# Revit family: Canilo
name_source: partatom
category: Lighting Fixtures
revit_build: Autodesk Revit 2017 (Build: 20190508_0315(x64)
units: mm (PartAtom-declared; Revit-internal decimal feet)

## family parameters
Cut with Voids When Loaded = No
Host = Face
Light Source = No
OmniClass Number = 23.80.70.11
OmniClass Title = Luminaries for Internal Lighting
Part Type = Normal
Room Calculation Point = No
Round Connector Dimension = Use Diameter
Shared = Yes

## types (810) — shared parameters
Canilo_Deko_Mat = Oktalite_Alu_RAL_9016
DegreeOfProtection = IP20
Height = 215 mm  [stored 0.705381 ft]
Length = 105 mm
Light Source = Canilo_LS : CANILO_LED_SP_2700_2705
Manufacturer = Oktalite
Mounting = 3-circuit track adapter
ProductDataSheet = http://www.oktalite.com
Reference = CANILO
URL = http://www.oktalite.com
Weight = 1.8
Width = 125 mm  [stored 0.410105 ft]
zero-valued in all types: Ceiling cut-out, Default Elevation, Installation depth, Suspension Height, Suspension length

## per-type parameters (varying)
| type | Apparent Load | Beam angle | CRI | Cover / filter | IESFile | Lamp | Light colour | Lighting technology | Lumen category | Luminaire colour | Mat | SEO | System performance | TK_Body | TK_Optic | system luminous flux |
| CANILO  3P 05 LED2000-M VFL-c ETDD 05 | 31 VA | Very Wide Flood | - | clear | CANILO_LED IQ_VFL.ies | LED IQ | M | LED IQ | 2000 lm | RAL 9005 jet black | Oktalite_Alu_RAL_9005 | Oktalite_Canilo_WH3100 | 31 VA | 10161299 | 10147536 | 1890 lm |
| CANILO  3P 05 LED2000-M VFL  ETDD 05 | 31 VA | Very Wide Flood | - | without | CANILO_LED IQ_VFL.ies | LED IQ | M | LED IQ | 2000 lm | RAL 9005 jet black | Oktalite_Alu_RAL_9005 | Oktalite_Canilo_WH3100 | 31 VA | 10161299 | 10147502 | 1890 lm |
| CANILO  3P 05 LED2000-M WFL-c ETDD 05 | 31 VA | Wide Flood | - | clear | CANILO_LED IQ_WFL.ies | LED IQ | M | LED IQ | 2000 lm | RAL 9005 jet black | Oktalite_Alu_RAL_9005 | Oktalite_Canilo_WH3100 | 31 VA | 10161299 | 10147535 | 1890 lm |
| CANILO  3P 05 LED2000-M WFL  ETDD 05 | 31 VA | Wide Flood | - | without | CANILO_LED IQ_WFL.ies | LED IQ | M | LED IQ | 2000 lm | RAL 9005 jet black | Oktalite_Alu_RAL_9005 | Oktalite_Canilo_WH3100 | 31 VA | 10161299 | 10147501 | 1890 lm |
| CANILO  3P 05 LED2000-M FL-c ETDD 05 | 31 VA | Flood | - | clear | CANILO_LED IQ_FL.ies | LED IQ | M | LED IQ | 2000 lm | RAL 9005 jet black | Oktalite_Alu_RAL_9005 | Oktalite_Canilo_WH3100 | 31 VA | 10161299 | 10127064 | 1890 lm |
| CANILO  3P 05 LED2000-M FL  ETDD 05 | 31 VA | Flood | - | without | CANILO_LED IQ_FL.ies | LED IQ | M | LED IQ | 2000 lm | RAL 9005 jet black | Oktalite_Alu_RAL_9005 | Oktalite_Canilo_WH3100 | 31 VA | 10161299 | 10125196 | 1890 lm |
| CANILO  3P 05 LED2000-M MF-c ETDD 05 | 31 VA | Medium Flood | - | clear | CANILO_LED IQ_MF.ies | LED IQ | M | LED IQ | 2000 lm | RAL 9005 jet black | Oktalite_Alu_RAL_9005 | Oktalite_Canilo_WH3100 | 31 VA | 10161299 | 10127063 | 1890 lm |
| CANILO  3P 05 LED2000-M MF  ETDD 05 | 31 VA | Medium Flood | - | without | CANILO_LED IQ_MF.ies | LED IQ | M | LED IQ | 2000 lm | RAL 9005 jet black | Oktalite_Alu_RAL_9005 | Oktalite_Canilo_WH3100 | 31 VA | 10161299 | 10125193 | 1890 lm |
| CANILO  3P 05 LED2000-M SP-c ETDD 05 | 31 VA | Spot | - | clear | CANILO_LED IQ_SP.ies | LED IQ | M | LED IQ | 2000 lm | RAL 9005 jet black | Oktalite_Alu_RAL_9005 | Oktalite_Canilo_WH3100 | 31 VA | 10161299 | 10127062 | 1890 lm |
| CANILO  3P 05 LED2000-M SP  ETDD 05 | 31 VA | Spot | - | without | CANILO_LED IQ_SP.ies | LED IQ | M | LED IQ | 2000 lm | RAL 9005 jet black | Oktalite_Alu_RAL_9005 | Oktalite_Canilo_WH3100 | 31 VA | 10161299 | 10125190 | 1890 lm |
| CANILO  3P 05 LED2000-M VFL-c ETDD 03 | 31 VA | Very Wide Flood | - | clear | CANILO_LED IQ_VFL.ies | LED IQ | M | LED IQ | 2000 lm | RAL 9006 white aluminium | Oktalite_Alu_RAL_9006 | Oktalite_Canilo_WH3100 | 31 VA | 10161298 | 10147536 | 1890 lm |
| CANILO  3P 05 LED2000-M VFL  ETDD 03 | 31 VA | Very Wide Flood | - | without | CANILO_LED IQ_VFL.ies | LED IQ | M | LED IQ | 2000 lm | RAL 9006 white aluminium | Oktalite_Alu_RAL_9006 | Oktalite_Canilo_WH3100 | 31 VA | 10161298 | 10147502 | 1890 lm |
| CANILO  3P 05 LED2000-M WFL-c ETDD 03 | 31 VA | Wide Flood | - | clear | CANILO_LED IQ_WFL.ies | LED IQ | M | LED IQ | 2000 lm | RAL 9006 white aluminium | Oktalite_Alu_RAL_9006 | Oktalite_Canilo_WH3100 | 31 VA | 10161298 | 10147535 | 1890 lm |
| CANILO  3P 05 LED2000-M WFL  ETDD 03 | 31 VA | Wide Flood | - | without | CANILO_LED IQ_WFL.ies | LED IQ | M | LED IQ | 2000 lm | RAL 9006 white aluminium | Oktalite_Alu_RAL_9006 | Oktalite_Canilo_WH3100 | 31 VA | 10161298 | 10147501 | 1890 lm |
| CANILO  3P 05 LED2000-M FL-c ETDD 03 | 31 VA | Flood | - | clear | CANILO_LED IQ_FL.ies | LED IQ | M | LED IQ | 2000 lm | RAL 9006 white aluminium | Oktalite_Alu_RAL_9006 | Oktalite_Canilo_WH3100 | 31 VA | 10161298 | 10127064 | 1890 lm |
| CANILO  3P 05 LED2000-M FL  ETDD 03 | 31 VA | Flood | - | without | CANILO_LED IQ_FL.ies | LED IQ | M | LED IQ | 2000 lm | RAL 9006 white aluminium | Oktalite_Alu_RAL_9006 | Oktalite_Canilo_WH3100 | 31 VA | 10161298 | 10125196 | 1890 lm |
| CANILO  3P 05 LED2000-M MF-c ETDD 03 | 31 VA | Medium Flood | - | clear | CANILO_LED IQ_MF.ies | LED IQ | M | LED IQ | 2000 lm | RAL 9006 white aluminium | Oktalite_Alu_RAL_9006 | Oktalite_Canilo_WH3100 | 31 VA | 10161298 | 10127063 | 1890 lm |
| CANILO  3P 05 LED2000-M MF  ETDD 03 | 31 VA | Medium Flood | - | without | CANILO_LED IQ_MF.ies | LED IQ | M | LED IQ | 2000 lm | RAL 9006 white aluminium | Oktalite_Alu_RAL_9006 | Oktalite_Canilo_WH3100 | 31 VA | 10161298 | 10125193 | 1890 lm |
| CANILO  3P 05 LED2000-M SP-c ETDD 03 | 31 VA | Spot | - | clear | CANILO_LED IQ_SP.ies | LED IQ | M | LED IQ | 2000 lm | RAL 9006 white aluminium | Oktalite_Alu_RAL_9006 | Oktalite_Canilo_WH3100 | 31 VA | 10161298 | 10127062 | 1890 lm |
| CANILO  3P 05 LED2000-M SP  ETDD 03 | 31 VA | Spot | - | without | CANILO_LED IQ_SP.ies | LED IQ | M | LED IQ | 2000 lm | RAL 9006 white aluminium | Oktalite_Alu_RAL_9006 | Oktalite_Canilo_WH3100 | 31 VA | 10161298 | 10125190 | 1890 lm |
| CANILO  3P 01 LED2000-M VFL-c ETDD 01 | 31 VA | Very Wide Flood | - | clear | CANILO_LED IQ_VFL.ies | LED IQ | M | LED IQ | 2000 lm | RAL 9016 traffic white | Oktalite_Alu_RAL_9016 | Oktalite_Canilo_WH3100 | 31 VA | 10161297 | 10147536 | 1890 lm |
| CANILO  3P 01 LED2000-M VFL  ETDD 01 | 31 VA | Very Wide Flood | - | without | CANILO_LED IQ_VFL.ies | LED IQ | M | LED IQ | 2000 lm | RAL 9016 traffic white | Oktalite_Alu_RAL_9016 | Oktalite_Canilo_WH3100 | 31 VA | 10161297 | 10147502 | 1890 lm |
| CANILO  3P 01 LED2000-M WFL-c ETDD 01 | 31 VA | Wide Flood | - | clear | CANILO_LED IQ_WFL.ies | LED IQ | M | LED IQ | 2000 lm | RAL 9016 traffic white | Oktalite_Alu_RAL_9016 | Oktalite_Canilo_WH3100 | 31 VA | 10161297 | 10147535 | 1890 lm |
| CANILO  3P 01 LED2000-M WFL  ETDD 01 | 31 VA | Wide Flood | - | without | CANILO_LED IQ_WFL.ies | LED IQ | M | LED IQ | 2000 lm | RAL 9016 traffic white | Oktalite_Alu_RAL_9016 | Oktalite_Canilo_WH3100 | 31 VA | 10161297 | 10147501 | 1890 lm |
| CANILO  3P 01 LED2000-M FL-c ETDD 01 | 31 VA | Flood | - | clear | CANILO_LED IQ_FL.ies | LED IQ | M | LED IQ | 2000 lm | RAL 9016 traffic white | Oktalite_Alu_RAL_9016 | Oktalite_Canilo_WH3100 | 31 VA | 10161297 | 10127064 | 1890 lm |
| CANILO  3P 01 LED2000-M FL  ETDD 01 | 31 VA | Flood | - | without | CANILO_LED IQ_FL.ies | LED IQ | M | LED IQ | 2000 lm | RAL 9016 traffic white | Oktalite_Alu_RAL_9016 | Oktalite_Canilo_WH3100 | 31 VA | 10161297 | 10125196 | 1890 lm |
| CANILO  3P 01 LED2000-M MF-c ETDD 01 | 31 VA | Medium Flood | - | clear | CANILO_LED IQ_MF.ies | LED IQ | M | LED IQ | 2000 lm | RAL 9016 traffic white | Oktalite_Alu_RAL_9016 | Oktalite_Canilo_WH3100 | 31 VA | 10161297 | 10127063 | 1890 lm |
| CANILO  3P 01 LED2000-M MF  ETDD 01 | 31 VA | Medium Flood | - | without | CANILO_LED IQ_MF.ies | LED IQ | M | LED IQ | 2000 lm | RAL 9016 traffic white | Oktalite_Alu_RAL_9016 | Oktalite_Canilo_WH3100 | 31 VA | 10161297 | 10125193 | 1890 lm |
| CANILO  3P 01 LED2000-M SP-c ETDD 01 | 31 VA | Spot | - | clear | CANILO_LED IQ_SP.ies | LED IQ | M | LED IQ | 2000 lm | RAL 9016 traffic white | Oktalite_Alu_RAL_9016 | Oktalite_Canilo_WH3100 | 31 VA | 10161297 | 10127062 | 1890 lm |
| CANILO  3P 01 LED2000-M SP  ETDD 01 | 31 VA | Spot | - | without | CANILO_LED IQ_SP.ies | LED IQ | M | LED IQ | 2000 lm | RAL 9016 traffic white | Oktalite_Alu_RAL_9016 | Oktalite_Canilo_WH3100 | 31 VA | 10161297 | 10125190 | 1890 lm |
| CANILO  3P 05 LED2000-M+F VFL-c ETDD 05 | 31 VA | Very Wide Flood | - | clear | CANILO_LED IQ_VFL.ies | LED IQ | M+F | LED IQ | 2000 lm | RAL 9005 jet black | Oktalite_Alu_RAL_9005 | Oktalite_Canilo_WH3100 | 31 VA | 10161308 | 10147536 | 1785 lm |
| CANILO  3P 05 LED2000-M+F VFL  ETDD 05 | 31 VA | Very Wide Flood | - | without | CANILO_LED IQ_VFL.ies | LED IQ | M+F | LED IQ | 2000 lm | RAL 9005 jet black | Oktalite_Alu_RAL_9005 | Oktalite_Canilo_WH3100 | 31 VA | 10161308 | 10147502 | 1785 lm |
| CANILO  3P 05 LED2000-M+F WFL-c ETDD 05 | 31 VA | Wide Flood | - | clear | CANILO_LED IQ_WFL.ies | LED IQ | M+F | LED IQ | 2000 lm | RAL 9005 jet black | Oktalite_Alu_RAL_9005 | Oktalite_Canilo_WH3100 | 31 VA | 10161308 | 10147535 | 1785 lm |
| CANILO  3P 05 LED2000-M+F WFL  ETDD 05 | 31 VA | Wide Flood | - | without | CANILO_LED IQ_WFL.ies | LED IQ | M+F | LED IQ | 2000 lm | RAL 9005 jet black | Oktalite_Alu_RAL_9005 | Oktalite_Canilo_WH3100 | 31 VA | 10161308 | 10147501 | 1785 lm |
| CANILO  3P 05 LED2000-M+F FL-c ETDD 05 | 31 VA | Flood | - | clear | CANILO_LED IQ_FL.ies | LED IQ | M+F | LED IQ | 2000 lm | RAL 9005 jet black | Oktalite_Alu_RAL_9005 | Oktalite_Canilo_WH3100 | 31 VA | 10161308 | 10127064 | 1785 lm |
| CANILO  3P 05 LED2000-M+F FL  ETDD 05 | 31 VA | Flood | - | without | CANILO_LED IQ_FL.ies | LED IQ | M+F | LED IQ | 2000 lm | RAL 9005 jet black | Oktalite_Alu_RAL_9005 | Oktalite_Canilo_WH3100 | 31 VA | 10161308 | 10125196 | 1785 lm |
| CANILO  3P 05 LED2000-M+F MF-c ETDD 05 | 31 VA | Medium Flood | - | clear | CANILO_LED IQ_MF.ies | LED IQ | M+F | LED IQ | 2000 lm | RAL 9005 jet black | Oktalite_Alu_RAL_9005 | Oktalite_Canilo_WH3100 | 31 VA | 10161308 | 10127063 | 1785 lm |
| CANILO  3P 05 LED2000-M+F MF  ETDD 05 | 31 VA | Medium Flood | - | without | CANILO_LED IQ_MF.ies | LED IQ | M+F | LED IQ | 2000 lm | RAL 9005 jet black | Oktalite_Alu_RAL_9005 | Oktalite_Canilo_WH3100 | 31 VA | 10161308 | 10125193 | 1785 lm |
| CANILO  3P 05 LED2000-M+F SP-c ETDD 05 | 31 VA | Spot | - | clear | CANILO_LED IQ_SP.ies | LED IQ | M+F | LED IQ | 2000 lm | RAL 9005 jet black | Oktalite_Alu_RAL_9005 | Oktalite_Canilo_WH3100 | 31 VA | 10161308 | 10127062 | 1785 lm |
| CANILO  3P 05 LED2000-M+F SP  ETDD 05 | 31 VA | Spot | - | without | CANILO_LED IQ_SP.ies | LED IQ | M+F | LED IQ | 2000 lm | RAL 9005 jet black | Oktalite_Alu_RAL_9005 | Oktalite_Canilo_WH3100 | 31 VA | 10161308 | 10125190 | 1785 lm |
| CANILO  3P 05 LED2000-M+F VFL-c ETDD 03 | 31 VA | Very Wide Flood | - | clear | CANILO_LED IQ_VFL.ies | LED IQ | M+F | LED IQ | 2000 lm | RAL 9006 white aluminium | Oktalite_Alu_RAL_9006 | Oktalite_Canilo_WH3100 | 31 VA | 10161307 | 10147536 | 1785 lm |
| CANILO  3P 05 LED2000-M+F VFL  ETDD 03 | 31 VA | Very Wide Flood | - | without | CANILO_LED IQ_VFL.ies | LED IQ | M+F | LED IQ | 2000 lm | RAL 9006 white aluminium | Oktalite_Alu_RAL_9006 | Oktalite_Canilo_WH3100 | 31 VA | 10161307 | 10147502 | 1785 lm |
| CANILO  3P 05 LED2000-M+F WFL-c ETDD 03 | 31 VA | Wide Flood | - | clear | CANILO_LED IQ_WFL.ies | LED IQ | M+F | LED IQ | 2000 lm | RAL 9006 white aluminium | Oktalite_Alu_RAL_9006 | Oktalite_Canilo_WH3100 | 31 VA | 10161307 | 10147535 | 1785 lm |
| CANILO  3P 05 LED2000-M+F WFL  ETDD 03 | 31 VA | Wide Flood | - | without | CANILO_LED IQ_WFL.ies | LED IQ | M+F | LED IQ | 2000 lm | RAL 9006 white aluminium | Oktalite_Alu_RAL_9006 | Oktalite_Canilo_WH3100 | 31 VA | 10161307 | 10147501 | 1785 lm |
| CANILO  3P 05 LED2000-M+F FL-c ETDD 03 | 31 VA | Flood | - | clear | CANILO_LED IQ_FL.ies | LED IQ | M+F | LED IQ | 2000 lm | RAL 9006 white aluminium | Oktalite_Alu_RAL_9006 | Oktalite_Canilo_WH3100 | 31 VA | 10161307 | 10127064 | 1785 lm |
| CANILO  3P 05 LED2000-M+F FL  ETDD 03 | 31 VA | Flood | - | without | CANILO_LED IQ_FL.ies | LED IQ | M+F | LED IQ | 2000 lm | RAL 9006 white aluminium | Oktalite_Alu_RAL_9006 | Oktalite_Canilo_WH3100 | 31 VA | 10161307 | 10125196 | 1785 lm |
| CANILO  3P 05 LED2000-M+F MF-c ETDD 03 | 31 VA | Medium Flood | - | clear | CANILO_LED IQ_MF.ies | LED IQ | M+F | LED IQ | 2000 lm | RAL 9006 white aluminium | Oktalite_Alu_RAL_9006 | Oktalite_Canilo_WH3100 | 31 VA | 10161307 | 10127063 | 1785 lm |
| CANILO  3P 05 LED2000-M+F MF  ETDD 03 | 31 VA | Medium Flood | - | without | CANILO_LED IQ_MF.ies | LED IQ | M+F | LED IQ | 2000 lm | RAL 9006 white aluminium | Oktalite_Alu_RAL_9006 | Oktalite_Canilo_WH3100 | 31 VA | 10161307 | 10125193 | 1785 lm |
| CANILO  3P 05 LED2000-M+F SP-c ETDD 03 | 31 VA | Spot | - | clear | CANILO_LED IQ_SP.ies | LED IQ | M+F | LED IQ | 2000 lm | RAL 9006 white aluminium | Oktalite_Alu_RAL_9006 | Oktalite_Canilo_WH3100 | 31 VA | 10161307 | 10127062 | 1785 lm |
| CANILO  3P 05 LED2000-M+F SP  ETDD 03 | 31 VA | Spot | - | without | CANILO_LED IQ_SP.ies | LED IQ | M+F | LED IQ | 2000 lm | RAL 9006 white aluminium | Oktalite_Alu_RAL_9006 | Oktalite_Canilo_WH3100 | 31 VA | 10161307 | 10125190 | 1785 lm |
| CANILO  3P 01 LED2000-M+F VFL-c ETDD 01 | 31 VA | Very Wide Flood | - | clear | CANILO_LED IQ_VFL.ies | LED IQ | M+F | LED IQ | 2000 lm | RAL 9016 traffic white | Oktalite_Alu_RAL_9016 | Oktalite_Canilo_WH3100 | 31 VA | 10161306 | 10147536 | 1785 lm |
| CANILO  3P 01 LED2000-M+F VFL  ETDD 01 | 31 VA | Very Wide Flood | - | without | CANILO_LED IQ_VFL.ies | LED IQ | M+F | LED IQ | 2000 lm | RAL 9016 traffic white | Oktalite_Alu_RAL_9016 | Oktalite_Canilo_WH3100 | 31 VA | 10161306 | 10147502 | 1785 lm |
| CANILO  3P 01 LED2000-M+F WFL-c ETDD 01 | 31 VA | Wide Flood | - | clear | CANILO_LED IQ_WFL.ies | LED IQ | M+F | LED IQ | 2000 lm | RAL 9016 traffic white | Oktalite_Alu_RAL_9016 | Oktalite_Canilo_WH3100 | 31 VA | 10161306 | 10147535 | 1785 lm |
| CANILO  3P 01 LED2000-M+F WFL  ETDD 01 | 31 VA | Wide Flood | - | without | CANILO_LED IQ_WFL.ies | LED IQ | M+F | LED IQ | 2000 lm | RAL 9016 traffic white | Oktalite_Alu_RAL_9016 | Oktalite_Canilo_WH3100 | 31 VA | 10161306 | 10147501 | 1785 lm |
| CANILO  3P 01 LED2000-M+F FL-c ETDD 01 | 31 VA | Flood | - | clear | CANILO_LED IQ_FL.ies | LED IQ | M+F | LED IQ | 2000 lm | RAL 9016 traffic white | Oktalite_Alu_RAL_9016 | Oktalite_Canilo_WH3100 | 31 VA | 10161306 | 10127064 | 1785 lm |
| CANILO  3P 01 LED2000-M+F FL  ETDD 01 | 31 VA | Flood | - | without | CANILO_LED IQ_FL.ies | LED IQ | M+F | LED IQ | 2000 lm | RAL 9016 traffic white | Oktalite_Alu_RAL_9016 | Oktalite_Canilo_WH3100 | 31 VA | 10161306 | 10125196 | 1785 lm |
| CANILO  3P 01 LED2000-M+F MF-c ETDD 01 | 31 VA | Medium Flood | - | clear | CANILO_LED IQ_MF.ies | LED IQ | M+F | LED IQ | 2000 lm | RAL 9016 traffic white | Oktalite_Alu_RAL_9016 | Oktalite_Canilo_WH3100 | 31 VA | 10161306 | 10127063 | 1785 lm |
| CANILO  3P 01 LED2000-M+F MF  ETDD 01 | 31 VA | Medium Flood | - | without | CANILO_LED IQ_MF.ies | LED IQ | M+F | LED IQ | 2000 lm | RAL 9016 traffic white | Oktalite_Alu_RAL_9016 | Oktalite_Canilo_WH3100 | 31 VA | 10161306 | 10125193 | 1785 lm |
| CANILO  3P 01 LED2000-M+F SP-c ETDD 01 | 31 VA | Spot | - | clear | CANILO_LED IQ_SP.ies | LED IQ | M+F | LED IQ | 2000 lm | RAL 9016 traffic white | Oktalite_Alu_RAL_9016 | Oktalite_Canilo_WH3100 | 31 VA | 10161306 | 10127062 | 1785 lm |
| CANILO  3P 01 LED2000-M+F SP  ETDD 01 | 31 VA | Spot | - | without | CANILO_LED IQ_SP.ies | LED IQ | M+F | LED IQ | 2000 lm | RAL 9016 traffic white | Oktalite_Alu_RAL_9016 | Oktalite_Canilo_WH3100 | 31 VA | 10161306 | 10125190 | 1785 lm |
| CANILO  3P 05 LED3000-931 VFL-c ETDD 05 | 32 VA | Very Wide Flood | 95 | clear | CANILO_LED IQ_VFL.ies | LED IQ | 3100 K Best Colour | LED IQ | 3000 lm | RAL 9005 jet black | Oktalite_Alu_RAL_9005 | Oktalite_Canilo_WH3100 | 32 VA | 10161681 | 10147536 | 2895 lm |
| CANILO  3P 05 LED3000-931 VFL  ETDD 05 | 32 VA | Very Wide Flood | 95 | without | CANILO_LED IQ_VFL.ies | LED IQ | 3100 K Best Colour | LED IQ | 3000 lm | RAL 9005 jet black | Oktalite_Alu_RAL_9005 | Oktalite_Canilo_WH3100 | 32 VA | 10161681 | 10147502 | 2895 lm |
| CANILO  3P 05 LED3000-931 WFL-c ETDD 05 | 32 VA | Wide Flood | 95 | clear | CANILO_LED IQ_WFL.ies | LED IQ | 3100 K Best Colour | LED IQ | 3000 lm | RAL 9005 jet black | Oktalite_Alu_RAL_9005 | Oktalite_Canilo_WH3100 | 32 VA | 10161681 | 10147535 | 2895 lm |
| CANILO  3P 05 LED3000-931 WFL  ETDD 05 | 32 VA | Wide Flood | 95 | without | CANILO_LED IQ_WFL.ies | LED IQ | 3100 K Best Colour | LED IQ | 3000 lm | RAL 9005 jet black | Oktalite_Alu_RAL_9005 | Oktalite_Canilo_WH3100 | 32 VA | 10161681 | 10147501 | 2895 lm |
| CANILO  3P 05 LED3000-931 FL-c ETDD 05 | 32 VA | Flood | 95 | clear | CANILO_LED IQ_FL.ies | LED IQ | 3100 K Best Colour | LED IQ | 3000 lm | RAL 9005 jet black | Oktalite_Alu_RAL_9005 | Oktalite_Canilo_WH3100 | 32 VA | 10161681 | 10127064 | 2895 lm |
| CANILO  3P 05 LED3000-931 FL  ETDD 05 | 32 VA | Flood | 95 | without | CANILO_LED IQ_FL.ies | LED IQ | 3100 K Best Colour | LED IQ | 3000 lm | RAL 9005 jet black | Oktalite_Alu_RAL_9005 | Oktalite_Canilo_WH3100 | 32 VA | 10161681 | 10125196 | 2895 lm |
| CANILO  3P 05 LED3000-931 MF-c ETDD 05 | 32 VA | Medium Flood | 95 | clear | CANILO_LED IQ_MF.ies | LED IQ | 3100 K Best Colour | LED IQ | 3000 lm | RAL 9005 jet black | Oktalite_Alu_RAL_9005 | Oktalite_Canilo_WH3100 | 32 VA | 10161681 | 10127063 | 2895 lm |
| CANILO  3P 05 LED3000-931 MF  ETDD 05 | 32 VA | Medium Flood | 95 | without | CANILO_LED IQ_MF.ies | LED IQ | 3100 K Best Colour | LED IQ | 3000 lm | RAL 9005 jet black | Oktalite_Alu_RAL_9005 | Oktalite_Canilo_WH3100 | 32 VA | 10161681 | 10125193 | 2895 lm |
| CANILO  3P 05 LED3000-931 SP-c ETDD 05 | 32 VA | Spot | 95 | clear | CANILO_LED IQ_SP.ies | LED IQ | 3100 K Best Colour | LED IQ | 3000 lm | RAL 9005 jet black | Oktalite_Alu_RAL_9005 | Oktalite_Canilo_WH3100 | 32 VA | 10161681 | 10127062 | 2895 lm |
| CANILO  3P 05 LED3000-931 SP  ETDD 05 | 32 VA | Spot | 95 | without | CANILO_LED IQ_SP.ies | LED IQ | 3100 K Best Colour | LED IQ | 3000 lm | RAL 9005 jet black | Oktalite_Alu_RAL_9005 | Oktalite_Canilo_WH3100 | 32 VA | 10161681 | 10125190 | 2895 lm |
| CANILO  3P 05 LED3000-931 VFL-c ETDD 03 | 32 VA | Very Wide Flood | 95 | clear | CANILO_LED IQ_VFL.ies | LED IQ | 3100 K Best Colour | LED IQ | 3000 lm | RAL 9006 white aluminium | Oktalite_Alu_RAL_9006 | Oktalite_Canilo_WH3100 | 32 VA | 10161680 | 10147536 | 2895 lm |
| CANILO  3P 05 LED3000-931 VFL  ETDD 03 | 32 VA | Very Wide Flood | 95 | without | CANILO_LED IQ_VFL.ies | LED IQ | 3100 K Best Colour | LED IQ | 3000 lm | RAL 9006 white aluminium | Oktalite_Alu_RAL_9006 | Oktalite_Canilo_WH3100 | 32 VA | 10161680 | 10147502 | 2895 lm |
| CANILO  3P 05 LED3000-931 WFL-c ETDD 03 | 32 VA | Wide Flood | 95 | clear | CANILO_LED IQ_WFL.ies | LED IQ | 3100 K Best Colour | LED IQ | 3000 lm | RAL 9006 white aluminium | Oktalite_Alu_RAL_9006 | Oktalite_Canilo_WH3100 | 32 VA | 10161680 | 10147535 | 2895 lm |
| CANILO  3P 05 LED3000-931 WFL  ETDD 03 | 32 VA | Wide Flood | 95 | without | CANILO_LED IQ_WFL.ies | LED IQ | 3100 K Best Colour | LED IQ | 3000 lm | RAL 9006 white aluminium | Oktalite_Alu_RAL_9006 | Oktalite_Canilo_WH3100 | 32 VA | 10161680 | 10147501 | 2895 lm |
| CANILO  3P 05 LED3000-931 FL-c ETDD 03 | 32 VA | Flood | 95 | clear | CANILO_LED IQ_FL.ies | LED IQ | 3100 K Best Colour | LED IQ | 3000 lm | RAL 9006 white aluminium | Oktalite_Alu_RAL_9006 | Oktalite_Canilo_WH3100 | 32 VA | 10161680 | 10127064 | 2895 lm |
| CANILO  3P 05 LED3000-931 FL  ETDD 03 | 32 VA | Flood | 95 | without | CANILO_LED IQ_FL.ies | LED IQ | 3100 K Best Colour | LED IQ | 3000 lm | RAL 9006 white aluminium | Oktalite_Alu_RAL_9006 | Oktalite_Canilo_WH3100 | 32 VA | 10161680 | 10125196 | 2895 lm |
| CANILO  3P 05 LED3000-931 MF-c ETDD 03 | 32 VA | Medium Flood | 95 | clear | CANILO_LED IQ_MF.ies | LED IQ | 3100 K Best Colour | LED IQ | 3000 lm | RAL 9006 white aluminium | Oktalite_Alu_RAL_9006 | Oktalite_Canilo_WH3100 | 32 VA | 10161680 | 10127063 | 2895 lm |
| CANILO  3P 05 LED3000-931 MF  ETDD 03 | 32 VA | Medium Flood | 95 | without | CANILO_LED IQ_MF.ies | LED IQ | 3100 K Best Colour | LED IQ | 3000 lm | RAL 9006 white aluminium | Oktalite_Alu_RAL_9006 | Oktalite_Canilo_WH3100 | 32 VA | 10161680 | 10125193 | 2895 lm |
| CANILO  3P 05 LED3000-931 SP-c ETDD 03 | 32 VA | Spot | 95 | clear | CANILO_LED IQ_SP.ies | LED IQ | 3100 K Best Colour | LED IQ | 3000 lm | RAL 9006 white aluminium | Oktalite_Alu_RAL_9006 | Oktalite_Canilo_WH3100 | 32 VA | 10161680 | 10127062 | 2895 lm |
| CANILO  3P 05 LED3000-931 SP  ETDD 03 | 32 VA | Spot | 95 | without | CANILO_LED IQ_SP.ies | LED IQ | 3100 K Best Colour | LED IQ | 3000 lm | RAL 9006 white aluminium | Oktalite_Alu_RAL_9006 | Oktalite_Canilo_WH3100 | 32 VA | 10161680 | 10125190 | 2895 lm |
| CANILO  3P 01 LED3000-931 VFL-c ETDD 01 | 32 VA | Very Wide Flood | 95 | clear | CANILO_LED IQ_VFL.ies | LED IQ | 3100 K Best Colour | LED IQ | 3000 lm | RAL 9016 traffic white | Oktalite_Alu_RAL_9016 | Oktalite_Canilo_WH3100 | 32 VA | 10161679 | 10147536 | 2895 lm |
| CANILO  3P 01 LED3000-931 VFL  ETDD 01 | 32 VA | Very Wide Flood | 95 | without | CANILO_LED IQ_VFL.ies | LED IQ | 3100 K Best Colour | LED IQ | 3000 lm | RAL 9016 traffic white | Oktalite_Alu_RAL_9016 | Oktalite_Canilo_WH3100 | 32 VA | 10161679 | 10147502 | 2895 lm |
| CANILO  3P 01 LED3000-931 WFL-c ETDD 01 | 32 VA | Wide Flood | 95 | clear | CANILO_LED IQ_WFL.ies | LED IQ | 3100 K Best Colour | LED IQ | 3000 lm | RAL 9016 traffic white | Oktalite_Alu_RAL_9016 | Oktalite_Canilo_WH3100 | 32 VA | 10161679 | 10147535 | 2895 lm |
| CANILO  3P 01 LED3000-931 WFL  ETDD 01 | 32 VA | Wide Flood | 95 | without | CANILO_LED IQ_WFL.ies | LED IQ | 3100 K Best Colour | LED IQ | 3000 lm | RAL 9016 traffic white | Oktalite_Alu_RAL_9016 | Oktalite_Canilo_WH3100 | 32 VA | 10161679 | 10147501 | 2895 lm |
| CANILO  3P 01 LED3000-931 FL-c ETDD 01 | 32 VA | Flood | 95 | clear | CANILO_LED IQ_FL.ies | LED IQ | 3100 K Best Colour | LED IQ | 3000 lm | RAL 9016 traffic white | Oktalite_Alu_RAL_9016 | Oktalite_Canilo_WH3100 | 32 VA | 10161679 | 10127064 | 2895 lm |
| CANILO  3P 01 LED3000-931 FL  ETDD 01 | 32 VA | Flood | 95 | without | CANILO_LED IQ_FL.ies | LED IQ | 3100 K Best Colour | LED IQ | 3000 lm | RAL 9016 traffic white | Oktalite_Alu_RAL_9016 | Oktalite_Canilo_WH3100 | 32 VA | 10161679 | 10125196 | 2895 lm |
| CANILO  3P 01 LED3000-931 MF-c ETDD 01 | 32 VA | Medium Flood | 95 | clear | CANILO_LED IQ_MF.ies | LED IQ | 3100 K Best Colour | LED IQ | 3000 lm | RAL 9016 traffic white | Oktalite_Alu_RAL_9016 | Oktalite_Canilo_WH3100 | 32 VA | 10161679 | 10127063 | 2895 lm |
| CANILO  3P 01 LED3000-931 MF  ETDD 01 | 32 VA | Medium Flood | 95 | without | CANILO_LED IQ_MF.ies | LED IQ | 3100 K Best Colour | LED IQ | 3000 lm | RAL 9016 traffic white | Oktalite_Alu_RAL_9016 | Oktalite_Canilo_WH3100 | 32 VA | 10161679 | 10125193 | 2895 lm |
| CANILO  3P 01 LED3000-931 SP-c ETDD 01 | 32 VA | Spot | 95 | clear | CANILO_LED IQ_SP.ies | LED IQ | 3100 K Best Colour | LED IQ | 3000 lm | RAL 9016 traffic white | Oktalite_Alu_RAL_9016 | Oktalite_Canilo_WH3100 | 32 VA | 10161679 | 10127062 | 2895 lm |
| CANILO  3P 01 LED3000-931 SP  ETDD 01 | 32 VA | Spot | 95 | without | CANILO_LED IQ_SP.ies | LED IQ | 3100 K Best Colour | LED IQ | 3000 lm | RAL 9016 traffic white | Oktalite_Alu_RAL_9016 | Oktalite_Canilo_WH3100 | 32 VA | 10161679 | 10125190 | 2895 lm |
| CANILO  3P 05 LED3000-BVC VFL-c ETDD 05 | 31 VA | Very Wide Flood | - | clear | CANILO_LED IQ_VFL.ies | LED IQ | B+V+C | LED IQ | 3000 lm | RAL 9005 jet black | Oktalite_Alu_RAL_9005 | Oktalite_Canilo_WH3100 | 31 VA | 10161317 | 10147536 | 2860 lm |
| CANILO  3P 05 LED3000-BVC VFL  ETDD 05 | 31 VA | Very Wide Flood | - | without | CANILO_LED IQ_VFL.ies | LED IQ | B+V+C | LED IQ | 3000 lm | RAL 9005 jet black | Oktalite_Alu_RAL_9005 | Oktalite_Canilo_WH3100 | 31 VA | 10161317 | 10147502 | 2860 lm |
| CANILO  3P 05 LED3000-BVC WFL-c ETDD 05 | 31 VA | Wide Flood | - | clear | CANILO_LED IQ_WFL.ies | LED IQ | B+V+C | LED IQ | 3000 lm | RAL 9005 jet black | Oktalite_Alu_RAL_9005 | Oktalite_Canilo_WH3100 | 31 VA | 10161317 | 10147535 | 2860 lm |
| CANILO  3P 05 LED3000-BVC WFL  ETDD 05 | 31 VA | Wide Flood | - | without | CANILO_LED IQ_WFL.ies | LED IQ | B+V+C | LED IQ | 3000 lm | RAL 9005 jet black | Oktalite_Alu_RAL_9005 | Oktalite_Canilo_WH3100 | 31 VA | 10161317 | 10147501 | 2860 lm |
| CANILO  3P 05 LED3000-BVC FL-c ETDD 05 | 31 VA | Flood | - | clear | CANILO_LED IQ_FL.ies | LED IQ | B+V+C | LED IQ | 3000 lm | RAL 9005 jet black | Oktalite_Alu_RAL_9005 | Oktalite_Canilo_WH3100 | 31 VA | 10161317 | 10127064 | 2860 lm |
| CANILO  3P 05 LED3000-BVC FL  ETDD 05 | 31 VA | Flood | - | without | CANILO_LED IQ_FL.ies | LED IQ | B+V+C | LED IQ | 3000 lm | RAL 9005 jet black | Oktalite_Alu_RAL_9005 | Oktalite_Canilo_WH3100 | 31 VA | 10161317 | 10125196 | 2860 lm |
| CANILO  3P 05 LED3000-BVC MF-c ETDD 05 | 31 VA | Medium Flood | - | clear | CANILO_LED IQ_MF.ies | LED IQ | B+V+C | LED IQ | 3000 lm | RAL 9005 jet black | Oktalite_Alu_RAL_9005 | Oktalite_Canilo_WH3100 | 31 VA | 10161317 | 10127063 | 2860 lm |
| CANILO  3P 05 LED3000-BVC MF  ETDD 05 | 31 VA | Medium Flood | - | without | CANILO_LED IQ_MF.ies | LED IQ | B+V+C | LED IQ | 3000 lm | RAL 9005 jet black | Oktalite_Alu_RAL_9005 | Oktalite_Canilo_WH3100 | 31 VA | 10161317 | 10125193 | 2860 lm |
| CANILO  3P 05 LED3000-BVC SP-c ETDD 05 | 31 VA | Spot | - | clear | CANILO_LED IQ_SP.ies | LED IQ | B+V+C | LED IQ | 3000 lm | RAL 9005 jet black | Oktalite_Alu_RAL_9005 | Oktalite_Canilo_WH3100 | 31 VA | 10161317 | 10127062 | 2860 lm |
| CANILO  3P 05 LED3000-BVC SP  ETDD 05 | 31 VA | Spot | - | without | CANILO_LED IQ_SP.ies | LED IQ | B+V+C | LED IQ | 3000 lm | RAL 9005 jet black | Oktalite_Alu_RAL_9005 | Oktalite_Canilo_WH3100 | 31 VA | 10161317 | 10125190 | 2860 lm |
| CANILO  3P 05 LED3000-BVC VFL-c ETDD 03 | 31 VA | Very Wide Flood | - | clear | CANILO_LED IQ_VFL.ies | LED IQ | B+V+C | LED IQ | 3000 lm | RAL 9006 white aluminium | Oktalite_Alu_RAL_9006 | Oktalite_Canilo_WH3100 | 31 VA | 10161316 | 10147536 | 2860 lm |
| CANILO  3P 05 LED3000-BVC VFL  ETDD 03 | 31 VA | Very Wide Flood | - | without | CANILO_LED IQ_VFL.ies | LED IQ | B+V+C | LED IQ | 3000 lm | RAL 9006 white aluminium | Oktalite_Alu_RAL_9006 | Oktalite_Canilo_WH3100 | 31 VA | 10161316 | 10147502 | 2860 lm |
| CANILO  3P 05 LED3000-BVC WFL-c ETDD 03 | 31 VA | Wide Flood | - | clear | CANILO_LED IQ_WFL.ies | LED IQ | B+V+C | LED IQ | 3000 lm | RAL 9006 white aluminium | Oktalite_Alu_RAL_9006 | Oktalite_Canilo_WH3100 | 31 VA | 10161316 | 10147535 | 2860 lm |
| CANILO  3P 05 LED3000-BVC WFL  ETDD 03 | 31 VA | Wide Flood | - | without | CANILO_LED IQ_WFL.ies | LED IQ | B+V+C | LED IQ | 3000 lm | RAL 9006 white aluminium | Oktalite_Alu_RAL_9006 | Oktalite_Canilo_WH3100 | 31 VA | 10161316 | 10147501 | 2860 lm |
| CANILO  3P 05 LED3000-BVC FL-c ETDD 03 | 31 VA | Flood | - | clear | CANILO_LED IQ_FL.ies | LED IQ | B+V+C | LED IQ | 3000 lm | RAL 9006 white aluminium | Oktalite_Alu_RAL_9006 | Oktalite_Canilo_WH3100 | 31 VA | 10161316 | 10127064 | 2860 lm |
| CANILO  3P 05 LED3000-BVC FL  ETDD 03 | 31 VA | Flood | - | without | CANILO_LED IQ_FL.ies | LED IQ | B+V+C | LED IQ | 3000 lm | RAL 9006 white aluminium | Oktalite_Alu_RAL_9006 | Oktalite_Canilo_WH3100 | 31 VA | 10161316 | 10125196 | 2860 lm |
| CANILO  3P 05 LED3000-BVC MF-c ETDD 03 | 31 VA | Medium Flood | - | clear | CANILO_LED IQ_MF.ies | LED IQ | B+V+C | LED IQ | 3000 lm | RAL 9006 white aluminium | Oktalite_Alu_RAL_9006 | Oktalite_Canilo_WH3100 | 31 VA | 10161316 | 10127063 | 2860 lm |
| CANILO  3P 05 LED3000-BVC MF  ETDD 03 | 31 VA | Medium Flood | - | without | CANILO_LED IQ_MF.ies | LED IQ | B+V+C | LED IQ | 3000 lm | RAL 9006 white aluminium | Oktalite_Alu_RAL_9006 | Oktalite_Canilo_WH3100 | 31 VA | 10161316 | 10125193 | 2860 lm |
| CANILO  3P 05 LED3000-BVC SP-c ETDD 03 | 31 VA | Spot | - | clear | CANILO_LED IQ_SP.ies | LED IQ | B+V+C | LED IQ | 3000 lm | RAL 9006 white aluminium | Oktalite_Alu_RAL_9006 | Oktalite_Canilo_WH3100 | 31 VA | 10161316 | 10127062 | 2860 lm |
| CANILO  3P 05 LED3000-BVC SP  ETDD 03 | 31 VA | Spot | - | without | CANILO_LED IQ_SP.ies | LED IQ | B+V+C | LED IQ | 3000 lm | RAL 9006 white aluminium | Oktalite_Alu_RAL_9006 | Oktalite_Canilo_WH3100 | 31 VA | 10161316 | 10125190 | 2860 lm |
| CANILO  3P 01 LED3000-BVC VFL-c ETDD 01 | 31 VA | Very Wide Flood | - | clear | CANILO_LED IQ_VFL.ies | LED IQ | B+V+C | LED IQ | 3000 lm | RAL 9016 traffic white | Oktalite_Alu_RAL_9016 | Oktalite_Canilo_WH3100 | 31 VA | 10161315 | 10147536 | 2860 lm |
| CANILO  3P 01 LED3000-BVC VFL  ETDD 01 | 31 VA | Very Wide Flood | - | without | CANILO_LED IQ_VFL.ies | LED IQ | B+V+C | LED IQ | 3000 lm | RAL 9016 traffic white | Oktalite_Alu_RAL_9016 | Oktalite_Canilo_WH3100 | 31 VA | 10161315 | 10147502 | 2860 lm |
| CANILO  3P 01 LED3000-BVC WFL-c ETDD 01 | 31 VA | Wide Flood | - | clear | CANILO_LED IQ_WFL.ies | LED IQ | B+V+C | LED IQ | 3000 lm | RAL 9016 traffic white | Oktalite_Alu_RAL_9016 | Oktalite_Canilo_WH3100 | 31 VA | 10161315 | 10147535 | 2860 lm |
| CANILO  3P 01 LED3000-BVC WFL  ETDD 01 | 31 VA | Wide Flood | - | without | CANILO_LED IQ_WFL.ies | LED IQ | B+V+C | LED IQ | 3000 lm | RAL 9016 traffic white | Oktalite_Alu_RAL_9016 | Oktalite_Canilo_WH3100 | 31 VA | 10161315 | 10147501 | 2860 lm |
| CANILO  3P 01 LED3000-BVC FL-c ETDD 01 | 31 VA | Flood | - | clear | CANILO_LED IQ_FL.ies | LED IQ | B+V+C | LED IQ | 3000 lm | RAL 9016 traffic white | Oktalite_Alu_RAL_9016 | Oktalite_Canilo_WH3100 | 31 VA | 10161315 | 10127064 | 2860 lm |
| CANILO  3P 01 LED3000-BVC FL  ETDD 01 | 31 VA | Flood | - | without | CANILO_LED IQ_FL.ies | LED IQ | B+V+C | LED IQ | 3000 lm | RAL 9016 traffic white | Oktalite_Alu_RAL_9016 | Oktalite_Canilo_WH3100 | 31 VA | 10161315 | 10125196 | 2860 lm |
| CANILO  3P 01 LED3000-BVC MF-c ETDD 01 | 31 VA | Medium Flood | - | clear | CANILO_LED IQ_MF.ies | LED IQ | B+V+C | LED IQ | 3000 lm | RAL 9016 traffic white | Oktalite_Alu_RAL_9016 | Oktalite_Canilo_WH3100 | 31 VA | 10161315 | 10127063 | 2860 lm |
| CANILO  3P 01 LED3000-BVC MF  ETDD 01 | 31 VA | Medium Flood | - | without | CANILO_LED IQ_MF.ies | LED IQ | B+V+C | LED IQ | 3000 lm | RAL 9016 traffic white | Oktalite_Alu_RAL_9016 | Oktalite_Canilo_WH3100 | 31 VA | 10161315 | 10125193 | 2860 lm |
| CANILO  3P 01 LED3000-BVC SP-c ETDD 01 | 31 VA | Spot | - | clear | CANILO_LED IQ_SP.ies | LED IQ | B+V+C | LED IQ | 3000 lm | RAL 9016 traffic white | Oktalite_Alu_RAL_9016 | Oktalite_Canilo_WH3100 | 31 VA | 10161315 | 10127062 | 2860 lm |
| CANILO  3P 01 LED3000-BVC SP  ETDD 01 | 31 VA | Spot | - | without | CANILO_LED IQ_SP.ies | LED IQ | B+V+C | LED IQ | 3000 lm | RAL 9016 traffic white | Oktalite_Alu_RAL_9016 | Oktalite_Canilo_WH3100 | 31 VA | 10161315 | 10125190 | 2860 lm |
| CANILO  3P 05 LED4000-831 VFL-c ETDD 05 | 32 VA | Very Wide Flood | 85 | clear | CANILO_LED IQ_VFL.ies | LED IQ | 3100 K Efficient Colour | LED IQ | 4000 lm | RAL 9005 jet black | Oktalite_Alu_RAL_9005 | Oktalite_Canilo_WH3100 | 32 VA | 10161699 | 10147536 | 3555 lm |
| CANILO  3P 05 LED4000-831 VFL  ETDD 05 | 32 VA | Very Wide Flood | 85 | without | CANILO_LED IQ_VFL.ies | LED IQ | 3100 K Efficient Colour | LED IQ | 4000 lm | RAL 9005 jet black | Oktalite_Alu_RAL_9005 | Oktalite_Canilo_WH3100 | 32 VA | 10161699 | 10147502 | 3555 lm |
| CANILO  3P 05 LED4000-831 WFL-c ETDD 05 | 32 VA | Wide Flood | 85 | clear | CANILO_LED IQ_WFL.ies | LED IQ | 3100 K Efficient Colour | LED IQ | 4000 lm | RAL 9005 jet black | Oktalite_Alu_RAL_9005 | Oktalite_Canilo_WH3100 | 32 VA | 10161699 | 10147535 | 3555 lm |
| CANILO  3P 05 LED4000-831 WFL  ETDD 05 | 32 VA | Wide Flood | 85 | without | CANILO_LED IQ_WFL.ies | LED IQ | 3100 K Efficient Colour | LED IQ | 4000 lm | RAL 9005 jet black | Oktalite_Alu_RAL_9005 | Oktalite_Canilo_WH3100 | 32 VA | 10161699 | 10147501 | 3555 lm |
| CANILO  3P 05 LED4000-831 FL-c ETDD 05 | 32 VA | Flood | 85 | clear | CANILO_LED IQ_FL.ies | LED IQ | 3100 K Efficient Colour | LED IQ | 4000 lm | RAL 9005 jet black | Oktalite_Alu_RAL_9005 | Oktalite_Canilo_WH3100 | 32 VA | 10161699 | 10127064 | 3555 lm |
| CANILO  3P 05 LED4000-831 FL  ETDD 05 | 32 VA | Flood | 85 | without | CANILO_LED IQ_FL.ies | LED IQ | 3100 K Efficient Colour | LED IQ | 4000 lm | RAL 9005 jet black | Oktalite_Alu_RAL_9005 | Oktalite_Canilo_WH3100 | 32 VA | 10161699 | 10125196 | 3555 lm |
| CANILO  3P 05 LED4000-831 MF-c ETDD 05 | 32 VA | Medium Flood | 85 | clear | CANILO_LED IQ_MF.ies | LED IQ | 3100 K Efficient Colour | LED IQ | 4000 lm | RAL 9005 jet black | Oktalite_Alu_RAL_9005 | Oktalite_Canilo_WH3100 | 32 VA | 10161699 | 10127063 | 3555 lm |
| CANILO  3P 05 LED4000-831 MF  ETDD 05 | 32 VA | Medium Flood | 85 | without | CANILO_LED IQ_MF.ies | LED IQ | 3100 K Efficient Colour | LED IQ | 4000 lm | RAL 9005 jet black | Oktalite_Alu_RAL_9005 | Oktalite_Canilo_WH3100 | 32 VA | 10161699 | 10125193 | 3555 lm |
| CANILO  3P 05 LED4000-831 SP-c ETDD 05 | 32 VA | Spot | 85 | clear | CANILO_LED IQ_SP.ies | LED IQ | 3100 K Efficient Colour | LED IQ | 4000 lm | RAL 9005 jet black | Oktalite_Alu_RAL_9005 | Oktalite_Canilo_WH3100 | 32 VA | 10161699 | 10127062 | 3555 lm |
| CANILO  3P 05 LED4000-831 SP  ETDD 05 | 32 VA | Spot | 85 | without | CANILO_LED IQ_SP.ies | LED IQ | 3100 K Efficient Colour | LED IQ | 4000 lm | RAL 9005 jet black | Oktalite_Alu_RAL_9005 | Oktalite_Canilo_WH3100 | 32 VA | 10161699 | 10125190 | 3555 lm |
| CANILO  3P 05 LED4000-831 VFL-c ETDD 03 | 32 VA | Very Wide Flood | 85 | clear | CANILO_LED IQ_VFL.ies | LED IQ | 3100 K Efficient Colour | LED IQ | 4000 lm | RAL 9006 white aluminium | Oktalite_Alu_RAL_9006 | Oktalite_Canilo_WH3100 | 32 VA | 10161698 | 10147536 | 3555 lm |
| CANILO  3P 05 LED4000-831 VFL  ETDD 03 | 32 VA | Very Wide Flood | 85 | without | CANILO_LED IQ_VFL.ies | LED IQ | 3100 K Efficient Colour | LED IQ | 4000 lm | RAL 9006 white aluminium | Oktalite_Alu_RAL_9006 | Oktalite_Canilo_WH3100 | 32 VA | 10161698 | 10147502 | 3555 lm |
| CANILO  3P 05 LED4000-831 WFL-c ETDD 03 | 32 VA | Wide Flood | 85 | clear | CANILO_LED IQ_WFL.ies | LED IQ | 3100 K Efficient Colour | LED IQ | 4000 lm | RAL 9006 white aluminium | Oktalite_Alu_RAL_9006 | Oktalite_Canilo_WH3100 | 32 VA | 10161698 | 10147535 | 3555 lm |
| CANILO  3P 05 LED4000-831 WFL  ETDD 03 | 32 VA | Wide Flood | 85 | without | CANILO_LED IQ_WFL.ies | LED IQ | 3100 K Efficient Colour | LED IQ | 4000 lm | RAL 9006 white aluminium | Oktalite_Alu_RAL_9006 | Oktalite_Canilo_WH3100 | 32 VA | 10161698 | 10147501 | 3555 lm |
| CANILO  3P 05 LED4000-831 FL-c ETDD 03 | 32 VA | Flood | 85 | clear | CANILO_LED IQ_FL.ies | LED IQ | 3100 K Efficient Colour | LED IQ | 4000 lm | RAL 9006 white aluminium | Oktalite_Alu_RAL_9006 | Oktalite_Canilo_WH3100 | 32 VA | 10161698 | 10127064 | 3555 lm |
| CANILO  3P 05 LED4000-831 FL  ETDD 03 | 32 VA | Flood | 85 | without | CANILO_LED IQ_FL.ies | LED IQ | 3100 K Efficient Colour | LED IQ | 4000 lm | RAL 9006 white aluminium | Oktalite_Alu_RAL_9006 | Oktalite_Canilo_WH3100 | 32 VA | 10161698 | 10125196 | 3555 lm |
| CANILO  3P 05 LED4000-831 MF-c ETDD 03 | 32 VA | Medium Flood | 85 | clear | CANILO_LED IQ_MF.ies | LED IQ | 3100 K Efficient Colour | LED IQ | 4000 lm | RAL 9006 white aluminium | Oktalite_Alu_RAL_9006 | Oktalite_Canilo_WH3100 | 32 VA | 10161698 | 10127063 | 3555 lm |
| CANILO  3P 05 LED4000-831 MF  ETDD 03 | 32 VA | Medium Flood | 85 | without | CANILO_LED IQ_MF.ies | LED IQ | 3100 K Efficient Colour | LED IQ | 4000 lm | RAL 9006 white aluminium | Oktalite_Alu_RAL_9006 | Oktalite_Canilo_WH3100 | 32 VA | 10161698 | 10125193 | 3555 lm |
| CANILO  3P 05 LED4000-831 SP-c ETDD 03 | 32 VA | Spot | 85 | clear | CANILO_LED IQ_SP.ies | LED IQ | 3100 K Efficient Colour | LED IQ | 4000 lm | RAL 9006 white aluminium | Oktalite_Alu_RAL_9006 | Oktalite_Canilo_WH3100 | 32 VA | 10161698 | 10127062 | 3555 lm |
| CANILO  3P 05 LED4000-831 SP  ETDD 03 | 32 VA | Spot | 85 | without | CANILO_LED IQ_SP.ies | LED IQ | 3100 K Efficient Colour | LED IQ | 4000 lm | RAL 9006 white aluminium | Oktalite_Alu_RAL_9006 | Oktalite_Canilo_WH3100 | 32 VA | 10161698 | 10125190 | 3555 lm |
| CANILO  3P 01 LED4000-831 VFL-c ETDD 01 | 32 VA | Very Wide Flood | 85 | clear | CANILO_LED IQ_VFL.ies | LED IQ | 3100 K Efficient Colour | LED IQ | 4000 lm | RAL 9016 traffic white | Oktalite_Alu_RAL_9016 | Oktalite_Canilo_WH3100 | 32 VA | 10161697 | 10147536 | 3555 lm |
| CANILO  3P 01 LED4000-831 VFL  ETDD 01 | 32 VA | Very Wide Flood | 85 | without | CANILO_LED IQ_VFL.ies | LED IQ | 3100 K Efficient Colour | LED IQ | 4000 lm | RAL 9016 traffic white | Oktalite_Alu_RAL_9016 | Oktalite_Canilo_WH3100 | 32 VA | 10161697 | 10147502 | 3555 lm |
| CANILO  3P 01 LED4000-831 WFL-c ETDD 01 | 32 VA | Wide Flood | 85 | clear | CANILO_LED IQ_WFL.ies | LED IQ | 3100 K Efficient Colour | LED IQ | 4000 lm | RAL 9016 traffic white | Oktalite_Alu_RAL_9016 | Oktalite_Canilo_WH3100 | 32 VA | 10161697 | 10147535 | 3555 lm |
| CANILO  3P 01 LED4000-831 WFL  ETDD 01 | 32 VA | Wide Flood | 85 | without | CANILO_LED IQ_WFL.ies | LED IQ | 3100 K Efficient Colour | LED IQ | 4000 lm | RAL 9016 traffic white | Oktalite_Alu_RAL_9016 | Oktalite_Canilo_WH3100 | 32 VA | 10161697 | 10147501 | 3555 lm |
| CANILO  3P 01 LED4000-831 FL-c ETDD 01 | 32 VA | Flood | 85 | clear | CANILO_LED IQ_FL.ies | LED IQ | 3100 K Efficient Colour | LED IQ | 4000 lm | RAL 9016 traffic white | Oktalite_Alu_RAL_9016 | Oktalite_Canilo_WH3100 | 32 VA | 10161697 | 10127064 | 3555 lm |
| CANILO  3P 01 LED4000-831 FL  ETDD 01 | 32 VA | Flood | 85 | without | CANILO_LED IQ_FL.ies | LED IQ | 3100 K Efficient Colour | LED IQ | 4000 lm | RAL 9016 traffic white | Oktalite_Alu_RAL_9016 | Oktalite_Canilo_WH3100 | 32 VA | 10161697 | 10125196 | 3555 lm |
| CANILO  3P 01 LED4000-831 MF-c ETDD 01 | 32 VA | Medium Flood | 85 | clear | CANILO_LED IQ_MF.ies | LED IQ | 3100 K Efficient Colour | LED IQ | 4000 lm | RAL 9016 traffic white | Oktalite_Alu_RAL_9016 | Oktalite_Canilo_WH3100 | 32 VA | 10161697 | 10127063 | 3555 lm |
| CANILO  3P 01 LED4000-831 MF  ETDD 01 | 32 VA | Medium Flood | 85 | without | CANILO_LED IQ_MF.ies | LED IQ | 3100 K Efficient Colour | LED IQ | 4000 lm | RAL 9016 traffic white | Oktalite_Alu_RAL_9016 | Oktalite_Canilo_WH3100 | 32 VA | 10161697 | 10125193 | 3555 lm |
| CANILO  3P 01 LED4000-831 SP-c ETDD 01 | 32 VA | Spot | 85 | clear | CANILO_LED IQ_SP.ies | LED IQ | 3100 K Efficient Colour | LED IQ | 4000 lm | RAL 9016 traffic white | Oktalite_Alu_RAL_9016 | Oktalite_Canilo_WH3100 | 32 VA | 10161697 | 10127062 | 3555 lm |
| CANILO  3P 01 LED4000-831 SP  ETDD 01 | 32 VA | Spot | 85 | without | CANILO_LED IQ_SP.ies | LED IQ | 3100 K Efficient Colour | LED IQ | 4000 lm | RAL 9016 traffic white | Oktalite_Alu_RAL_9016 | Oktalite_Canilo_WH3100 | 32 VA | 10161697 | 10125190 | 3555 lm |
| CANILO  3P 05 LED4000-840 VFL-c ETDD 05 | 32 VA | Very Wide Flood | 85 | clear | CANILO_LED IQ_VFL.ies | LED IQ | 4000 K | LED IQ | 4000 lm | RAL 9005 jet black | Oktalite_Alu_RAL_9005 | Oktalite_Canilo_WH4000 | 32 VA | 10161711 | 10147536 | 3780 lm |
| CANILO  3P 05 LED4000-840 VFL  ETDD 05 | 32 VA | Very Wide Flood | 85 | without | CANILO_LED IQ_VFL.ies | LED IQ | 4000 K | LED IQ | 4000 lm | RAL 9005 jet black | Oktalite_Alu_RAL_9005 | Oktalite_Canilo_WH4000 | 32 VA | 10161711 | 10147502 | 3780 lm |
| CANILO  3P 05 LED4000-840 WFL-c ETDD 05 | 32 VA | Wide Flood | 85 | clear | CANILO_LED IQ_WFL.ies | LED IQ | 4000 K | LED IQ | 4000 lm | RAL 9005 jet black | Oktalite_Alu_RAL_9005 | Oktalite_Canilo_WH4000 | 32 VA | 10161711 | 10147535 | 3780 lm |
| CANILO  3P 05 LED4000-840 WFL  ETDD 05 | 32 VA | Wide Flood | 85 | without | CANILO_LED IQ_WFL.ies | LED IQ | 4000 K | LED IQ | 4000 lm | RAL 9005 jet black | Oktalite_Alu_RAL_9005 | Oktalite_Canilo_WH4000 | 32 VA | 10161711 | 10147501 | 3780 lm |
| CANILO  3P 05 LED4000-840 FL-c ETDD 05 | 32 VA | Flood | 85 | clear | CANILO_LED IQ_FL.ies | LED IQ | 4000 K | LED IQ | 4000 lm | RAL 9005 jet black | Oktalite_Alu_RAL_9005 | Oktalite_Canilo_WH4000 | 32 VA | 10161711 | 10127064 | 3780 lm |
| CANILO  3P 05 LED4000-840 FL  ETDD 05 | 32 VA | Flood | 85 | without | CANILO_LED IQ_FL.ies | LED IQ | 4000 K | LED IQ | 4000 lm | RAL 9005 jet black | Oktalite_Alu_RAL_9005 | Oktalite_Canilo_WH4000 | 32 VA | 10161711 | 10125196 | 3780 lm |
| CANILO  3P 05 LED4000-840 MF-c ETDD 05 | 32 VA | Medium Flood | 85 | clear | CANILO_LED IQ_MF.ies | LED IQ | 4000 K | LED IQ | 4000 lm | RAL 9005 jet black | Oktalite_Alu_RAL_9005 | Oktalite_Canilo_WH4000 | 32 VA | 10161711 | 10127063 | 3780 lm |
| CANILO  3P 05 LED4000-840 MF  ETDD 05 | 32 VA | Medium Flood | 85 | without | CANILO_LED IQ_MF.ies | LED IQ | 4000 K | LED IQ | 4000 lm | RAL 9005 jet black | Oktalite_Alu_RAL_9005 | Oktalite_Canilo_WH4000 | 32 VA | 10161711 | 10125193 | 3780 lm |
| CANILO  3P 05 LED4000-840 SP-c ETDD 05 | 32 VA | Spot | 85 | clear | CANILO_LED IQ_SP.ies | LED IQ | 4000 K | LED IQ | 4000 lm | RAL 9005 jet black | Oktalite_Alu_RAL_9005 | Oktalite_Canilo_WH4000 | 32 VA | 10161711 | 10127062 | 3780 lm |
| CANILO  3P 05 LED4000-840 SP  ETDD 05 | 32 VA | Spot | 85 | without | CANILO_LED IQ_SP.ies | LED IQ | 4000 K | LED IQ | 4000 lm | RAL 9005 jet black | Oktalite_Alu_RAL_9005 | Oktalite_Canilo_WH4000 | 32 VA | 10161711 | 10125190 | 3780 lm |
| CANILO  3P 05 LED4000-840 VFL-c ETDD 03 | 32 VA | Very Wide Flood | 85 | clear | CANILO_LED IQ_VFL.ies | LED IQ | 4000 K | LED IQ | 4000 lm | RAL 9006 white aluminium | Oktalite_Alu_RAL_9006 | Oktalite_Canilo_WH4000 | 32 VA | 10161710 | 10147536 | 3780 lm |
| CANILO  3P 05 LED4000-840 VFL  ETDD 03 | 32 VA | Very Wide Flood | 85 | without | CANILO_LED IQ_VFL.ies | LED IQ | 4000 K | LED IQ | 4000 lm | RAL 9006 white aluminium | Oktalite_Alu_RAL_9006 | Oktalite_Canilo_WH4000 | 32 VA | 10161710 | 10147502 | 3780 lm |
| CANILO  3P 05 LED4000-840 WFL-c ETDD 03 | 32 VA | Wide Flood | 85 | clear | CANILO_LED IQ_WFL.ies | LED IQ | 4000 K | LED IQ | 4000 lm | RAL 9006 white aluminium | Oktalite_Alu_RAL_9006 | Oktalite_Canilo_WH4000 | 32 VA | 10161710 | 10147535 | 3780 lm |
| CANILO  3P 05 LED4000-840 WFL  ETDD 03 | 32 VA | Wide Flood | 85 | without | CANILO_LED IQ_WFL.ies | LED IQ | 4000 K | LED IQ | 4000 lm | RAL 9006 white aluminium | Oktalite_Alu_RAL_9006 | Oktalite_Canilo_WH4000 | 32 VA | 10161710 | 10147501 | 3780 lm |
| CANILO  3P 05 LED4000-840 FL-c ETDD 03 | 32 VA | Flood | 85 | clear | CANILO_LED IQ_FL.ies | LED IQ | 4000 K | LED IQ | 4000 lm | RAL 9006 white aluminium | Oktalite_Alu_RAL_9006 | Oktalite_Canilo_WH4000 | 32 VA | 10161710 | 10127064 | 3780 lm |
| CANILO  3P 05 LED4000-840 FL  ETDD 03 | 32 VA | Flood | 85 | without | CANILO_LED IQ_FL.ies | LED IQ | 4000 K | LED IQ | 4000 lm | RAL 9006 white aluminium | Oktalite_Alu_RAL_9006 | Oktalite_Canilo_WH4000 | 32 VA | 10161710 | 10125196 | 3780 lm |
| CANILO  3P 05 LED4000-840 MF-c ETDD 03 | 32 VA | Medium Flood | 85 | clear | CANILO_LED IQ_MF.ies | LED IQ | 4000 K | LED IQ | 4000 lm | RAL 9006 white aluminium | Oktalite_Alu_RAL_9006 | Oktalite_Canilo_WH4000 | 32 VA | 10161710 | 10127063 | 3780 lm |
| CANILO  3P 05 LED4000-840 MF  ETDD 03 | 32 VA | Medium Flood | 85 | without | CANILO_LED IQ_MF.ies | LED IQ | 4000 K | LED IQ | 4000 lm | RAL 9006 white aluminium | Oktalite_Alu_RAL_9006 | Oktalite_Canilo_WH4000 | 32 VA | 10161710 | 10125193 | 3780 lm |
| CANILO  3P 05 LED4000-840 SP-c ETDD 03 | 32 VA | Spot | 85 | clear | CANILO_LED IQ_SP.ies | LED IQ | 4000 K | LED IQ | 4000 lm | RAL 9006 white aluminium | Oktalite_Alu_RAL_9006 | Oktalite_Canilo_WH4000 | 32 VA | 10161710 | 10127062 | 3780 lm |
| CANILO  3P 05 LED4000-840 SP  ETDD 03 | 32 VA | Spot | 85 | without | CANILO_LED IQ_SP.ies | LED IQ | 4000 K | LED IQ | 4000 lm | RAL 9006 white aluminium | Oktalite_Alu_RAL_9006 | Oktalite_Canilo_WH4000 | 32 VA | 10161710 | 10125190 | 3780 lm |
| CANILO  3P 01 LED4000-840 VFL-c ETDD 01 | 32 VA | Very Wide Flood | 85 | clear | CANILO_LED IQ_VFL.ies | LED IQ | 4000 K | LED IQ | 4000 lm | RAL 9016 traffic white | Oktalite_Alu_RAL_9016 | Oktalite_Canilo_WH4000 | 32 VA | 10161709 | 10147536 | 3780 lm |
| CANILO  3P 01 LED4000-840 VFL  ETDD 01 | 32 VA | Very Wide Flood | 85 | without | CANILO_LED IQ_VFL.ies | LED IQ | 4000 K | LED IQ | 4000 lm | RAL 9016 traffic white | Oktalite_Alu_RAL_9016 | Oktalite_Canilo_WH4000 | 32 VA | 10161709 | 10147502 | 3780 lm |
| CANILO  3P 01 LED4000-840 WFL-c ETDD 01 | 32 VA | Wide Flood | 85 | clear | CANILO_LED IQ_WFL.ies | LED IQ | 4000 K | LED IQ | 4000 lm | RAL 9016 traffic white | Oktalite_Alu_RAL_9016 | Oktalite_Canilo_WH4000 | 32 VA | 10161709 | 10147535 | 3780 lm |
| CANILO  3P 01 LED4000-840 WFL  ETDD 01 | 32 VA | Wide Flood | 85 | without | CANILO_LED IQ_WFL.ies | LED IQ | 4000 K | LED IQ | 4000 lm | RAL 9016 traffic white | Oktalite_Alu_RAL_9016 | Oktalite_Canilo_WH4000 | 32 VA | 10161709 | 10147501 | 3780 lm |
| CANILO  3P 01 LED4000-840 FL-c ETDD 01 | 32 VA | Flood | 85 | clear | CANILO_LED IQ_FL.ies | LED IQ | 4000 K | LED IQ | 4000 lm | RAL 9016 traffic white | Oktalite_Alu_RAL_9016 | Oktalite_Canilo_WH4000 | 32 VA | 10161709 | 10127064 | 3780 lm |
| CANILO  3P 01 LED4000-840 FL  ETDD 01 | 32 VA | Flood | 85 | without | CANILO_LED IQ_FL.ies | LED IQ | 4000 K | LED IQ | 4000 lm | RAL 9016 traffic white | Oktalite_Alu_RAL_9016 | Oktalite_Canilo_WH4000 | 32 VA | 10161709 | 10125196 | 3780 lm |
| CANILO  3P 01 LED4000-840 MF-c ETDD 01 | 32 VA | Medium Flood | 85 | clear | CANILO_LED IQ_MF.ies | LED IQ | 4000 K | LED IQ | 4000 lm | RAL 9016 traffic white | Oktalite_Alu_RAL_9016 | Oktalite_Canilo_WH4000 | 32 VA | 10161709 | 10127063 | 3780 lm |
| CANILO  3P 01 LED4000-840 MF  ETDD 01 | 32 VA | Medium Flood | 85 | without | CANILO_LED IQ_MF.ies | LED IQ | 4000 K | LED IQ | 4000 lm | RAL 9016 traffic white | Oktalite_Alu_RAL_9016 | Oktalite_Canilo_WH4000 | 32 VA | 10161709 | 10125193 | 3780 lm |
| CANILO  3P 01 LED4000-840 SP-c ETDD 01 | 32 VA | Spot | 85 | clear | CANILO_LED IQ_SP.ies | LED IQ | 4000 K | LED IQ | 4000 lm | RAL 9016 traffic white | Oktalite_Alu_RAL_9016 | Oktalite_Canilo_WH4000 | 32 VA | 10161709 | 10127062 | 3780 lm |
| CANILO  3P 01 LED4000-840 SP  ETDD 01 | 32 VA | Spot | 85 | without | CANILO_LED IQ_SP.ies | LED IQ | 4000 K | LED IQ | 4000 lm | RAL 9016 traffic white | Oktalite_Alu_RAL_9016 | Oktalite_Canilo_WH4000 | 32 VA | 10161709 | 10125190 | 3780 lm |
| CANILO  3P 05 LED4000-835 VFL-c ETDD 05 | 32 VA | Very Wide Flood | 85 | clear | CANILO_LED IQ_VFL.ies | LED IQ | 3500 K | LED IQ | 4000 lm | RAL 9005 jet black | Oktalite_Alu_RAL_9005 | Oktalite_Canilo_WH3500 | 32 VA | 10161705 | 10147536 | 3700 lm |
| CANILO  3P 05 LED4000-835 VFL  ETDD 05 | 32 VA | Very Wide Flood | 85 | without | CANILO_LED IQ_VFL.ies | LED IQ | 3500 K | LED IQ | 4000 lm | RAL 9005 jet black | Oktalite_Alu_RAL_9005 | Oktalite_Canilo_WH3500 | 32 VA | 10161705 | 10147502 | 3700 lm |
| CANILO  3P 05 LED4000-835 WFL-c ETDD 05 | 32 VA | Wide Flood | 85 | clear | CANILO_LED IQ_WFL.ies | LED IQ | 3500 K | LED IQ | 4000 lm | RAL 9005 jet black | Oktalite_Alu_RAL_9005 | Oktalite_Canilo_WH3500 | 32 VA | 10161705 | 10147535 | 3700 lm |
| CANILO  3P 05 LED4000-835 WFL  ETDD 05 | 32 VA | Wide Flood | 85 | without | CANILO_LED IQ_WFL.ies | LED IQ | 3500 K | LED IQ | 4000 lm | RAL 9005 jet black | Oktalite_Alu_RAL_9005 | Oktalite_Canilo_WH3500 | 32 VA | 10161705 | 10147501 | 3700 lm |
| CANILO  3P 05 LED4000-835 FL-c ETDD 05 | 32 VA | Flood | 85 | clear | CANILO_LED IQ_FL.ies | LED IQ | 3500 K | LED IQ | 4000 lm | RAL 9005 jet black | Oktalite_Alu_RAL_9005 | Oktalite_Canilo_WH3500 | 32 VA | 10161705 | 10127064 | 3700 lm |
| CANILO  3P 05 LED4000-835 FL  ETDD 05 | 32 VA | Flood | 85 | without | CANILO_LED IQ_FL.ies | LED IQ | 3500 K | LED IQ | 4000 lm | RAL 9005 jet black | Oktalite_Alu_RAL_9005 | Oktalite_Canilo_WH3500 | 32 VA | 10161705 | 10125196 | 3700 lm |
| CANILO  3P 05 LED4000-835 MF-c ETDD 05 | 32 VA | Medium Flood | 85 | clear | CANILO_LED IQ_MF.ies | LED IQ | 3500 K | LED IQ | 4000 lm | RAL 9005 jet black | Oktalite_Alu_RAL_9005 | Oktalite_Canilo_WH3500 | 32 VA | 10161705 | 10127063 | 3700 lm |
| CANILO  3P 05 LED4000-835 MF  ETDD 05 | 32 VA | Medium Flood | 85 | without | CANILO_LED IQ_MF.ies | LED IQ | 3500 K | LED IQ | 4000 lm | RAL 9005 jet black | Oktalite_Alu_RAL_9005 | Oktalite_Canilo_WH3500 | 32 VA | 10161705 | 10125193 | 3700 lm |
| CANILO  3P 05 LED4000-835 SP-c ETDD 05 | 32 VA | Spot | 85 | clear | CANILO_LED IQ_SP.ies | LED IQ | 3500 K | LED IQ | 4000 lm | RAL 9005 jet black | Oktalite_Alu_RAL_9005 | Oktalite_Canilo_WH3500 | 32 VA | 10161705 | 10127062 | 3700 lm |
| CANILO  3P 05 LED4000-835 SP  ETDD 05 | 32 VA | Spot | 85 | without | CANILO_LED IQ_SP.ies | LED IQ | 3500 K | LED IQ | 4000 lm | RAL 9005 jet black | Oktalite_Alu_RAL_9005 | Oktalite_Canilo_WH3500 | 32 VA | 10161705 | 10125190 | 3700 lm |
| CANILO  3P 05 LED4000-835 VFL-c ETDD 03 | 32 VA | Very Wide Flood | 85 | clear | CANILO_LED IQ_VFL.ies | LED IQ | 3500 K | LED IQ | 4000 lm | RAL 9006 white aluminium | Oktalite_Alu_RAL_9006 | Oktalite_Canilo_WH3500 | 32 VA | 10161704 | 10147536 | 3700 lm |
| CANILO  3P 05 LED4000-835 VFL  ETDD 03 | 32 VA | Very Wide Flood | 85 | without | CANILO_LED IQ_VFL.ies | LED IQ | 3500 K | LED IQ | 4000 lm | RAL 9006 white aluminium | Oktalite_Alu_RAL_9006 | Oktalite_Canilo_WH3500 | 32 VA | 10161704 | 10147502 | 3700 lm |
| CANILO  3P 05 LED4000-835 WFL-c ETDD 03 | 32 VA | Wide Flood | 85 | clear | CANILO_LED IQ_WFL.ies | LED IQ | 3500 K | LED IQ | 4000 lm | RAL 9006 white aluminium | Oktalite_Alu_RAL_9006 | Oktalite_Canilo_WH3500 | 32 VA | 10161704 | 10147535 | 3700 lm |
| CANILO  3P 05 LED4000-835 WFL  ETDD 03 | 32 VA | Wide Flood | 85 | without | CANILO_LED IQ_WFL.ies | LED IQ | 3500 K | LED IQ | 4000 lm | RAL 9006 white aluminium | Oktalite_Alu_RAL_9006 | Oktalite_Canilo_WH3500 | 32 VA | 10161704 | 10147501 | 3700 lm |
| CANILO  3P 05 LED4000-835 FL-c ETDD 03 | 32 VA | Flood | 85 | clear | CANILO_LED IQ_FL.ies | LED IQ | 3500 K | LED IQ | 4000 lm | RAL 9006 white aluminium | Oktalite_Alu_RAL_9006 | Oktalite_Canilo_WH3500 | 32 VA | 10161704 | 10127064 | 3700 lm |
| CANILO  3P 05 LED4000-835 FL  ETDD 03 | 32 VA | Flood | 85 | without | CANILO_LED IQ_FL.ies | LED IQ | 3500 K | LED IQ | 4000 lm | RAL 9006 white aluminium | Oktalite_Alu_RAL_9006 | Oktalite_Canilo_WH3500 | 32 VA | 10161704 | 10125196 | 3700 lm |
| CANILO  3P 05 LED4000-835 MF-c ETDD 03 | 32 VA | Medium Flood | 85 | clear | CANILO_LED IQ_MF.ies | LED IQ | 3500 K | LED IQ | 4000 lm | RAL 9006 white aluminium | Oktalite_Alu_RAL_9006 | Oktalite_Canilo_WH3500 | 32 VA | 10161704 | 10127063 | 3700 lm |
| CANILO  3P 05 LED4000-835 MF  ETDD 03 | 32 VA | Medium Flood | 85 | without | CANILO_LED IQ_MF.ies | LED IQ | 3500 K | LED IQ | 4000 lm | RAL 9006 white aluminium | Oktalite_Alu_RAL_9006 | Oktalite_Canilo_WH3500 | 32 VA | 10161704 | 10125193 | 3700 lm |
| CANILO  3P 05 LED4000-835 SP-c ETDD 03 | 32 VA | Spot | 85 | clear | CANILO_LED IQ_SP.ies | LED IQ | 3500 K | LED IQ | 4000 lm | RAL 9006 white aluminium | Oktalite_Alu_RAL_9006 | Oktalite_Canilo_WH3500 | 32 VA | 10161704 | 10127062 | 3700 lm |
| CANILO  3P 05 LED4000-835 SP  ETDD 03 | 32 VA | Spot | 85 | without | CANILO_LED IQ_SP.ies | LED IQ | 3500 K | LED IQ | 4000 lm | RAL 9006 white aluminium | Oktalite_Alu_RAL_9006 | Oktalite_Canilo_WH3500 | 32 VA | 10161704 | 10125190 | 3700 lm |
| CANILO  3P 01 LED4000-835 VFL-c ETDD 01 | 32 VA | Very Wide Flood | 85 | clear | CANILO_LED IQ_VFL.ies | LED IQ | 3500 K | LED IQ | 4000 lm | RAL 9016 traffic white | Oktalite_Alu_RAL_9016 | Oktalite_Canilo_WH3500 | 32 VA | 10161703 | 10147536 | 3700 lm |
| CANILO  3P 01 LED4000-835 VFL  ETDD 01 | 32 VA | Very Wide Flood | 85 | without | CANILO_LED IQ_VFL.ies | LED IQ | 3500 K | LED IQ | 4000 lm | RAL 9016 traffic white | Oktalite_Alu_RAL_9016 | Oktalite_Canilo_WH3500 | 32 VA | 10161703 | 10147502 | 3700 lm |
| CANILO  3P 01 LED4000-835 WFL-c ETDD 01 | 32 VA | Wide Flood | 85 | clear | CANILO_LED IQ_WFL.ies | LED IQ | 3500 K | LED IQ | 4000 lm | RAL 9016 traffic white | Oktalite_Alu_RAL_9016 | Oktalite_Canilo_WH3500 | 32 VA | 10161703 | 10147535 | 3700 lm |
| CANILO  3P 01 LED4000-835 WFL  ETDD 01 | 32 VA | Wide Flood | 85 | without | CANILO_LED IQ_WFL.ies | LED IQ | 3500 K | LED IQ | 4000 lm | RAL 9016 traffic white | Oktalite_Alu_RAL_9016 | Oktalite_Canilo_WH3500 | 32 VA | 10161703 | 10147501 | 3700 lm |
| CANILO  3P 01 LED4000-835 FL-c ETDD 01 | 32 VA | Flood | 85 | clear | CANILO_LED IQ_FL.ies | LED IQ | 3500 K | LED IQ | 4000 lm | RAL 9016 traffic white | Oktalite_Alu_RAL_9016 | Oktalite_Canilo_WH3500 | 32 VA | 10161703 | 10127064 | 3700 lm |
| CANILO  3P 01 LED4000-835 FL  ETDD 01 | 32 VA | Flood | 85 | without | CANILO_LED IQ_FL.ies | LED IQ | 3500 K | LED IQ | 4000 lm | RAL 9016 traffic white | Oktalite_Alu_RAL_9016 | Oktalite_Canilo_WH3500 | 32 VA | 10161703 | 10125196 | 3700 lm |
| CANILO  3P 01 LED4000-835 MF-c ETDD 01 | 32 VA | Medium Flood | 85 | clear | CANILO_LED IQ_MF.ies | LED IQ | 3500 K | LED IQ | 4000 lm | RAL 9016 traffic white | Oktalite_Alu_RAL_9016 | Oktalite_Canilo_WH3500 | 32 VA | 10161703 | 10127063 | 3700 lm |
| CANILO  3P 01 LED4000-835 MF  ETDD 01 | 32 VA | Medium Flood | 85 | without | CANILO_LED IQ_MF.ies | LED IQ | 3500 K | LED IQ | 4000 lm | RAL 9016 traffic white | Oktalite_Alu_RAL_9016 | Oktalite_Canilo_WH3500 | 32 VA | 10161703 | 10125193 | 3700 lm |
| CANILO  3P 01 LED4000-835 SP-c ETDD 01 | 32 VA | Spot | 85 | clear | CANILO_LED IQ_SP.ies | LED IQ | 3500 K | LED IQ | 4000 lm | RAL 9016 traffic white | Oktalite_Alu_RAL_9016 | Oktalite_Canilo_WH3500 | 32 VA | 10161703 | 10127062 | 3700 lm |
| CANILO  3P 01 LED4000-835 SP  ETDD 01 | 32 VA | Spot | 85 | without | CANILO_LED IQ_SP.ies | LED IQ | 3500 K | LED IQ | 4000 lm | RAL 9016 traffic white | Oktalite_Alu_RAL_9016 | Oktalite_Canilo_WH3500 | 32 VA | 10161703 | 10125190 | 3700 lm |
| CANILO  3P 05 LED4000-830 VFL-c ETDD 05 | 32 VA | Very Wide Flood | 85 | clear | CANILO_LED IQ_VFL.ies | LED IQ | 3000 K | LED IQ | 4000 lm | RAL 9005 jet black | Oktalite_Alu_RAL_9005 | Oktalite_Canilo_WH3000 | 32 VA | 10161693 | 10147536 | 3655 lm |
| CANILO  3P 05 LED4000-830 VFL  ETDD 05 | 32 VA | Very Wide Flood | 85 | without | CANILO_LED IQ_VFL.ies | LED IQ | 3000 K | LED IQ | 4000 lm | RAL 9005 jet black | Oktalite_Alu_RAL_9005 | Oktalite_Canilo_WH3000 | 32 VA | 10161693 | 10147502 | 3655 lm |
| CANILO  3P 05 LED4000-830 WFL-c ETDD 05 | 32 VA | Wide Flood | 85 | clear | CANILO_LED IQ_WFL.ies | LED IQ | 3000 K | LED IQ | 4000 lm | RAL 9005 jet black | Oktalite_Alu_RAL_9005 | Oktalite_Canilo_WH3000 | 32 VA | 10161693 | 10147535 | 3655 lm |
| CANILO  3P 05 LED4000-830 WFL  ETDD 05 | 32 VA | Wide Flood | 85 | without | CANILO_LED IQ_WFL.ies | LED IQ | 3000 K | LED IQ | 4000 lm | RAL 9005 jet black | Oktalite_Alu_RAL_9005 | Oktalite_Canilo_WH3000 | 32 VA | 10161693 | 10147501 | 3655 lm |
| CANILO  3P 05 LED4000-830 FL-c ETDD 05 | 32 VA | Flood | 85 | clear | CANILO_LED IQ_FL.ies | LED IQ | 3000 K | LED IQ | 4000 lm | RAL 9005 jet black | Oktalite_Alu_RAL_9005 | Oktalite_Canilo_WH3000 | 32 VA | 10161693 | 10127064 | 3655 lm |
| CANILO  3P 05 LED4000-830 FL  ETDD 05 | 32 VA | Flood | 85 | without | CANILO_LED IQ_FL.ies | LED IQ | 3000 K | LED IQ | 4000 lm | RAL 9005 jet black | Oktalite_Alu_RAL_9005 | Oktalite_Canilo_WH3000 | 32 VA | 10161693 | 10125196 | 3655 lm |
| CANILO  3P 05 LED4000-830 MF-c ETDD 05 | 32 VA | Medium Flood | 85 | clear | CANILO_LED IQ_MF.ies | LED IQ | 3000 K | LED IQ | 4000 lm | RAL 9005 jet black | Oktalite_Alu_RAL_9005 | Oktalite_Canilo_WH3000 | 32 VA | 10161693 | 10127063 | 3655 lm |
| CANILO  3P 05 LED4000-830 MF  ETDD 05 | 32 VA | Medium Flood | 85 | without | CANILO_LED IQ_MF.ies | LED IQ | 3000 K | LED IQ | 4000 lm | RAL 9005 jet black | Oktalite_Alu_RAL_9005 | Oktalite_Canilo_WH3000 | 32 VA | 10161693 | 10125193 | 3655 lm |
| CANILO  3P 05 LED4000-830 SP-c ETDD 05 | 32 VA | Spot | 85 | clear | CANILO_LED IQ_SP.ies | LED IQ | 3000 K | LED IQ | 4000 lm | RAL 9005 jet black | Oktalite_Alu_RAL_9005 | Oktalite_Canilo_WH3000 | 32 VA | 10161693 | 10127062 | 3655 lm |
| CANILO  3P 05 LED4000-830 SP  ETDD 05 | 32 VA | Spot | 85 | without | CANILO_LED IQ_SP.ies | LED IQ | 3000 K | LED IQ | 4000 lm | RAL 9005 jet black | Oktalite_Alu_RAL_9005 | Oktalite_Canilo_WH3000 | 32 VA | 10161693 | 10125190 | 3655 lm |
| CANILO  3P 05 LED4000-830 VFL-c ETDD 03 | 32 VA | Very Wide Flood | 85 | clear | CANILO_LED IQ_VFL.ies | LED IQ | 3000 K | LED IQ | 4000 lm | RAL 9006 white aluminium | Oktalite_Alu_RAL_9006 | Oktalite_Canilo_WH3000 | 32 VA | 10161692 | 10147536 | 3655 lm |
| CANILO  3P 05 LED4000-830 VFL  ETDD 03 | 32 VA | Very Wide Flood | 85 | without | CANILO_LED IQ_VFL.ies | LED IQ | 3000 K | LED IQ | 4000 lm | RAL 9006 white aluminium | Oktalite_Alu_RAL_9006 | Oktalite_Canilo_WH3000 | 32 VA | 10161692 | 10147502 | 3655 lm |
| CANILO  3P 05 LED4000-830 WFL-c ETDD 03 | 32 VA | Wide Flood | 85 | clear | CANILO_LED IQ_WFL.ies | LED IQ | 3000 K | LED IQ | 4000 lm | RAL 9006 white aluminium | Oktalite_Alu_RAL_9006 | Oktalite_Canilo_WH3000 | 32 VA | 10161692 | 10147535 | 3655 lm |
| CANILO  3P 05 LED4000-830 WFL  ETDD 03 | 32 VA | Wide Flood | 85 | without | CANILO_LED IQ_WFL.ies | LED IQ | 3000 K | LED IQ | 4000 lm | RAL 9006 white aluminium | Oktalite_Alu_RAL_9006 | Oktalite_Canilo_WH3000 | 32 VA | 10161692 | 10147501 | 3655 lm |
| CANILO  3P 05 LED4000-830 FL-c ETDD 03 | 32 VA | Flood | 85 | clear | CANILO_LED IQ_FL.ies | LED IQ | 3000 K | LED IQ | 4000 lm | RAL 9006 white aluminium | Oktalite_Alu_RAL_9006 | Oktalite_Canilo_WH3000 | 32 VA | 10161692 | 10127064 | 3655 lm |
| CANILO  3P 05 LED4000-830 FL  ETDD 03 | 32 VA | Flood | 85 | without | CANILO_LED IQ_FL.ies | LED IQ | 3000 K | LED IQ | 4000 lm | RAL 9006 white aluminium | Oktalite_Alu_RAL_9006 | Oktalite_Canilo_WH3000 | 32 VA | 10161692 | 10125196 | 3655 lm |
| CANILO  3P 05 LED4000-830 MF-c ETDD 03 | 32 VA | Medium Flood | 85 | clear | CANILO_LED IQ_MF.ies | LED IQ | 3000 K | LED IQ | 4000 lm | RAL 9006 white aluminium | Oktalite_Alu_RAL_9006 | Oktalite_Canilo_WH3000 | 32 VA | 10161692 | 10127063 | 3655 lm |
| CANILO  3P 05 LED4000-830 MF  ETDD 03 | 32 VA | Medium Flood | 85 | without | CANILO_LED IQ_MF.ies | LED IQ | 3000 K | LED IQ | 4000 lm | RAL 9006 white aluminium | Oktalite_Alu_RAL_9006 | Oktalite_Canilo_WH3000 | 32 VA | 10161692 | 10125193 | 3655 lm |
| CANILO  3P 05 LED4000-830 SP-c ETDD 03 | 32 VA | Spot | 85 | clear | CANILO_LED IQ_SP.ies | LED IQ | 3000 K | LED IQ | 4000 lm | RAL 9006 white aluminium | Oktalite_Alu_RAL_9006 | Oktalite_Canilo_WH3000 | 32 VA | 10161692 | 10127062 | 3655 lm |
| CANILO  3P 05 LED4000-830 SP  ETDD 03 | 32 VA | Spot | 85 | without | CANILO_LED IQ_SP.ies | LED IQ | 3000 K | LED IQ | 4000 lm | RAL 9006 white aluminium | Oktalite_Alu_RAL_9006 | Oktalite_Canilo_WH3000 | 32 VA | 10161692 | 10125190 | 3655 lm |
| CANILO  3P 01 LED4000-830 VFL-c ETDD 01 | 32 VA | Very Wide Flood | 85 | clear | CANILO_LED IQ_VFL.ies | LED IQ | 3000 K | LED IQ | 4000 lm | RAL 9016 traffic white | Oktalite_Alu_RAL_9016 | Oktalite_Canilo_WH3000 | 32 VA | 10161691 | 10147536 | 3655 lm |
| CANILO  3P 01 LED4000-830 VFL  ETDD 01 | 32 VA | Very Wide Flood | 85 | without | CANILO_LED IQ_VFL.ies | LED IQ | 3000 K | LED IQ | 4000 lm | RAL 9016 traffic white | Oktalite_Alu_RAL_9016 | Oktalite_Canilo_WH3000 | 32 VA | 10161691 | 10147502 | 3655 lm |
| CANILO  3P 01 LED4000-830 WFL-c ETDD 01 | 32 VA | Wide Flood | 85 | clear | CANILO_LED IQ_WFL.ies | LED IQ | 3000 K | LED IQ | 4000 lm | RAL 9016 traffic white | Oktalite_Alu_RAL_9016 | Oktalite_Canilo_WH3000 | 32 VA | 10161691 | 10147535 | 3655 lm |
| CANILO  3P 01 LED4000-830 WFL  ETDD 01 | 32 VA | Wide Flood | 85 | without | CANILO_LED IQ_WFL.ies | LED IQ | 3000 K | LED IQ | 4000 lm | RAL 9016 traffic white | Oktalite_Alu_RAL_9016 | Oktalite_Canilo_WH3000 | 32 VA | 10161691 | 10147501 | 3655 lm |
| CANILO  3P 01 LED4000-830 FL-c ETDD 01 | 32 VA | Flood | 85 | clear | CANILO_LED IQ_FL.ies | LED IQ | 3000 K | LED IQ | 4000 lm | RAL 9016 traffic white | Oktalite_Alu_RAL_9016 | Oktalite_Canilo_WH3000 | 32 VA | 10161691 | 10127064 | 3655 lm |
| CANILO  3P 01 LED4000-830 FL  ETDD 01 | 32 VA | Flood | 85 | without | CANILO_LED IQ_FL.ies | LED IQ | 3000 K | LED IQ | 4000 lm | RAL 9016 traffic white | Oktalite_Alu_RAL_9016 | Oktalite_Canilo_WH3000 | 32 VA | 10161691 | 10125196 | 3655 lm |
| CANILO  3P 01 LED4000-830 MF-c ETDD 01 | 32 VA | Medium Flood | 85 | clear | CANILO_LED IQ_MF.ies | LED IQ | 3000 K | LED IQ | 4000 lm | RAL 9016 traffic white | Oktalite_Alu_RAL_9016 | Oktalite_Canilo_WH3000 | 32 VA | 10161691 | 10127063 | 3655 lm |
| CANILO  3P 01 LED4000-830 MF  ETDD 01 | 32 VA | Medium Flood | 85 | without | CANILO_LED IQ_MF.ies | LED IQ | 3000 K | LED IQ | 4000 lm | RAL 9016 traffic white | Oktalite_Alu_RAL_9016 | Oktalite_Canilo_WH3000 | 32 VA | 10161691 | 10125193 | 3655 lm |
| CANILO  3P 01 LED4000-830 SP-c ETDD 01 | 32 VA | Spot | 85 | clear | CANILO_LED IQ_SP.ies | LED IQ | 3000 K | LED IQ | 4000 lm | RAL 9016 traffic white | Oktalite_Alu_RAL_9016 | Oktalite_Canilo_WH3000 | 32 VA | 10161691 | 10127062 | 3655 lm |
| CANILO  3P 01 LED4000-830 SP  ETDD 01 | 32 VA | Spot | 85 | without | CANILO_LED IQ_SP.ies | LED IQ | 3000 K | LED IQ | 4000 lm | RAL 9016 traffic white | Oktalite_Alu_RAL_9016 | Oktalite_Canilo_WH3000 | 32 VA | 10161691 | 10125190 | 3655 lm |
| CANILO  3P 05 LED4000-827 VFL-c ETDD 05 | 32 VA | Very Wide Flood | 82 | clear | CANILO_LED IQ_VFL.ies | LED IQ | 2700 K | LED IQ | 4000 lm | RAL 9005 jet black | Oktalite_Alu_RAL_9005 | Oktalite_Canilo_WH2700 | 32 VA | 10161687 | 10147536 | 3395 lm |
| CANILO  3P 05 LED4000-827 VFL  ETDD 05 | 32 VA | Very Wide Flood | 82 | without | CANILO_LED IQ_VFL.ies | LED IQ | 2700 K | LED IQ | 4000 lm | RAL 9005 jet black | Oktalite_Alu_RAL_9005 | Oktalite_Canilo_WH2700 | 32 VA | 10161687 | 10147502 | 3395 lm |
| CANILO  3P 05 LED4000-827 WFL-c ETDD 05 | 32 VA | Wide Flood | 82 | clear | CANILO_LED IQ_WFL.ies | LED IQ | 2700 K | LED IQ | 4000 lm | RAL 9005 jet black | Oktalite_Alu_RAL_9005 | Oktalite_Canilo_WH2700 | 32 VA | 10161687 | 10147535 | 3395 lm |
| CANILO  3P 05 LED4000-827 WFL  ETDD 05 | 32 VA | Wide Flood | 82 | without | CANILO_LED IQ_WFL.ies | LED IQ | 2700 K | LED IQ | 4000 lm | RAL 9005 jet black | Oktalite_Alu_RAL_9005 | Oktalite_Canilo_WH2700 | 32 VA | 10161687 | 10147501 | 3395 lm |
| CANILO  3P 05 LED4000-827 FL-c ETDD 05 | 32 VA | Flood | 82 | clear | CANILO_LED IQ_FL.ies | LED IQ | 2700 K | LED IQ | 4000 lm | RAL 9005 jet black | Oktalite_Alu_RAL_9005 | Oktalite_Canilo_WH2700 | 32 VA | 10161687 | 10127064 | 3395 lm |
| CANILO  3P 05 LED4000-827 FL  ETDD 05 | 32 VA | Flood | 82 | without | CANILO_LED IQ_FL.ies | LED IQ | 2700 K | LED IQ | 4000 lm | RAL 9005 jet black | Oktalite_Alu_RAL_9005 | Oktalite_Canilo_WH2700 | 32 VA | 10161687 | 10125196 | 3395 lm |
| CANILO  3P 05 LED4000-827 MF-c ETDD 05 | 32 VA | Medium Flood | 82 | clear | CANILO_LED IQ_MF.ies | LED IQ | 2700 K | LED IQ | 4000 lm | RAL 9005 jet black | Oktalite_Alu_RAL_9005 | Oktalite_Canilo_WH2700 | 32 VA | 10161687 | 10127063 | 3395 lm |
| CANILO  3P 05 LED4000-827 MF  ETDD 05 | 32 VA | Medium Flood | 82 | without | CANILO_LED IQ_MF.ies | LED IQ | 2700 K | LED IQ | 4000 lm | RAL 9005 jet black | Oktalite_Alu_RAL_9005 | Oktalite_Canilo_WH2700 | 32 VA | 10161687 | 10125193 | 3395 lm |
| CANILO  3P 05 LED4000-827 SP-c ETDD 05 | 32 VA | Spot | 82 | clear | CANILO_LED IQ_SP.ies | LED IQ | 2700 K | LED IQ | 4000 lm | RAL 9005 jet black | Oktalite_Alu_RAL_9005 | Oktalite_Canilo_WH2700 | 32 VA | 10161687 | 10127062 | 3395 lm |
| CANILO  3P 05 LED4000-827 SP  ETDD 05 | 32 VA | Spot | 82 | without | CANILO_LED IQ_SP.ies | LED IQ | 2700 K | LED IQ | 4000 lm | RAL 9005 jet black | Oktalite_Alu_RAL_9005 | Oktalite_Canilo_WH2700 | 32 VA | 10161687 | 10125190 | 3395 lm |
| CANILO  3P 05 LED4000-827 VFL-c ETDD 03 | 32 VA | Very Wide Flood | 82 | clear | CANILO_LED IQ_VFL.ies | LED IQ | 2700 K | LED IQ | 4000 lm | RAL 9006 white aluminium | Oktalite_Alu_RAL_9006 | Oktalite_Canilo_WH2700 | 32 VA | 10161686 | 10147536 | 3395 lm |
| CANILO  3P 05 LED4000-827 VFL  ETDD 03 | 32 VA | Very Wide Flood | 82 | without | CANILO_LED IQ_VFL.ies | LED IQ | 2700 K | LED IQ | 4000 lm | RAL 9006 white aluminium | Oktalite_Alu_RAL_9006 | Oktalite_Canilo_WH2700 | 32 VA | 10161686 | 10147502 | 3395 lm |
| CANILO  3P 05 LED4000-827 WFL-c ETDD 03 | 32 VA | Wide Flood | 82 | clear | CANILO_LED IQ_WFL.ies | LED IQ | 2700 K | LED IQ | 4000 lm | RAL 9006 white aluminium | Oktalite_Alu_RAL_9006 | Oktalite_Canilo_WH2700 | 32 VA | 10161686 | 10147535 | 3395 lm |
| CANILO  3P 05 LED4000-827 WFL  ETDD 03 | 32 VA | Wide Flood | 82 | without | CANILO_LED IQ_WFL.ies | LED IQ | 2700 K | LED IQ | 4000 lm | RAL 9006 white aluminium | Oktalite_Alu_RAL_9006 | Oktalite_Canilo_WH2700 | 32 VA | 10161686 | 10147501 | 3395 lm |
| CANILO  3P 05 LED4000-827 FL-c ETDD 03 | 32 VA | Flood | 82 | clear | CANILO_LED IQ_FL.ies | LED IQ | 2700 K | LED IQ | 4000 lm | RAL 9006 white aluminium | Oktalite_Alu_RAL_9006 | Oktalite_Canilo_WH2700 | 32 VA | 10161686 | 10127064 | 3395 lm |
| CANILO  3P 05 LED4000-827 FL  ETDD 03 | 32 VA | Flood | 82 | without | CANILO_LED IQ_FL.ies | LED IQ | 2700 K | LED IQ | 4000 lm | RAL 9006 white aluminium | Oktalite_Alu_RAL_9006 | Oktalite_Canilo_WH2700 | 32 VA | 10161686 | 10125196 | 3395 lm |
| CANILO  3P 05 LED4000-827 MF-c ETDD 03 | 32 VA | Medium Flood | 82 | clear | CANILO_LED IQ_MF.ies | LED IQ | 2700 K | LED IQ | 4000 lm | RAL 9006 white aluminium | Oktalite_Alu_RAL_9006 | Oktalite_Canilo_WH2700 | 32 VA | 10161686 | 10127063 | 3395 lm |
| CANILO  3P 05 LED4000-827 MF  ETDD 03 | 32 VA | Medium Flood | 82 | without | CANILO_LED IQ_MF.ies | LED IQ | 2700 K | LED IQ | 4000 lm | RAL 9006 white aluminium | Oktalite_Alu_RAL_9006 | Oktalite_Canilo_WH2700 | 32 VA | 10161686 | 10125193 | 3395 lm |
| CANILO  3P 05 LED4000-827 SP-c ETDD 03 | 32 VA | Spot | 82 | clear | CANILO_LED IQ_SP.ies | LED IQ | 2700 K | LED IQ | 4000 lm | RAL 9006 white aluminium | Oktalite_Alu_RAL_9006 | Oktalite_Canilo_WH2700 | 32 VA | 10161686 | 10127062 | 3395 lm |
| CANILO  3P 05 LED4000-827 SP  ETDD 03 | 32 VA | Spot | 82 | without | CANILO_LED IQ_SP.ies | LED IQ | 2700 K | LED IQ | 4000 lm | RAL 9006 white aluminium | Oktalite_Alu_RAL_9006 | Oktalite_Canilo_WH2700 | 32 VA | 10161686 | 10125190 | 3395 lm |
| CANILO  3P 01 LED4000-827 VFL-c ETDD 01 | 32 VA | Very Wide Flood | 82 | clear | CANILO_LED IQ_VFL.ies | LED IQ | 2700 K | LED IQ | 4000 lm | RAL 9016 traffic white | Oktalite_Alu_RAL_9016 | Oktalite_Canilo_WH2700 | 32 VA | 10161685 | 10147536 | 3395 lm |
| CANILO  3P 01 LED4000-827 VFL  ETDD 01 | 32 VA | Very Wide Flood | 82 | without | CANILO_LED IQ_VFL.ies | LED IQ | 2700 K | LED IQ | 4000 lm | RAL 9016 traffic white | Oktalite_Alu_RAL_9016 | Oktalite_Canilo_WH2700 | 32 VA | 10161685 | 10147502 | 3395 lm |
| CANILO  3P 01 LED4000-827 WFL-c ETDD 01 | 32 VA | Wide Flood | 82 | clear | CANILO_LED IQ_WFL.ies | LED IQ | 2700 K | LED IQ | 4000 lm | RAL 9016 traffic white | Oktalite_Alu_RAL_9016 | Oktalite_Canilo_WH2700 | 32 VA | 10161685 | 10147535 | 3395 lm |
| CANILO  3P 01 LED4000-827 WFL  ETDD 01 | 32 VA | Wide Flood | 82 | without | CANILO_LED IQ_WFL.ies | LED IQ | 2700 K | LED IQ | 4000 lm | RAL 9016 traffic white | Oktalite_Alu_RAL_9016 | Oktalite_Canilo_WH2700 | 32 VA | 10161685 | 10147501 | 3395 lm |
| CANILO  3P 01 LED4000-827 FL-c ETDD 01 | 32 VA | Flood | 82 | clear | CANILO_LED IQ_FL.ies | LED IQ | 2700 K | LED IQ | 4000 lm | RAL 9016 traffic white | Oktalite_Alu_RAL_9016 | Oktalite_Canilo_WH2700 | 32 VA | 10161685 | 10127064 | 3395 lm |
| CANILO  3P 01 LED4000-827 FL  ETDD 01 | 32 VA | Flood | 82 | without | CANILO_LED IQ_FL.ies | LED IQ | 2700 K | LED IQ | 4000 lm | RAL 9016 traffic white | Oktalite_Alu_RAL_9016 | Oktalite_Canilo_WH2700 | 32 VA | 10161685 | 10125196 | 3395 lm |
| CANILO  3P 01 LED4000-827 MF-c ETDD 01 | 32 VA | Medium Flood | 82 | clear | CANILO_LED IQ_MF.ies | LED IQ | 2700 K | LED IQ | 4000 lm | RAL 9016 traffic white | Oktalite_Alu_RAL_9016 | Oktalite_Canilo_WH2700 | 32 VA | 10161685 | 10127063 | 3395 lm |
| CANILO  3P 01 LED4000-827 MF  ETDD 01 | 32 VA | Medium Flood | 82 | without | CANILO_LED IQ_MF.ies | LED IQ | 2700 K | LED IQ | 4000 lm | RAL 9016 traffic white | Oktalite_Alu_RAL_9016 | Oktalite_Canilo_WH2700 | 32 VA | 10161685 | 10125193 | 3395 lm |
| CANILO  3P 01 LED4000-827 SP-c ETDD 01 | 32 VA | Spot | 82 | clear | CANILO_LED IQ_SP.ies | LED IQ | 2700 K | LED IQ | 4000 lm | RAL 9016 traffic white | Oktalite_Alu_RAL_9016 | Oktalite_Canilo_WH2700 | 32 VA | 10161685 | 10127062 | 3395 lm |
| CANILO  3P 01 LED4000-827 SP  ETDD 01 | 32 VA | Spot | 82 | without | CANILO_LED IQ_SP.ies | LED IQ | 2700 K | LED IQ | 4000 lm | RAL 9016 traffic white | Oktalite_Alu_RAL_9016 | Oktalite_Canilo_WH2700 | 32 VA | 10161685 | 10125190 | 3395 lm |
| CANILO  3P 05 LED1500-M VFL-c ET 05 | 24 VA | Very Wide Flood | - | clear | CANILO_LED_VFL.ies | LED | M | LED | 1500 lm | RAL 9005 jet black | Oktalite_Alu_RAL_9005 | Oktalite_Canilo_WH3100 | 24 VA | 10161293 | 10147536 | 1500 lm |
| CANILO  3P 05 LED1500-M VFL  ET 05 | 24 VA | Very Wide Flood | - | without | CANILO_LED_VFL.ies | LED | M | LED | 1500 lm | RAL 9005 jet black | Oktalite_Alu_RAL_9005 | Oktalite_Canilo_WH3100 | 24 VA | 10161293 | 10147502 | 1500 lm |
| CANILO  3P 05 LED1500-M WFL-c ET 05 | 24 VA | Wide Flood | - | clear | CANILO_LED_WFL.ies | LED | M | LED | 1500 lm | RAL 9005 jet black | Oktalite_Alu_RAL_9005 | Oktalite_Canilo_WH3100 | 24 VA | 10161293 | 10147535 | 1500 lm |
| CANILO  3P 05 LED1500-M WFL  ET 05 | 24 VA | Wide Flood | - | without | CANILO_LED_WFL.ies | LED | M | LED | 1500 lm | RAL 9005 jet black | Oktalite_Alu_RAL_9005 | Oktalite_Canilo_WH3100 | 24 VA | 10161293 | 10147501 | 1500 lm |
| CANILO  3P 05 LED1500-M FL-c ET 05 | 24 VA | Flood | - | clear | CANILO_LED_FL.ies | LED | M | LED | 1500 lm | RAL 9005 jet black | Oktalite_Alu_RAL_9005 | Oktalite_Canilo_WH3100 | 24 VA | 10161293 | 10127064 | 1500 lm |
| CANILO  3P 05 LED1500-M FL  ET 05 | 24 VA | Flood | - | without | CANILO_LED_FL.ies | LED | M | LED | 1500 lm | RAL 9005 jet black | Oktalite_Alu_RAL_9005 | Oktalite_Canilo_WH3100 | 24 VA | 10161293 | 10125196 | 1500 lm |
| CANILO  3P 05 LED1500-M MF-c ET 05 | 24 VA | Medium Flood | - | clear | CANILO_LED_MF.ies | LED | M | LED | 1500 lm | RAL 9005 jet black | Oktalite_Alu_RAL_9005 | Oktalite_Canilo_WH3100 | 24 VA | 10161293 | 10127063 | 1500 lm |
| CANILO  3P 05 LED1500-M MF  ET 05 | 24 VA | Medium Flood | - | without | CANILO_LED_MF.ies | LED | M | LED | 1500 lm | RAL 9005 jet black | Oktalite_Alu_RAL_9005 | Oktalite_Canilo_WH3100 | 24 VA | 10161293 | 10125193 | 1500 lm |
| CANILO  3P 05 LED1500-M SP-c ET 05 | 24 VA | Spot | - | clear | CANILO_LED_SP.ies | LED | M | LED | 1500 lm | RAL 9005 jet black | Oktalite_Alu_RAL_9005 | Oktalite_Canilo_WH3100 | 24 VA | 10161293 | 10127062 | 1500 lm |
| CANILO  3P 05 LED1500-M SP  ET 05 | 24 VA | Spot | - | without | CANILO_LED_SP.ies | LED | M | LED | 1500 lm | RAL 9005 jet black | Oktalite_Alu_RAL_9005 | Oktalite_Canilo_WH3100 | 24 VA | 10161293 | 10125190 | 1500 lm |
| CANILO  3P 05 LED1500-M VFL-c ET 03 | 24 VA | Very Wide Flood | - | clear | CANILO_LED_VFL.ies | LED | M | LED | 1500 lm | RAL 9006 white aluminium | Oktalite_Alu_RAL_9006 | Oktalite_Canilo_WH3100 | 24 VA | 10161292 | 10147536 | 1500 lm |
| CANILO  3P 05 LED1500-M VFL  ET 03 | 24 VA | Very Wide Flood | - | without | CANILO_LED_VFL.ies | LED | M | LED | 1500 lm | RAL 9006 white aluminium | Oktalite_Alu_RAL_9006 | Oktalite_Canilo_WH3100 | 24 VA | 10161292 | 10147502 | 1500 lm |
| CANILO  3P 05 LED1500-M WFL-c ET 03 | 24 VA | Wide Flood | - | clear | CANILO_LED_WFL.ies | LED | M | LED | 1500 lm | RAL 9006 white aluminium | Oktalite_Alu_RAL_9006 | Oktalite_Canilo_WH3100 | 24 VA | 10161292 | 10147535 | 1500 lm |
| CANILO  3P 05 LED1500-M WFL  ET 03 | 24 VA | Wide Flood | - | without | CANILO_LED_WFL.ies | LED | M | LED | 1500 lm | RAL 9006 white aluminium | Oktalite_Alu_RAL_9006 | Oktalite_Canilo_WH3100 | 24 VA | 10161292 | 10147501 | 1500 lm |
| CANILO  3P 05 LED1500-M FL-c ET 03 | 24 VA | Flood | - | clear | CANILO_LED_FL.ies | LED | M | LED | 1500 lm | RAL 9006 white aluminium | Oktalite_Alu_RAL_9006 | Oktalite_Canilo_WH3100 | 24 VA | 10161292 | 10127064 | 1500 lm |
| CANILO  3P 05 LED1500-M FL  ET 03 | 24 VA | Flood | - | without | CANILO_LED_FL.ies | LED | M | LED | 1500 lm | RAL 9006 white aluminium | Oktalite_Alu_RAL_9006 | Oktalite_Canilo_WH3100 | 24 VA | 10161292 | 10125196 | 1500 lm |
| CANILO  3P 05 LED1500-M MF-c ET 03 | 24 VA | Medium Flood | - | clear | CANILO_LED_MF.ies | LED | M | LED | 1500 lm | RAL 9006 white aluminium | Oktalite_Alu_RAL_9006 | Oktalite_Canilo_WH3100 | 24 VA | 10161292 | 10127063 | 1500 lm |
| CANILO  3P 05 LED1500-M MF  ET 03 | 24 VA | Medium Flood | - | without | CANILO_LED_MF.ies | LED | M | LED | 1500 lm | RAL 9006 white aluminium | Oktalite_Alu_RAL_9006 | Oktalite_Canilo_WH3100 | 24 VA | 10161292 | 10125193 | 1500 lm |
| CANILO  3P 05 LED1500-M SP-c ET 03 | 24 VA | Spot | - | clear | CANILO_LED_SP.ies | LED | M | LED | 1500 lm | RAL 9006 white aluminium | Oktalite_Alu_RAL_9006 | Oktalite_Canilo_WH3100 | 24 VA | 10161292 | 10127062 | 1500 lm |
| CANILO  3P 05 LED1500-M SP  ET 03 | 24 VA | Spot | - | without | CANILO_LED_SP.ies | LED | M | LED | 1500 lm | RAL 9006 white aluminium | Oktalite_Alu_RAL_9006 | Oktalite_Canilo_WH3100 | 24 VA | 10161292 | 10125190 | 1500 lm |
| CANILO  3P 01 LED1500-M VFL-c ET 01 | 24 VA | Very Wide Flood | - | clear | CANILO_LED_VFL.ies | LED | M | LED | 1500 lm | RAL 9016 traffic white | Oktalite_Alu_RAL_9016 | Oktalite_Canilo_WH3100 | 24 VA | 10161291 | 10147536 | 1500 lm |
| CANILO  3P 01 LED1500-M VFL  ET 01 | 24 VA | Very Wide Flood | - | without | CANILO_LED_VFL.ies | LED | M | LED | 1500 lm | RAL 9016 traffic white | Oktalite_Alu_RAL_9016 | Oktalite_Canilo_WH3100 | 24 VA | 10161291 | 10147502 | 1500 lm |
| CANILO  3P 01 LED1500-M WFL-c ET 01 | 24 VA | Wide Flood | - | clear | CANILO_LED_WFL.ies | LED | M | LED | 1500 lm | RAL 9016 traffic white | Oktalite_Alu_RAL_9016 | Oktalite_Canilo_WH3100 | 24 VA | 10161291 | 10147535 | 1500 lm |
| CANILO  3P 01 LED1500-M WFL  ET 01 | 24 VA | Wide Flood | - | without | CANILO_LED_WFL.ies | LED | M | LED | 1500 lm | RAL 9016 traffic white | Oktalite_Alu_RAL_9016 | Oktalite_Canilo_WH3100 | 24 VA | 10161291 | 10147501 | 1500 lm |
| CANILO  3P 01 LED1500-M FL-c ET 01 | 24 VA | Flood | - | clear | CANILO_LED_FL.ies | LED | M | LED | 1500 lm | RAL 9016 traffic white | Oktalite_Alu_RAL_9016 | Oktalite_Canilo_WH3100 | 24 VA | 10161291 | 10127064 | 1500 lm |
| CANILO  3P 01 LED1500-M FL  ET 01 | 24 VA | Flood | - | without | CANILO_LED_FL.ies | LED | M | LED | 1500 lm | RAL 9016 traffic white | Oktalite_Alu_RAL_9016 | Oktalite_Canilo_WH3100 | 24 VA | 10161291 | 10125196 | 1500 lm |
| CANILO  3P 01 LED1500-M MF-c ET 01 | 24 VA | Medium Flood | - | clear | CANILO_LED_MF.ies | LED | M | LED | 1500 lm | RAL 9016 traffic white | Oktalite_Alu_RAL_9016 | Oktalite_Canilo_WH3100 | 24 VA | 10161291 | 10127063 | 1500 lm |
| CANILO  3P 01 LED1500-M MF  ET 01 | 24 VA | Medium Flood | - | without | CANILO_LED_MF.ies | LED | M | LED | 1500 lm | RAL 9016 traffic white | Oktalite_Alu_RAL_9016 | Oktalite_Canilo_WH3100 | 24 VA | 10161291 | 10125193 | 1500 lm |
| CANILO  3P 01 LED1500-M SP-c ET 01 | 24 VA | Spot | - | clear | CANILO_LED_SP.ies | LED | M | LED | 1500 lm | RAL 9016 traffic white | Oktalite_Alu_RAL_9016 | Oktalite_Canilo_WH3100 | 24 VA | 10161291 | 10127062 | 1500 lm |
| CANILO  3P 01 LED1500-M SP  ET 01 | 24 VA | Spot | - | without | CANILO_LED_SP.ies | LED | M | LED | 1500 lm | RAL 9016 traffic white | Oktalite_Alu_RAL_9016 | Oktalite_Canilo_WH3100 | 24 VA | 10161291 | 10125190 | 1500 lm |
| CANILO  3P 05 LED1500-M+F VFL-c ET 05 | 24 VA | Very Wide Flood | - | clear | CANILO_LED_VFL.ies | LED | M+F | LED | 1500 lm | RAL 9005 jet black | Oktalite_Alu_RAL_9005 | Oktalite_Canilo_WH3100 | 24 VA | 10161302 | 10147536 | 1415 lm |
| CANILO  3P 05 LED1500-M+F VFL  ET 05 | 24 VA | Very Wide Flood | - | without | CANILO_LED_VFL.ies | LED | M+F | LED | 1500 lm | RAL 9005 jet black | Oktalite_Alu_RAL_9005 | Oktalite_Canilo_WH3100 | 24 VA | 10161302 | 10147502 | 1415 lm |
| CANILO  3P 05 LED1500-M+F WFL-c ET 05 | 24 VA | Wide Flood | - | clear | CANILO_LED_WFL.ies | LED | M+F | LED | 1500 lm | RAL 9005 jet black | Oktalite_Alu_RAL_9005 | Oktalite_Canilo_WH3100 | 24 VA | 10161302 | 10147535 | 1415 lm |
| CANILO  3P 05 LED1500-M+F WFL  ET 05 | 24 VA | Wide Flood | - | without | CANILO_LED_WFL.ies | LED | M+F | LED | 1500 lm | RAL 9005 jet black | Oktalite_Alu_RAL_9005 | Oktalite_Canilo_WH3100 | 24 VA | 10161302 | 10147501 | 1415 lm |
| CANILO  3P 05 LED1500-M+F FL-c ET 05 | 24 VA | Flood | - | clear | CANILO_LED_FL.ies | LED | M+F | LED | 1500 lm | RAL 9005 jet black | Oktalite_Alu_RAL_9005 | Oktalite_Canilo_WH3100 | 24 VA | 10161302 | 10127064 | 1415 lm |
| CANILO  3P 05 LED1500-M+F FL  ET 05 | 24 VA | Flood | - | without | CANILO_LED_FL.ies | LED | M+F | LED | 1500 lm | RAL 9005 jet black | Oktalite_Alu_RAL_9005 | Oktalite_Canilo_WH3100 | 24 VA | 10161302 | 10125196 | 1415 lm |
| CANILO  3P 05 LED1500-M+F MF-c ET 05 | 24 VA | Medium Flood | - | clear | CANILO_LED_MF.ies | LED | M+F | LED | 1500 lm | RAL 9005 jet black | Oktalite_Alu_RAL_9005 | Oktalite_Canilo_WH3100 | 24 VA | 10161302 | 10127063 | 1415 lm |
| CANILO  3P 05 LED1500-M+F MF  ET 05 | 24 VA | Medium Flood | - | without | CANILO_LED_MF.ies | LED | M+F | LED | 1500 lm | RAL 9005 jet black | Oktalite_Alu_RAL_9005 | Oktalite_Canilo_WH3100 | 24 VA | 10161302 | 10125193 | 1415 lm |
| CANILO  3P 05 LED1500-M+F SP-c ET 05 | 24 VA | Spot | - | clear | CANILO_LED_SP.ies | LED | M+F | LED | 1500 lm | RAL 9005 jet black | Oktalite_Alu_RAL_9005 | Oktalite_Canilo_WH3100 | 24 VA | 10161302 | 10127062 | 1415 lm |
| CANILO  3P 05 LED1500-M+F SP  ET 05 | 24 VA | Spot | - | without | CANILO_LED_SP.ies | LED | M+F | LED | 1500 lm | RAL 9005 jet black | Oktalite_Alu_RAL_9005 | Oktalite_Canilo_WH3100 | 24 VA | 10161302 | 10125190 | 1415 lm |
| CANILO  3P 05 LED1500-M+F VFL-c ET 03 | 24 VA | Very Wide Flood | - | clear | CANILO_LED_VFL.ies | LED | M+F | LED | 1500 lm | RAL 9006 white aluminium | Oktalite_Alu_RAL_9006 | Oktalite_Canilo_WH3100 | 24 VA | 10161301 | 10147536 | 1415 lm |
| CANILO  3P 05 LED1500-M+F VFL  ET 03 | 24 VA | Very Wide Flood | - | without | CANILO_LED_VFL.ies | LED | M+F | LED | 1500 lm | RAL 9006 white aluminium | Oktalite_Alu_RAL_9006 | Oktalite_Canilo_WH3100 | 24 VA | 10161301 | 10147502 | 1415 lm |
| CANILO  3P 05 LED1500-M+F WFL-c ET 03 | 24 VA | Wide Flood | - | clear | CANILO_LED_WFL.ies | LED | M+F | LED | 1500 lm | RAL 9006 white aluminium | Oktalite_Alu_RAL_9006 | Oktalite_Canilo_WH3100 | 24 VA | 10161301 | 10147535 | 1415 lm |
| CANILO  3P 05 LED1500-M+F WFL  ET 03 | 24 VA | Wide Flood | - | without | CANILO_LED_WFL.ies | LED | M+F | LED | 1500 lm | RAL 9006 white aluminium | Oktalite_Alu_RAL_9006 | Oktalite_Canilo_WH3100 | 24 VA | 10161301 | 10147501 | 1415 lm |
| CANILO  3P 05 LED1500-M+F FL-c ET 03 | 24 VA | Flood | - | clear | CANILO_LED_FL.ies | LED | M+F | LED | 1500 lm | RAL 9006 white aluminium | Oktalite_Alu_RAL_9006 | Oktalite_Canilo_WH3100 | 24 VA | 10161301 | 10127064 | 1415 lm |
| CANILO  3P 05 LED1500-M+F FL  ET 03 | 24 VA | Flood | - | without | CANILO_LED_FL.ies | LED | M+F | LED | 1500 lm | RAL 9006 white aluminium | Oktalite_Alu_RAL_9006 | Oktalite_Canilo_WH3100 | 24 VA | 10161301 | 10125196 | 1415 lm |
| CANILO  3P 05 LED1500-M+F MF-c ET 03 | 24 VA | Medium Flood | - | clear | CANILO_LED_MF.ies | LED | M+F | LED | 1500 lm | RAL 9006 white aluminium | Oktalite_Alu_RAL_9006 | Oktalite_Canilo_WH3100 | 24 VA | 10161301 | 10127063 | 1415 lm |
| CANILO  3P 05 LED1500-M+F MF  ET 03 | 24 VA | Medium Flood | - | without | CANILO_LED_MF.ies | LED | M+F | LED | 1500 lm | RAL 9006 white aluminium | Oktalite_Alu_RAL_9006 | Oktalite_Canilo_WH3100 | 24 VA | 10161301 | 10125193 | 1415 lm |
| CANILO  3P 05 LED1500-M+F SP-c ET 03 | 24 VA | Spot | - | clear | CANILO_LED_SP.ies | LED | M+F | LED | 1500 lm | RAL 9006 white aluminium | Oktalite_Alu_RAL_9006 | Oktalite_Canilo_WH3100 | 24 VA | 10161301 | 10127062 | 1415 lm |
| CANILO  3P 05 LED1500-M+F SP  ET 03 | 24 VA | Spot | - | without | CANILO_LED_SP.ies | LED | M+F | LED | 1500 lm | RAL 9006 white aluminium | Oktalite_Alu_RAL_9006 | Oktalite_Canilo_WH3100 | 24 VA | 10161301 | 10125190 | 1415 lm |
| CANILO  3P 01 LED1500-M+F VFL-c ET 01 | 24 VA | Very Wide Flood | - | clear | CANILO_LED_VFL.ies | LED | M+F | LED | 1500 lm | RAL 9016 traffic white | Oktalite_Alu_RAL_9016 | Oktalite_Canilo_WH3100 | 24 VA | 10161300 | 10147536 | 1415 lm |
| CANILO  3P 01 LED1500-M+F VFL  ET 01 | 24 VA | Very Wide Flood | - | without | CANILO_LED_VFL.ies | LED | M+F | LED | 1500 lm | RAL 9016 traffic white | Oktalite_Alu_RAL_9016 | Oktalite_Canilo_WH3100 | 24 VA | 10161300 | 10147502 | 1415 lm |
| CANILO  3P 01 LED1500-M+F WFL-c ET 01 | 24 VA | Wide Flood | - | clear | CANILO_LED_WFL.ies | LED | M+F | LED | 1500 lm | RAL 9016 traffic white | Oktalite_Alu_RAL_9016 | Oktalite_Canilo_WH3100 | 24 VA | 10161300 | 10147535 | 1415 lm |
| CANILO  3P 01 LED1500-M+F WFL  ET 01 | 24 VA | Wide Flood | - | without | CANILO_LED_WFL.ies | LED | M+F | LED | 1500 lm | RAL 9016 traffic white | Oktalite_Alu_RAL_9016 | Oktalite_Canilo_WH3100 | 24 VA | 10161300 | 10147501 | 1415 lm |
| CANILO  3P 01 LED1500-M+F FL-c ET 01 | 24 VA | Flood | - | clear | CANILO_LED_FL.ies | LED | M+F | LED | 1500 lm | RAL 9016 traffic white | Oktalite_Alu_RAL_9016 | Oktalite_Canilo_WH3100 | 24 VA | 10161300 | 10127064 | 1415 lm |
| CANILO  3P 01 LED1500-M+F FL  ET 01 | 24 VA | Flood | - | without | CANILO_LED_FL.ies | LED | M+F | LED | 1500 lm | RAL 9016 traffic white | Oktalite_Alu_RAL_9016 | Oktalite_Canilo_WH3100 | 24 VA | 10161300 | 10125196 | 1415 lm |
| CANILO  3P 01 LED1500-M+F MF-c ET 01 | 24 VA | Medium Flood | - | clear | CANILO_LED_MF.ies | LED | M+F | LED | 1500 lm | RAL 9016 traffic white | Oktalite_Alu_RAL_9016 | Oktalite_Canilo_WH3100 | 24 VA | 10161300 | 10127063 | 1415 lm |
| CANILO  3P 01 LED1500-M+F MF  ET 01 | 24 VA | Medium Flood | - | without | CANILO_LED_MF.ies | LED | M+F | LED | 1500 lm | RAL 9016 traffic white | Oktalite_Alu_RAL_9016 | Oktalite_Canilo_WH3100 | 24 VA | 10161300 | 10125193 | 1415 lm |
| CANILO  3P 01 LED1500-M+F SP-c ET 01 | 24 VA | Spot | - | clear | CANILO_LED_SP.ies | LED | M+F | LED | 1500 lm | RAL 9016 traffic white | Oktalite_Alu_RAL_9016 | Oktalite_Canilo_WH3100 | 24 VA | 10161300 | 10127062 | 1415 lm |
| CANILO  3P 01 LED1500-M+F SP  ET 01 | 24 VA | Spot | - | without | CANILO_LED_SP.ies | LED | M+F | LED | 1500 lm | RAL 9016 traffic white | Oktalite_Alu_RAL_9016 | Oktalite_Canilo_WH3100 | 24 VA | 10161300 | 10125190 | 1415 lm |
| CANILO  3P 05 LED2000-M VFL-c ET 05 | 31 VA | Very Wide Flood | - | clear | CANILO_LED_VFL.ies | LED | M | LED | 2000 lm | RAL 9005 jet black | Oktalite_Alu_RAL_9005 | Oktalite_Canilo_WH3100 | 31 VA | 10161296 | 10147536 | 1890 lm |
| CANILO  3P 05 LED2000-M VFL  ET 05 | 31 VA | Very Wide Flood | - | without | CANILO_LED_VFL.ies | LED | M | LED | 2000 lm | RAL 9005 jet black | Oktalite_Alu_RAL_9005 | Oktalite_Canilo_WH3100 | 31 VA | 10161296 | 10147502 | 1890 lm |
| CANILO  3P 05 LED2000-M WFL-c ET 05 | 31 VA | Wide Flood | - | clear | CANILO_LED_WFL.ies | LED | M | LED | 2000 lm | RAL 9005 jet black | Oktalite_Alu_RAL_9005 | Oktalite_Canilo_WH3100 | 31 VA | 10161296 | 10147535 | 1890 lm |
| CANILO  3P 05 LED2000-M WFL  ET 05 | 31 VA | Wide Flood | - | without | CANILO_LED_WFL.ies | LED | M | LED | 2000 lm | RAL 9005 jet black | Oktalite_Alu_RAL_9005 | Oktalite_Canilo_WH3100 | 31 VA | 10161296 | 10147501 | 1890 lm |
| CANILO  3P 05 LED2000-M FL-c ET 05 | 31 VA | Flood | - | clear | CANILO_LED_FL.ies | LED | M | LED | 2000 lm | RAL 9005 jet black | Oktalite_Alu_RAL_9005 | Oktalite_Canilo_WH3100 | 31 VA | 10161296 | 10127064 | 1890 lm |
| CANILO  3P 05 LED2000-M FL  ET 05 | 31 VA | Flood | - | without | CANILO_LED_FL.ies | LED | M | LED | 2000 lm | RAL 9005 jet black | Oktalite_Alu_RAL_9005 | Oktalite_Canilo_WH3100 | 31 VA | 10161296 | 10125196 | 1890 lm |
| CANILO  3P 05 LED2000-M MF-c ET 05 | 31 VA | Medium Flood | - | clear | CANILO_LED_MF.ies | LED | M | LED | 2000 lm | RAL 9005 jet black | Oktalite_Alu_RAL_9005 | Oktalite_Canilo_WH3100 | 31 VA | 10161296 | 10127063 | 1890 lm |
| CANILO  3P 05 LED2000-M MF  ET 05 | 31 VA | Medium Flood | - | without | CANILO_LED_MF.ies | LED | M | LED | 2000 lm | RAL 9005 jet black | Oktalite_Alu_RAL_9005 | Oktalite_Canilo_WH3100 | 31 VA | 10161296 | 10125193 | 1890 lm |
| CANILO  3P 05 LED2000-M SP-c ET 05 | 31 VA | Spot | - | clear | CANILO_LED_SP.ies | LED | M | LED | 2000 lm | RAL 9005 jet black | Oktalite_Alu_RAL_9005 | Oktalite_Canilo_WH3100 | 31 VA | 10161296 | 10127062 | 1890 lm |
| CANILO  3P 05 LED2000-M SP  ET 05 | 31 VA | Spot | - | without | CANILO_LED_SP.ies | LED | M | LED | 2000 lm | RAL 9005 jet black | Oktalite_Alu_RAL_9005 | Oktalite_Canilo_WH3100 | 31 VA | 10161296 | 10125190 | 1890 lm |
| CANILO  3P 05 LED2000-M VFL-c ET 03 | 31 VA | Very Wide Flood | - | clear | CANILO_LED_VFL.ies | LED | M | LED | 2000 lm | RAL 9006 white aluminium | Oktalite_Alu_RAL_9006 | Oktalite_Canilo_WH3100 | 31 VA | 10161295 | 10147536 | 1890 lm |
| CANILO  3P 05 LED2000-M VFL  ET 03 | 31 VA | Very Wide Flood | - | without | CANILO_LED_VFL.ies | LED | M | LED | 2000 lm | RAL 9006 white aluminium | Oktalite_Alu_RAL_9006 | Oktalite_Canilo_WH3100 | 31 VA | 10161295 | 10147502 | 1890 lm |
| CANILO  3P 05 LED2000-M WFL-c ET 03 | 31 VA | Wide Flood | - | clear | CANILO_LED_WFL.ies | LED | M | LED | 2000 lm | RAL 9006 white aluminium | Oktalite_Alu_RAL_9006 | Oktalite_Canilo_WH3100 | 31 VA | 10161295 | 10147535 | 1890 lm |
| CANILO  3P 05 LED2000-M WFL  ET 03 | 31 VA | Wide Flood | - | without | CANILO_LED_WFL.ies | LED | M | LED | 2000 lm | RAL 9006 white aluminium | Oktalite_Alu_RAL_9006 | Oktalite_Canilo_WH3100 | 31 VA | 10161295 | 10147501 | 1890 lm |
| CANILO  3P 05 LED2000-M FL-c ET 03 | 31 VA | Flood | - | clear | CANILO_LED_FL.ies | LED | M | LED | 2000 lm | RAL 9006 white aluminium | Oktalite_Alu_RAL_9006 | Oktalite_Canilo_WH3100 | 31 VA | 10161295 | 10127064 | 1890 lm |
| CANILO  3P 05 LED2000-M FL  ET 03 | 31 VA | Flood | - | without | CANILO_LED_FL.ies | LED | M | LED | 2000 lm | RAL 9006 white aluminium | Oktalite_Alu_RAL_9006 | Oktalite_Canilo_WH3100 | 31 VA | 10161295 | 10125196 | 1890 lm |
| CANILO  3P 05 LED2000-M MF-c ET 03 | 31 VA | Medium Flood | - | clear | CANILO_LED_MF.ies | LED | M | LED | 2000 lm | RAL 9006 white aluminium | Oktalite_Alu_RAL_9006 | Oktalite_Canilo_WH3100 | 31 VA | 10161295 | 10127063 | 1890 lm |
| CANILO  3P 05 LED2000-M MF  ET 03 | 31 VA | Medium Flood | - | without | CANILO_LED_MF.ies | LED | M | LED | 2000 lm | RAL 9006 white aluminium | Oktalite_Alu_RAL_9006 | Oktalite_Canilo_WH3100 | 31 VA | 10161295 | 10125193 | 1890 lm |
| CANILO  3P 05 LED2000-M SP-c ET 03 | 31 VA | Spot | - | clear | CANILO_LED_SP.ies | LED | M | LED | 2000 lm | RAL 9006 white aluminium | Oktalite_Alu_RAL_9006 | Oktalite_Canilo_WH3100 | 31 VA | 10161295 | 10127062 | 1890 lm |
| CANILO  3P 05 LED2000-M SP  ET 03 | 31 VA | Spot | - | without | CANILO_LED_SP.ies | LED | M | LED | 2000 lm | RAL 9006 white aluminium | Oktalite_Alu_RAL_9006 | Oktalite_Canilo_WH3100 | 31 VA | 10161295 | 10125190 | 1890 lm |
| CANILO  3P 01 LED2000-M VFL-c ET 01 | 31 VA | Very Wide Flood | - | clear | CANILO_LED_VFL.ies | LED | M | LED | 2000 lm | RAL 9016 traffic white | Oktalite_Alu_RAL_9016 | Oktalite_Canilo_WH3100 | 31 VA | 10161294 | 10147536 | 1890 lm |
| CANILO  3P 01 LED2000-M VFL  ET 01 | 31 VA | Very Wide Flood | - | without | CANILO_LED_VFL.ies | LED | M | LED | 2000 lm | RAL 9016 traffic white | Oktalite_Alu_RAL_9016 | Oktalite_Canilo_WH3100 | 31 VA | 10161294 | 10147502 | 1890 lm |
| CANILO  3P 01 LED2000-M WFL-c ET 01 | 31 VA | Wide Flood | - | clear | CANILO_LED_WFL.ies | LED | M | LED | 2000 lm | RAL 9016 traffic white | Oktalite_Alu_RAL_9016 | Oktalite_Canilo_WH3100 | 31 VA | 10161294 | 10147535 | 1890 lm |
| CANILO  3P 01 LED2000-M WFL  ET 01 | 31 VA | Wide Flood | - | without | CANILO_LED_WFL.ies | LED | M | LED | 2000 lm | RAL 9016 traffic white | Oktalite_Alu_RAL_9016 | Oktalite_Canilo_WH3100 | 31 VA | 10161294 | 10147501 | 1890 lm |
| CANILO  3P 01 LED2000-M FL-c ET 01 | 31 VA | Flood | - | clear | CANILO_LED_FL.ies | LED | M | LED | 2000 lm | RAL 9016 traffic white | Oktalite_Alu_RAL_9016 | Oktalite_Canilo_WH3100 | 31 VA | 10161294 | 10127064 | 1890 lm |
| CANILO  3P 01 LED2000-M FL  ET 01 | 31 VA | Flood | - | without | CANILO_LED_FL.ies | LED | M | LED | 2000 lm | RAL 9016 traffic white | Oktalite_Alu_RAL_9016 | Oktalite_Canilo_WH3100 | 31 VA | 10161294 | 10125196 | 1890 lm |
| CANILO  3P 01 LED2000-M MF-c ET 01 | 31 VA | Medium Flood | - | clear | CANILO_LED_MF.ies | LED | M | LED | 2000 lm | RAL 9016 traffic white | Oktalite_Alu_RAL_9016 | Oktalite_Canilo_WH3100 | 31 VA | 10161294 | 10127063 | 1890 lm |
| CANILO  3P 01 LED2000-M MF  ET 01 | 31 VA | Medium Flood | - | without | CANILO_LED_MF.ies | LED | M | LED | 2000 lm | RAL 9016 traffic white | Oktalite_Alu_RAL_9016 | Oktalite_Canilo_WH3100 | 31 VA | 10161294 | 10125193 | 1890 lm |
| CANILO  3P 01 LED2000-M SP-c ET 01 | 31 VA | Spot | - | clear | CANILO_LED_SP.ies | LED | M | LED | 2000 lm | RAL 9016 traffic white | Oktalite_Alu_RAL_9016 | Oktalite_Canilo_WH3100 | 31 VA | 10161294 | 10127062 | 1890 lm |
| CANILO  3P 01 LED2000-M SP  ET 01 | 31 VA | Spot | - | without | CANILO_LED_SP.ies | LED | M | LED | 2000 lm | RAL 9016 traffic white | Oktalite_Alu_RAL_9016 | Oktalite_Canilo_WH3100 | 31 VA | 10161294 | 10125190 | 1890 lm |
| CANILO  3P 05 LED2000-M+F VFL-c ET 05 | 31 VA | Very Wide Flood | - | clear | CANILO_LED_VFL.ies | LED | M+F | LED | 2000 lm | RAL 9005 jet black | Oktalite_Alu_RAL_9005 | Oktalite_Canilo_WH3100 | 31 VA | 10161305 | 10147536 | 1785 lm |
| CANILO  3P 05 LED2000-M+F VFL  ET 05 | 31 VA | Very Wide Flood | - | without | CANILO_LED_VFL.ies | LED | M+F | LED | 2000 lm | RAL 9005 jet black | Oktalite_Alu_RAL_9005 | Oktalite_Canilo_WH3100 | 31 VA | 10161305 | 10147502 | 1785 lm |
| CANILO  3P 05 LED2000-M+F WFL-c ET 05 | 31 VA | Wide Flood | - | clear | CANILO_LED_WFL.ies | LED | M+F | LED | 2000 lm | RAL 9005 jet black | Oktalite_Alu_RAL_9005 | Oktalite_Canilo_WH3100 | 31 VA | 10161305 | 10147535 | 1785 lm |
| CANILO  3P 05 LED2000-M+F WFL  ET 05 | 31 VA | Wide Flood | - | without | CANILO_LED_WFL.ies | LED | M+F | LED | 2000 lm | RAL 9005 jet black | Oktalite_Alu_RAL_9005 | Oktalite_Canilo_WH3100 | 31 VA | 10161305 | 10147501 | 1785 lm |
| CANILO  3P 05 LED2000-M+F FL-c ET 05 | 31 VA | Flood | - | clear | CANILO_LED_FL.ies | LED | M+F | LED | 2000 lm | RAL 9005 jet black | Oktalite_Alu_RAL_9005 | Oktalite_Canilo_WH3100 | 31 VA | 10161305 | 10127064 | 1785 lm |
| CANILO  3P 05 LED2000-M+F FL  ET 05 | 31 VA | Flood | - | without | CANILO_LED_FL.ies | LED | M+F | LED | 2000 lm | RAL 9005 jet black | Oktalite_Alu_RAL_9005 | Oktalite_Canilo_WH3100 | 31 VA | 10161305 | 10125196 | 1785 lm |
| CANILO  3P 05 LED2000-M+F MF-c ET 05 | 31 VA | Medium Flood | - | clear | CANILO_LED_MF.ies | LED | M+F | LED | 2000 lm | RAL 9005 jet black | Oktalite_Alu_RAL_9005 | Oktalite_Canilo_WH3100 | 31 VA | 10161305 | 10127063 | 1785 lm |
| CANILO  3P 05 LED2000-M+F MF  ET 05 | 31 VA | Medium Flood | - | without | CANILO_LED_MF.ies | LED | M+F | LED | 2000 lm | RAL 9005 jet black | Oktalite_Alu_RAL_9005 | Oktalite_Canilo_WH3100 | 31 VA | 10161305 | 10125193 | 1785 lm |
| CANILO  3P 05 LED2000-M+F SP-c ET 05 | 31 VA | Spot | - | clear | CANILO_LED_SP.ies | LED | M+F | LED | 2000 lm | RAL 9005 jet black | Oktalite_Alu_RAL_9005 | Oktalite_Canilo_WH3100 | 31 VA | 10161305 | 10127062 | 1785 lm |
| CANILO  3P 05 LED2000-M+F SP  ET 05 | 31 VA | Spot | - | without | CANILO_LED_SP.ies | LED | M+F | LED | 2000 lm | RAL 9005 jet black | Oktalite_Alu_RAL_9005 | Oktalite_Canilo_WH3100 | 31 VA | 10161305 | 10125190 | 1785 lm |
| CANILO  3P 05 LED2000-M+F VFL-c ET 03 | 31 VA | Very Wide Flood | - | clear | CANILO_LED_VFL.ies | LED | M+F | LED | 2000 lm | RAL 9006 white aluminium | Oktalite_Alu_RAL_9006 | Oktalite_Canilo_WH3100 | 31 VA | 10161304 | 10147536 | 1785 lm |
| CANILO  3P 05 LED2000-M+F VFL  ET 03 | 31 VA | Very Wide Flood | - | without | CANILO_LED_VFL.ies | LED | M+F | LED | 2000 lm | RAL 9006 white aluminium | Oktalite_Alu_RAL_9006 | Oktalite_Canilo_WH3100 | 31 VA | 10161304 | 10147502 | 1785 lm |
| CANILO  3P 05 LED2000-M+F WFL-c ET 03 | 31 VA | Wide Flood | - | clear | CANILO_LED_WFL.ies | LED | M+F | LED | 2000 lm | RAL 9006 white aluminium | Oktalite_Alu_RAL_9006 | Oktalite_Canilo_WH3100 | 31 VA | 10161304 | 10147535 | 1785 lm |
| CANILO  3P 05 LED2000-M+F WFL  ET 03 | 31 VA | Wide Flood | - | without | CANILO_LED_WFL.ies | LED | M+F | LED | 2000 lm | RAL 9006 white aluminium | Oktalite_Alu_RAL_9006 | Oktalite_Canilo_WH3100 | 31 VA | 10161304 | 10147501 | 1785 lm |
| CANILO  3P 05 LED2000-M+F FL-c ET 03 | 31 VA | Flood | - | clear | CANILO_LED_FL.ies | LED | M+F | LED | 2000 lm | RAL 9006 white aluminium | Oktalite_Alu_RAL_9006 | Oktalite_Canilo_WH3100 | 31 VA | 10161304 | 10127064 | 1785 lm |
| CANILO  3P 05 LED2000-M+F FL  ET 03 | 31 VA | Flood | - | without | CANILO_LED_FL.ies | LED | M+F | LED | 2000 lm | RAL 9006 white aluminium | Oktalite_Alu_RAL_9006 | Oktalite_Canilo_WH3100 | 31 VA | 10161304 | 10125196 | 1785 lm |
| CANILO  3P 05 LED2000-M+F MF-c ET 03 | 31 VA | Medium Flood | - | clear | CANILO_LED_MF.ies | LED | M+F | LED | 2000 lm | RAL 9006 white aluminium | Oktalite_Alu_RAL_9006 | Oktalite_Canilo_WH3100 | 31 VA | 10161304 | 10127063 | 1785 lm |
| CANILO  3P 05 LED2000-M+F MF  ET 03 | 31 VA | Medium Flood | - | without | CANILO_LED_MF.ies | LED | M+F | LED | 2000 lm | RAL 9006 white aluminium | Oktalite_Alu_RAL_9006 | Oktalite_Canilo_WH3100 | 31 VA | 10161304 | 10125193 | 1785 lm |
| CANILO  3P 05 LED2000-M+F SP-c ET 03 | 31 VA | Spot | - | clear | CANILO_LED_SP.ies | LED | M+F | LED | 2000 lm | RAL 9006 white aluminium | Oktalite_Alu_RAL_9006 | Oktalite_Canilo_WH3100 | 31 VA | 10161304 | 10127062 | 1785 lm |
| CANILO  3P 05 LED2000-M+F SP  ET 03 | 31 VA | Spot | - | without | CANILO_LED_SP.ies | LED | M+F | LED | 2000 lm | RAL 9006 white aluminium | Oktalite_Alu_RAL_9006 | Oktalite_Canilo_WH3100 | 31 VA | 10161304 | 10125190 | 1785 lm |
| CANILO  3P 01 LED2000-M+F VFL-c ET 01 | 31 VA | Very Wide Flood | - | clear | CANILO_LED_VFL.ies | LED | M+F | LED | 2000 lm | RAL 9016 traffic white | Oktalite_Alu_RAL_9016 | Oktalite_Canilo_WH3100 | 31 VA | 10161303 | 10147536 | 1785 lm |
| CANILO  3P 01 LED2000-M+F VFL  ET 01 | 31 VA | Very Wide Flood | - | without | CANILO_LED_VFL.ies | LED | M+F | LED | 2000 lm | RAL 9016 traffic white | Oktalite_Alu_RAL_9016 | Oktalite_Canilo_WH3100 | 31 VA | 10161303 | 10147502 | 1785 lm |
| CANILO  3P 01 LED2000-M+F WFL-c ET 01 | 31 VA | Wide Flood | - | clear | CANILO_LED_WFL.ies | LED | M+F | LED | 2000 lm | RAL 9016 traffic white | Oktalite_Alu_RAL_9016 | Oktalite_Canilo_WH3100 | 31 VA | 10161303 | 10147535 | 1785 lm |
| CANILO  3P 01 LED2000-M+F WFL  ET 01 | 31 VA | Wide Flood | - | without | CANILO_LED_WFL.ies | LED | M+F | LED | 2000 lm | RAL 9016 traffic white | Oktalite_Alu_RAL_9016 | Oktalite_Canilo_WH3100 | 31 VA | 10161303 | 10147501 | 1785 lm |
| CANILO  3P 01 LED2000-M+F FL-c ET 01 | 31 VA | Flood | - | clear | CANILO_LED_FL.ies | LED | M+F | LED | 2000 lm | RAL 9016 traffic white | Oktalite_Alu_RAL_9016 | Oktalite_Canilo_WH3100 | 31 VA | 10161303 | 10127064 | 1785 lm |
| CANILO  3P 01 LED2000-M+F FL  ET 01 | 31 VA | Flood | - | without | CANILO_LED_FL.ies | LED | M+F | LED | 2000 lm | RAL 9016 traffic white | Oktalite_Alu_RAL_9016 | Oktalite_Canilo_WH3100 | 31 VA | 10161303 | 10125196 | 1785 lm |
| CANILO  3P 01 LED2000-M+F MF-c ET 01 | 31 VA | Medium Flood | - | clear | CANILO_LED_MF.ies | LED | M+F | LED | 2000 lm | RAL 9016 traffic white | Oktalite_Alu_RAL_9016 | Oktalite_Canilo_WH3100 | 31 VA | 10161303 | 10127063 | 1785 lm |
| CANILO  3P 01 LED2000-M+F MF  ET 01 | 31 VA | Medium Flood | - | without | CANILO_LED_MF.ies | LED | M+F | LED | 2000 lm | RAL 9016 traffic white | Oktalite_Alu_RAL_9016 | Oktalite_Canilo_WH3100 | 31 VA | 10161303 | 10125193 | 1785 lm |
| CANILO  3P 01 LED2000-M+F SP-c ET 01 | 31 VA | Spot | - | clear | CANILO_LED_SP.ies | LED | M+F | LED | 2000 lm | RAL 9016 traffic white | Oktalite_Alu_RAL_9016 | Oktalite_Canilo_WH3100 | 31 VA | 10161303 | 10127062 | 1785 lm |
| CANILO  3P 01 LED2000-M+F SP  ET 01 | 31 VA | Spot | - | without | CANILO_LED_SP.ies | LED | M+F | LED | 2000 lm | RAL 9016 traffic white | Oktalite_Alu_RAL_9016 | Oktalite_Canilo_WH3100 | 31 VA | 10161303 | 10125190 | 1785 lm |
| CANILO  3P 05 LED2000-BVC VFL-c ET 05 | 20 VA | Very Wide Flood | - | clear | CANILO_LED_VFL.ies | LED | B+V+C | LED | 2000 lm | RAL 9005 jet black | Oktalite_Alu_RAL_9005 | Oktalite_Canilo_WH3100 | 20 VA | 10161311 | 10147536 | 1955 lm |
| CANILO  3P 05 LED2000-BVC VFL  ET 05 | 20 VA | Very Wide Flood | - | without | CANILO_LED_VFL.ies | LED | B+V+C | LED | 2000 lm | RAL 9005 jet black | Oktalite_Alu_RAL_9005 | Oktalite_Canilo_WH3100 | 20 VA | 10161311 | 10147502 | 1955 lm |
| CANILO  3P 05 LED2000-BVC WFL-c ET 05 | 20 VA | Wide Flood | - | clear | CANILO_LED_WFL.ies | LED | B+V+C | LED | 2000 lm | RAL 9005 jet black | Oktalite_Alu_RAL_9005 | Oktalite_Canilo_WH3100 | 20 VA | 10161311 | 10147535 | 1955 lm |
| CANILO  3P 05 LED2000-BVC WFL  ET 05 | 20 VA | Wide Flood | - | without | CANILO_LED_WFL.ies | LED | B+V+C | LED | 2000 lm | RAL 9005 jet black | Oktalite_Alu_RAL_9005 | Oktalite_Canilo_WH3100 | 20 VA | 10161311 | 10147501 | 1955 lm |
| CANILO  3P 05 LED2000-BVC FL-c ET 05 | 20 VA | Flood | - | clear | CANILO_LED_FL.ies | LED | B+V+C | LED | 2000 lm | RAL 9005 jet black | Oktalite_Alu_RAL_9005 | Oktalite_Canilo_WH3100 | 20 VA | 10161311 | 10127064 | 1955 lm |
| CANILO  3P 05 LED2000-BVC FL  ET 05 | 20 VA | Flood | - | without | CANILO_LED_FL.ies | LED | B+V+C | LED | 2000 lm | RAL 9005 jet black | Oktalite_Alu_RAL_9005 | Oktalite_Canilo_WH3100 | 20 VA | 10161311 | 10125196 | 1955 lm |
| CANILO  3P 05 LED2000-BVC MF-c ET 05 | 20 VA | Medium Flood | - | clear | CANILO_LED_MF.ies | LED | B+V+C | LED | 2000 lm | RAL 9005 jet black | Oktalite_Alu_RAL_9005 | Oktalite_Canilo_WH3100 | 20 VA | 10161311 | 10127063 | 1955 lm |
| CANILO  3P 05 LED2000-BVC MF  ET 05 | 20 VA | Medium Flood | - | without | CANILO_LED_MF.ies | LED | B+V+C | LED | 2000 lm | RAL 9005 jet black | Oktalite_Alu_RAL_9005 | Oktalite_Canilo_WH3100 | 20 VA | 10161311 | 10125193 | 1955 lm |
| CANILO  3P 05 LED2000-BVC SP-c ET 05 | 20 VA | Spot | - | clear | CANILO_LED_SP.ies | LED | B+V+C | LED | 2000 lm | RAL 9005 jet black | Oktalite_Alu_RAL_9005 | Oktalite_Canilo_WH3100 | 20 VA | 10161311 | 10127062 | 1955 lm |
| CANILO  3P 05 LED2000-BVC SP  ET 05 | 20 VA | Spot | - | without | CANILO_LED_SP.ies | LED | B+V+C | LED | 2000 lm | RAL 9005 jet black | Oktalite_Alu_RAL_9005 | Oktalite_Canilo_WH3100 | 20 VA | 10161311 | 10125190 | 1955 lm |
| CANILO  3P 05 LED2000-BVC VFL-c ET 03 | 20 VA | Very Wide Flood | - | clear | CANILO_LED_VFL.ies | LED | B+V+C | LED | 2000 lm | RAL 9006 white aluminium | Oktalite_Alu_RAL_9006 | Oktalite_Canilo_WH3100 | 20 VA | 10161310 | 10147536 | 1955 lm |
| CANILO  3P 05 LED2000-BVC VFL  ET 03 | 20 VA | Very Wide Flood | - | without | CANILO_LED_VFL.ies | LED | B+V+C | LED | 2000 lm | RAL 9006 white aluminium | Oktalite_Alu_RAL_9006 | Oktalite_Canilo_WH3100 | 20 VA | 10161310 | 10147502 | 1955 lm |
| CANILO  3P 05 LED2000-BVC WFL-c ET 03 | 20 VA | Wide Flood | - | clear | CANILO_LED_WFL.ies | LED | B+V+C | LED | 2000 lm | RAL 9006 white aluminium | Oktalite_Alu_RAL_9006 | Oktalite_Canilo_WH3100 | 20 VA | 10161310 | 10147535 | 1955 lm |
| CANILO  3P 05 LED2000-BVC WFL  ET 03 | 20 VA | Wide Flood | - | without | CANILO_LED_WFL.ies | LED | B+V+C | LED | 2000 lm | RAL 9006 white aluminium | Oktalite_Alu_RAL_9006 | Oktalite_Canilo_WH3100 | 20 VA | 10161310 | 10147501 | 1955 lm |
| CANILO  3P 05 LED2000-BVC FL-c ET 03 | 20 VA | Flood | - | clear | CANILO_LED_FL.ies | LED | B+V+C | LED | 2000 lm | RAL 9006 white aluminium | Oktalite_Alu_RAL_9006 | Oktalite_Canilo_WH3100 | 20 VA | 10161310 | 10127064 | 1955 lm |
| CANILO  3P 05 LED2000-BVC FL  ET 03 | 20 VA | Flood | - | without | CANILO_LED_FL.ies | LED | B+V+C | LED | 2000 lm | RAL 9006 white aluminium | Oktalite_Alu_RAL_9006 | Oktalite_Canilo_WH3100 | 20 VA | 10161310 | 10125196 | 1955 lm |
| CANILO  3P 05 LED2000-BVC MF-c ET 03 | 20 VA | Medium Flood | - | clear | CANILO_LED_MF.ies | LED | B+V+C | LED | 2000 lm | RAL 9006 white aluminium | Oktalite_Alu_RAL_9006 | Oktalite_Canilo_WH3100 | 20 VA | 10161310 | 10127063 | 1955 lm |
| CANILO  3P 05 LED2000-BVC MF  ET 03 | 20 VA | Medium Flood | - | without | CANILO_LED_MF.ies | LED | B+V+C | LED | 2000 lm | RAL 9006 white aluminium | Oktalite_Alu_RAL_9006 | Oktalite_Canilo_WH3100 | 20 VA | 10161310 | 10125193 | 1955 lm |
| CANILO  3P 05 LED2000-BVC SP-c ET 03 | 20 VA | Spot | - | clear | CANILO_LED_SP.ies | LED | B+V+C | LED | 2000 lm | RAL 9006 white aluminium | Oktalite_Alu_RAL_9006 | Oktalite_Canilo_WH3100 | 20 VA | 10161310 | 10127062 | 1955 lm |
| CANILO  3P 05 LED2000-BVC SP  ET 03 | 20 VA | Spot | - | without | CANILO_LED_SP.ies | LED | B+V+C | LED | 2000 lm | RAL 9006 white aluminium | Oktalite_Alu_RAL_9006 | Oktalite_Canilo_WH3100 | 20 VA | 10161310 | 10125190 | 1955 lm |
| CANILO  3P 01 LED2000-BVC VFL-c ET 01 | 20 VA | Very Wide Flood | - | clear | CANILO_LED_VFL.ies | LED | B+V+C | LED | 2000 lm | RAL 9016 traffic white | Oktalite_Alu_RAL_9016 | Oktalite_Canilo_WH3100 | 20 VA | 10161309 | 10147536 | 1955 lm |
| CANILO  3P 01 LED2000-BVC VFL  ET 01 | 20 VA | Very Wide Flood | - | without | CANILO_LED_VFL.ies | LED | B+V+C | LED | 2000 lm | RAL 9016 traffic white | Oktalite_Alu_RAL_9016 | Oktalite_Canilo_WH3100 | 20 VA | 10161309 | 10147502 | 1955 lm |
| CANILO  3P 01 LED2000-BVC WFL-c ET 01 | 20 VA | Wide Flood | - | clear | CANILO_LED_WFL.ies | LED | B+V+C | LED | 2000 lm | RAL 9016 traffic white | Oktalite_Alu_RAL_9016 | Oktalite_Canilo_WH3100 | 20 VA | 10161309 | 10147535 | 1955 lm |
| CANILO  3P 01 LED2000-BVC WFL  ET 01 | 20 VA | Wide Flood | - | without | CANILO_LED_WFL.ies | LED | B+V+C | LED | 2000 lm | RAL 9016 traffic white | Oktalite_Alu_RAL_9016 | Oktalite_Canilo_WH3100 | 20 VA | 10161309 | 10147501 | 1955 lm |
| CANILO  3P 01 LED2000-BVC FL-c ET 01 | 20 VA | Flood | - | clear | CANILO_LED_FL.ies | LED | B+V+C | LED | 2000 lm | RAL 9016 traffic white | Oktalite_Alu_RAL_9016 | Oktalite_Canilo_WH3100 | 20 VA | 10161309 | 10127064 | 1955 lm |
| CANILO  3P 01 LED2000-BVC FL  ET 01 | 20 VA | Flood | - | without | CANILO_LED_FL.ies | LED | B+V+C | LED | 2000 lm | RAL 9016 traffic white | Oktalite_Alu_RAL_9016 | Oktalite_Canilo_WH3100 | 20 VA | 10161309 | 10125196 | 1955 lm |
| CANILO  3P 01 LED2000-BVC MF-c ET 01 | 20 VA | Medium Flood | - | clear | CANILO_LED_MF.ies | LED | B+V+C | LED | 2000 lm | RAL 9016 traffic white | Oktalite_Alu_RAL_9016 | Oktalite_Canilo_WH3100 | 20 VA | 10161309 | 10127063 | 1955 lm |
| CANILO  3P 01 LED2000-BVC MF  ET 01 | 20 VA | Medium Flood | - | without | CANILO_LED_MF.ies | LED | B+V+C | LED | 2000 lm | RAL 9016 traffic white | Oktalite_Alu_RAL_9016 | Oktalite_Canilo_WH3100 | 20 VA | 10161309 | 10125193 | 1955 lm |
| CANILO  3P 01 LED2000-BVC SP-c ET 01 | 20 VA | Spot | - | clear | CANILO_LED_SP.ies | LED | B+V+C | LED | 2000 lm | RAL 9016 traffic white | Oktalite_Alu_RAL_9016 | Oktalite_Canilo_WH3100 | 20 VA | 10161309 | 10127062 | 1955 lm |
| CANILO  3P 01 LED2000-BVC SP  ET 01 | 20 VA | Spot | - | without | CANILO_LED_SP.ies | LED | B+V+C | LED | 2000 lm | RAL 9016 traffic white | Oktalite_Alu_RAL_9016 | Oktalite_Canilo_WH3100 | 20 VA | 10161309 | 10125190 | 1955 lm |
| CANILO  3P 05 LED3000-831 VFL-c ET 05 | 24 VA | Very Wide Flood | 85 | clear | CANILO_LED_VFL.ies | LED | 3100 K Efficient Colour | LED | 3000 lm | RAL 9005 jet black | Oktalite_Alu_RAL_9005 | Oktalite_Canilo_WH3100 | 24 VA | 10161666 | 10147536 | 2815 lm |
| CANILO  3P 05 LED3000-831 VFL  ET 05 | 24 VA | Very Wide Flood | 85 | without | CANILO_LED_VFL.ies | LED | 3100 K Efficient Colour | LED | 3000 lm | RAL 9005 jet black | Oktalite_Alu_RAL_9005 | Oktalite_Canilo_WH3100 | 24 VA | 10161666 | 10147502 | 2815 lm |
| CANILO  3P 05 LED3000-831 WFL-c ET 05 | 24 VA | Wide Flood | 85 | clear | CANILO_LED_WFL.ies | LED | 3100 K Efficient Colour | LED | 3000 lm | RAL 9005 jet black | Oktalite_Alu_RAL_9005 | Oktalite_Canilo_WH3100 | 24 VA | 10161666 | 10147535 | 2815 lm |
| CANILO  3P 05 LED3000-831 WFL  ET 05 | 24 VA | Wide Flood | 85 | without | CANILO_LED_WFL.ies | LED | 3100 K Efficient Colour | LED | 3000 lm | RAL 9005 jet black | Oktalite_Alu_RAL_9005 | Oktalite_Canilo_WH3100 | 24 VA | 10161666 | 10147501 | 2815 lm |
| CANILO  3P 05 LED3000-831 FL-c ET 05 | 24 VA | Flood | 85 | clear | CANILO_LED_FL.ies | LED | 3100 K Efficient Colour | LED | 3000 lm | RAL 9005 jet black | Oktalite_Alu_RAL_9005 | Oktalite_Canilo_WH3100 | 24 VA | 10161666 | 10127064 | 2815 lm |
| CANILO  3P 05 LED3000-831 FL  ET 05 | 24 VA | Flood | 85 | without | CANILO_LED_FL.ies | LED | 3100 K Efficient Colour | LED | 3000 lm | RAL 9005 jet black | Oktalite_Alu_RAL_9005 | Oktalite_Canilo_WH3100 | 24 VA | 10161666 | 10125196 | 2815 lm |
| CANILO  3P 05 LED3000-831 MF-c ET 05 | 24 VA | Medium Flood | 85 | clear | CANILO_LED_MF.ies | LED | 3100 K Efficient Colour | LED | 3000 lm | RAL 9005 jet black | Oktalite_Alu_RAL_9005 | Oktalite_Canilo_WH3100 | 24 VA | 10161666 | 10127063 | 2815 lm |
| CANILO  3P 05 LED3000-831 MF  ET 05 | 24 VA | Medium Flood | 85 | without | CANILO_LED_MF.ies | LED | 3100 K Efficient Colour | LED | 3000 lm | RAL 9005 jet black | Oktalite_Alu_RAL_9005 | Oktalite_Canilo_WH3100 | 24 VA | 10161666 | 10125193 | 2815 lm |
| CANILO  3P 05 LED3000-831 SP-c ET 05 | 24 VA | Spot | 85 | clear | CANILO_LED_SP.ies | LED | 3100 K Efficient Colour | LED | 3000 lm | RAL 9005 jet black | Oktalite_Alu_RAL_9005 | Oktalite_Canilo_WH3100 | 24 VA | 10161666 | 10127062 | 2815 lm |
| CANILO  3P 05 LED3000-831 SP  ET 05 | 24 VA | Spot | 85 | without | CANILO_LED_SP.ies | LED | 3100 K Efficient Colour | LED | 3000 lm | RAL 9005 jet black | Oktalite_Alu_RAL_9005 | Oktalite_Canilo_WH3100 | 24 VA | 10161666 | 10125190 | 2815 lm |
| CANILO  3P 05 LED3000-831 VFL-c ET 03 | 24 VA | Very Wide Flood | 85 | clear | CANILO_LED_VFL.ies | LED | 3100 K Efficient Colour | LED | 3000 lm | RAL 9006 white aluminium | Oktalite_Alu_RAL_9006 | Oktalite_Canilo_WH3100 | 24 VA | 10161665 | 10147536 | 2815 lm |
| CANILO  3P 05 LED3000-831 VFL  ET 03 | 24 VA | Very Wide Flood | 85 | without | CANILO_LED_VFL.ies | LED | 3100 K Efficient Colour | LED | 3000 lm | RAL 9006 white aluminium | Oktalite_Alu_RAL_9006 | Oktalite_Canilo_WH3100 | 24 VA | 10161665 | 10147502 | 2815 lm |
| CANILO  3P 05 LED3000-831 WFL-c ET 03 | 24 VA | Wide Flood | 85 | clear | CANILO_LED_WFL.ies | LED | 3100 K Efficient Colour | LED | 3000 lm | RAL 9006 white aluminium | Oktalite_Alu_RAL_9006 | Oktalite_Canilo_WH3100 | 24 VA | 10161665 | 10147535 | 2815 lm |
| CANILO  3P 05 LED3000-831 WFL  ET 03 | 24 VA | Wide Flood | 85 | without | CANILO_LED_WFL.ies | LED | 3100 K Efficient Colour | LED | 3000 lm | RAL 9006 white aluminium | Oktalite_Alu_RAL_9006 | Oktalite_Canilo_WH3100 | 24 VA | 10161665 | 10147501 | 2815 lm |
| CANILO  3P 05 LED3000-831 FL-c ET 03 | 24 VA | Flood | 85 | clear | CANILO_LED_FL.ies | LED | 3100 K Efficient Colour | LED | 3000 lm | RAL 9006 white aluminium | Oktalite_Alu_RAL_9006 | Oktalite_Canilo_WH3100 | 24 VA | 10161665 | 10127064 | 2815 lm |
| CANILO  3P 05 LED3000-831 FL  ET 03 | 24 VA | Flood | 85 | without | CANILO_LED_FL.ies | LED | 3100 K Efficient Colour | LED | 3000 lm | RAL 9006 white aluminium | Oktalite_Alu_RAL_9006 | Oktalite_Canilo_WH3100 | 24 VA | 10161665 | 10125196 | 2815 lm |
| CANILO  3P 05 LED3000-831 MF-c ET 03 | 24 VA | Medium Flood | 85 | clear | CANILO_LED_MF.ies | LED | 3100 K Efficient Colour | LED | 3000 lm | RAL 9006 white aluminium | Oktalite_Alu_RAL_9006 | Oktalite_Canilo_WH3100 | 24 VA | 10161665 | 10127063 | 2815 lm |
| CANILO  3P 05 LED3000-831 MF  ET 03 | 24 VA | Medium Flood | 85 | without | CANILO_LED_MF.ies | LED | 3100 K Efficient Colour | LED | 3000 lm | RAL 9006 white aluminium | Oktalite_Alu_RAL_9006 | Oktalite_Canilo_WH3100 | 24 VA | 10161665 | 10125193 | 2815 lm |
| CANILO  3P 05 LED3000-831 SP-c ET 03 | 24 VA | Spot | 85 | clear | CANILO_LED_SP.ies | LED | 3100 K Efficient Colour | LED | 3000 lm | RAL 9006 white aluminium | Oktalite_Alu_RAL_9006 | Oktalite_Canilo_WH3100 | 24 VA | 10161665 | 10127062 | 2815 lm |
| CANILO  3P 05 LED3000-831 SP  ET 03 | 24 VA | Spot | 85 | without | CANILO_LED_SP.ies | LED | 3100 K Efficient Colour | LED | 3000 lm | RAL 9006 white aluminium | Oktalite_Alu_RAL_9006 | Oktalite_Canilo_WH3100 | 24 VA | 10161665 | 10125190 | 2815 lm |
| CANILO  3P 01 LED3000-831 VFL-c ET 01 | 24 VA | Very Wide Flood | 85 | clear | CANILO_LED_VFL.ies | LED | 3100 K Efficient Colour | LED | 3000 lm | RAL 9016 traffic white | Oktalite_Alu_RAL_9016 | Oktalite_Canilo_WH3100 | 24 VA | 10161664 | 10147536 | 2815 lm |
| CANILO  3P 01 LED3000-831 VFL  ET 01 | 24 VA | Very Wide Flood | 85 | without | CANILO_LED_VFL.ies | LED | 3100 K Efficient Colour | LED | 3000 lm | RAL 9016 traffic white | Oktalite_Alu_RAL_9016 | Oktalite_Canilo_WH3100 | 24 VA | 10161664 | 10147502 | 2815 lm |
| CANILO  3P 01 LED3000-831 WFL-c ET 01 | 24 VA | Wide Flood | 85 | clear | CANILO_LED_WFL.ies | LED | 3100 K Efficient Colour | LED | 3000 lm | RAL 9016 traffic white | Oktalite_Alu_RAL_9016 | Oktalite_Canilo_WH3100 | 24 VA | 10161664 | 10147535 | 2815 lm |
| CANILO  3P 01 LED3000-831 WFL  ET 01 | 24 VA | Wide Flood | 85 | without | CANILO_LED_WFL.ies | LED | 3100 K Efficient Colour | LED | 3000 lm | RAL 9016 traffic white | Oktalite_Alu_RAL_9016 | Oktalite_Canilo_WH3100 | 24 VA | 10161664 | 10147501 | 2815 lm |
| CANILO  3P 01 LED3000-831 FL-c ET 01 | 24 VA | Flood | 85 | clear | CANILO_LED_FL.ies | LED | 3100 K Efficient Colour | LED | 3000 lm | RAL 9016 traffic white | Oktalite_Alu_RAL_9016 | Oktalite_Canilo_WH3100 | 24 VA | 10161664 | 10127064 | 2815 lm |
| CANILO  3P 01 LED3000-831 FL  ET 01 | 24 VA | Flood | 85 | without | CANILO_LED_FL.ies | LED | 3100 K Efficient Colour | LED | 3000 lm | RAL 9016 traffic white | Oktalite_Alu_RAL_9016 | Oktalite_Canilo_WH3100 | 24 VA | 10161664 | 10125196 | 2815 lm |
| CANILO  3P 01 LED3000-831 MF-c ET 01 | 24 VA | Medium Flood | 85 | clear | CANILO_LED_MF.ies | LED | 3100 K Efficient Colour | LED | 3000 lm | RAL 9016 traffic white | Oktalite_Alu_RAL_9016 | Oktalite_Canilo_WH3100 | 24 VA | 10161664 | 10127063 | 2815 lm |
| CANILO  3P 01 LED3000-831 MF  ET 01 | 24 VA | Medium Flood | 85 | without | CANILO_LED_MF.ies | LED | 3100 K Efficient Colour | LED | 3000 lm | RAL 9016 traffic white | Oktalite_Alu_RAL_9016 | Oktalite_Canilo_WH3100 | 24 VA | 10161664 | 10125193 | 2815 lm |
| CANILO  3P 01 LED3000-831 SP-c ET 01 | 24 VA | Spot | 85 | clear | CANILO_LED_SP.ies | LED | 3100 K Efficient Colour | LED | 3000 lm | RAL 9016 traffic white | Oktalite_Alu_RAL_9016 | Oktalite_Canilo_WH3100 | 24 VA | 10161664 | 10127062 | 2815 lm |
| CANILO  3P 01 LED3000-831 SP  ET 01 | 24 VA | Spot | 85 | without | CANILO_LED_SP.ies | LED | 3100 K Efficient Colour | LED | 3000 lm | RAL 9016 traffic white | Oktalite_Alu_RAL_9016 | Oktalite_Canilo_WH3100 | 24 VA | 10161664 | 10125190 | 2815 lm |
| CANILO  3P 05 LED3000-931 VFL-c ET 05 | 32 VA | Very Wide Flood | 95 | clear | CANILO_LED_VFL.ies | LED | 3100 K Best Colour | LED | 3000 lm | RAL 9005 jet black | Oktalite_Alu_RAL_9005 | Oktalite_Canilo_WH3100 | 32 VA | 10161675 | 10147536 | 2895 lm |
| CANILO  3P 05 LED3000-931 VFL  ET 05 | 32 VA | Very Wide Flood | 95 | without | CANILO_LED_VFL.ies | LED | 3100 K Best Colour | LED | 3000 lm | RAL 9005 jet black | Oktalite_Alu_RAL_9005 | Oktalite_Canilo_WH3100 | 32 VA | 10161675 | 10147502 | 2895 lm |
| CANILO  3P 05 LED3000-931 WFL-c ET 05 | 32 VA | Wide Flood | 95 | clear | CANILO_LED_WFL.ies | LED | 3100 K Best Colour | LED | 3000 lm | RAL 9005 jet black | Oktalite_Alu_RAL_9005 | Oktalite_Canilo_WH3100 | 32 VA | 10161675 | 10147535 | 2895 lm |
| CANILO  3P 05 LED3000-931 WFL  ET 05 | 32 VA | Wide Flood | 95 | without | CANILO_LED_WFL.ies | LED | 3100 K Best Colour | LED | 3000 lm | RAL 9005 jet black | Oktalite_Alu_RAL_9005 | Oktalite_Canilo_WH3100 | 32 VA | 10161675 | 10147501 | 2895 lm |
| CANILO  3P 05 LED3000-931 FL-c ET 05 | 32 VA | Flood | 95 | clear | CANILO_LED_FL.ies | LED | 3100 K Best Colour | LED | 3000 lm | RAL 9005 jet black | Oktalite_Alu_RAL_9005 | Oktalite_Canilo_WH3100 | 32 VA | 10161675 | 10127064 | 2895 lm |
| CANILO  3P 05 LED3000-931 FL  ET 05 | 32 VA | Flood | 95 | without | CANILO_LED_FL.ies | LED | 3100 K Best Colour | LED | 3000 lm | RAL 9005 jet black | Oktalite_Alu_RAL_9005 | Oktalite_Canilo_WH3100 | 32 VA | 10161675 | 10125196 | 2895 lm |
| CANILO  3P 05 LED3000-931 MF-c ET 05 | 32 VA | Medium Flood | 95 | clear | CANILO_LED_MF.ies | LED | 3100 K Best Colour | LED | 3000 lm | RAL 9005 jet black | Oktalite_Alu_RAL_9005 | Oktalite_Canilo_WH3100 | 32 VA | 10161675 | 10127063 | 2895 lm |
| CANILO  3P 05 LED3000-931 MF  ET 05 | 32 VA | Medium Flood | 95 | without | CANILO_LED_MF.ies | LED | 3100 K Best Colour | LED | 3000 lm | RAL 9005 jet black | Oktalite_Alu_RAL_9005 | Oktalite_Canilo_WH3100 | 32 VA | 10161675 | 10125193 | 2895 lm |
| CANILO  3P 05 LED3000-931 SP-c ET 05 | 32 VA | Spot | 95 | clear | CANILO_LED_SP.ies | LED | 3100 K Best Colour | LED | 3000 lm | RAL 9005 jet black | Oktalite_Alu_RAL_9005 | Oktalite_Canilo_WH3100 | 32 VA | 10161675 | 10127062 | 2895 lm |
| CANILO  3P 05 LED3000-931 SP  ET 05 | 32 VA | Spot | 95 | without | CANILO_LED_SP.ies | LED | 3100 K Best Colour | LED | 3000 lm | RAL 9005 jet black | Oktalite_Alu_RAL_9005 | Oktalite_Canilo_WH3100 | 32 VA | 10161675 | 10125190 | 2895 lm |
| CANILO  3P 05 LED3000-931 VFL-c ET 03 | 32 VA | Very Wide Flood | 95 | clear | CANILO_LED_VFL.ies | LED | 3100 K Best Colour | LED | 3000 lm | RAL 9006 white aluminium | Oktalite_Alu_RAL_9006 | Oktalite_Canilo_WH3100 | 32 VA | 10161674 | 10147536 | 2895 lm |
| CANILO  3P 05 LED3000-931 VFL  ET 03 | 32 VA | Very Wide Flood | 95 | without | CANILO_LED_VFL.ies | LED | 3100 K Best Colour | LED | 3000 lm | RAL 9006 white aluminium | Oktalite_Alu_RAL_9006 | Oktalite_Canilo_WH3100 | 32 VA | 10161674 | 10147502 | 2895 lm |
| CANILO  3P 05 LED3000-931 WFL-c ET 03 | 32 VA | Wide Flood | 95 | clear | CANILO_LED_WFL.ies | LED | 3100 K Best Colour | LED | 3000 lm | RAL 9006 white aluminium | Oktalite_Alu_RAL_9006 | Oktalite_Canilo_WH3100 | 32 VA | 10161674 | 10147535 | 2895 lm |
| CANILO  3P 05 LED3000-931 WFL  ET 03 | 32 VA | Wide Flood | 95 | without | CANILO_LED_WFL.ies | LED | 3100 K Best Colour | LED | 3000 lm | RAL 9006 white aluminium | Oktalite_Alu_RAL_9006 | Oktalite_Canilo_WH3100 | 32 VA | 10161674 | 10147501 | 2895 lm |
| CANILO  3P 05 LED3000-931 FL-c ET 03 | 32 VA | Flood | 95 | clear | CANILO_LED_FL.ies | LED | 3100 K Best Colour | LED | 3000 lm | RAL 9006 white aluminium | Oktalite_Alu_RAL_9006 | Oktalite_Canilo_WH3100 | 32 VA | 10161674 | 10127064 | 2895 lm |
| CANILO  3P 05 LED3000-931 FL  ET 03 | 32 VA | Flood | 95 | without | CANILO_LED_FL.ies | LED | 3100 K Best Colour | LED | 3000 lm | RAL 9006 white aluminium | Oktalite_Alu_RAL_9006 | Oktalite_Canilo_WH3100 | 32 VA | 10161674 | 10125196 | 2895 lm |
| CANILO  3P 05 LED3000-931 MF-c ET 03 | 32 VA | Medium Flood | 95 | clear | CANILO_LED_MF.ies | LED | 3100 K Best Colour | LED | 3000 lm | RAL 9006 white aluminium | Oktalite_Alu_RAL_9006 | Oktalite_Canilo_WH3100 | 32 VA | 10161674 | 10127063 | 2895 lm |
| CANILO  3P 05 LED3000-931 MF  ET 03 | 32 VA | Medium Flood | 95 | without | CANILO_LED_MF.ies | LED | 3100 K Best Colour | LED | 3000 lm | RAL 9006 white aluminium | Oktalite_Alu_RAL_9006 | Oktalite_Canilo_WH3100 | 32 VA | 10161674 | 10125193 | 2895 lm |
| CANILO  3P 05 LED3000-931 SP-c ET 03 | 32 VA | Spot | 95 | clear | CANILO_LED_SP.ies | LED | 3100 K Best Colour | LED | 3000 lm | RAL 9006 white aluminium | Oktalite_Alu_RAL_9006 | Oktalite_Canilo_WH3100 | 32 VA | 10161674 | 10127062 | 2895 lm |
| CANILO  3P 05 LED3000-931 SP  ET 03 | 32 VA | Spot | 95 | without | CANILO_LED_SP.ies | LED | 3100 K Best Colour | LED | 3000 lm | RAL 9006 white aluminium | Oktalite_Alu_RAL_9006 | Oktalite_Canilo_WH3100 | 32 VA | 10161674 | 10125190 | 2895 lm |
| CANILO  3P 01 LED3000-931 VFL-c ET 01 | 32 VA | Very Wide Flood | 95 | clear | CANILO_LED_VFL.ies | LED | 3100 K Best Colour | LED | 3000 lm | RAL 9016 traffic white | Oktalite_Alu_RAL_9016 | Oktalite_Canilo_WH3100 | 32 VA | 10161673 | 10147536 | 2895 lm |
| CANILO  3P 01 LED3000-931 VFL  ET 01 | 32 VA | Very Wide Flood | 95 | without | CANILO_LED_VFL.ies | LED | 3100 K Best Colour | LED | 3000 lm | RAL 9016 traffic white | Oktalite_Alu_RAL_9016 | Oktalite_Canilo_WH3100 | 32 VA | 10161673 | 10147502 | 2895 lm |
| CANILO  3P 01 LED3000-931 WFL-c ET 01 | 32 VA | Wide Flood | 95 | clear | CANILO_LED_WFL.ies | LED | 3100 K Best Colour | LED | 3000 lm | RAL 9016 traffic white | Oktalite_Alu_RAL_9016 | Oktalite_Canilo_WH3100 | 32 VA | 10161673 | 10147535 | 2895 lm |
| CANILO  3P 01 LED3000-931 WFL  ET 01 | 32 VA | Wide Flood | 95 | without | CANILO_LED_WFL.ies | LED | 3100 K Best Colour | LED | 3000 lm | RAL 9016 traffic white | Oktalite_Alu_RAL_9016 | Oktalite_Canilo_WH3100 | 32 VA | 10161673 | 10147501 | 2895 lm |
| CANILO  3P 01 LED3000-931 FL-c ET 01 | 32 VA | Flood | 95 | clear | CANILO_LED_FL.ies | LED | 3100 K Best Colour | LED | 3000 lm | RAL 9016 traffic white | Oktalite_Alu_RAL_9016 | Oktalite_Canilo_WH3100 | 32 VA | 10161673 | 10127064 | 2895 lm |
| CANILO  3P 01 LED3000-931 FL  ET 01 | 32 VA | Flood | 95 | without | CANILO_LED_FL.ies | LED | 3100 K Best Colour | LED | 3000 lm | RAL 9016 traffic white | Oktalite_Alu_RAL_9016 | Oktalite_Canilo_WH3100 | 32 VA | 10161673 | 10125196 | 2895 lm |
| CANILO  3P 01 LED3000-931 MF-c ET 01 | 32 VA | Medium Flood | 95 | clear | CANILO_LED_MF.ies | LED | 3100 K Best Colour | LED | 3000 lm | RAL 9016 traffic white | Oktalite_Alu_RAL_9016 | Oktalite_Canilo_WH3100 | 32 VA | 10161673 | 10127063 | 2895 lm |
| CANILO  3P 01 LED3000-931 MF  ET 01 | 32 VA | Medium Flood | 95 | without | CANILO_LED_MF.ies | LED | 3100 K Best Colour | LED | 3000 lm | RAL 9016 traffic white | Oktalite_Alu_RAL_9016 | Oktalite_Canilo_WH3100 | 32 VA | 10161673 | 10125193 | 2895 lm |
| CANILO  3P 01 LED3000-931 SP-c ET 01 | 32 VA | Spot | 95 | clear | CANILO_LED_SP.ies | LED | 3100 K Best Colour | LED | 3000 lm | RAL 9016 traffic white | Oktalite_Alu_RAL_9016 | Oktalite_Canilo_WH3100 | 32 VA | 10161673 | 10127062 | 2895 lm |
| CANILO  3P 01 LED3000-931 SP  ET 01 | 32 VA | Spot | 95 | without | CANILO_LED_SP.ies | LED | 3100 K Best Colour | LED | 3000 lm | RAL 9016 traffic white | Oktalite_Alu_RAL_9016 | Oktalite_Canilo_WH3100 | 32 VA | 10161673 | 10125190 | 2895 lm |
| CANILO  3P 05 LED3000-840 VFL-c ET 05 | 24 VA | Very Wide Flood | 85 | clear | CANILO_LED_VFL.ies | LED | 4000 K | LED | 3000 lm | RAL 9005 jet black | Oktalite_Alu_RAL_9005 | Oktalite_Canilo_WH4000 | 24 VA | 10161672 | 10147536 | 2995 lm |
| CANILO  3P 05 LED3000-840 VFL  ET 05 | 24 VA | Very Wide Flood | 85 | without | CANILO_LED_VFL.ies | LED | 4000 K | LED | 3000 lm | RAL 9005 jet black | Oktalite_Alu_RAL_9005 | Oktalite_Canilo_WH4000 | 24 VA | 10161672 | 10147502 | 2995 lm |
| CANILO  3P 05 LED3000-840 WFL-c ET 05 | 24 VA | Wide Flood | 85 | clear | CANILO_LED_WFL.ies | LED | 4000 K | LED | 3000 lm | RAL 9005 jet black | Oktalite_Alu_RAL_9005 | Oktalite_Canilo_WH4000 | 24 VA | 10161672 | 10147535 | 2995 lm |
| CANILO  3P 05 LED3000-840 WFL  ET 05 | 24 VA | Wide Flood | 85 | without | CANILO_LED_WFL.ies | LED | 4000 K | LED | 3000 lm | RAL 9005 jet black | Oktalite_Alu_RAL_9005 | Oktalite_Canilo_WH4000 | 24 VA | 10161672 | 10147501 | 2995 lm |
| CANILO  3P 05 LED3000-840 FL-c ET 05 | 24 VA | Flood | 85 | clear | CANILO_LED_FL.ies | LED | 4000 K | LED | 3000 lm | RAL 9005 jet black | Oktalite_Alu_RAL_9005 | Oktalite_Canilo_WH4000 | 24 VA | 10161672 | 10127064 | 2995 lm |
| CANILO  3P 05 LED3000-840 FL  ET 05 | 24 VA | Flood | 85 | without | CANILO_LED_FL.ies | LED | 4000 K | LED | 3000 lm | RAL 9005 jet black | Oktalite_Alu_RAL_9005 | Oktalite_Canilo_WH4000 | 24 VA | 10161672 | 10125196 | 2995 lm |
| CANILO  3P 05 LED3000-840 MF-c ET 05 | 24 VA | Medium Flood | 85 | clear | CANILO_LED_MF.ies | LED | 4000 K | LED | 3000 lm | RAL 9005 jet black | Oktalite_Alu_RAL_9005 | Oktalite_Canilo_WH4000 | 24 VA | 10161672 | 10127063 | 2995 lm |
| CANILO  3P 05 LED3000-840 MF  ET 05 | 24 VA | Medium Flood | 85 | without | CANILO_LED_MF.ies | LED | 4000 K | LED | 3000 lm | RAL 9005 jet black | Oktalite_Alu_RAL_9005 | Oktalite_Canilo_WH4000 | 24 VA | 10161672 | 10125193 | 2995 lm |
| CANILO  3P 05 LED3000-840 SP-c ET 05 | 24 VA | Spot | 85 | clear | CANILO_LED_SP.ies | LED | 4000 K | LED | 3000 lm | RAL 9005 jet black | Oktalite_Alu_RAL_9005 | Oktalite_Canilo_WH4000 | 24 VA | 10161672 | 10127062 | 2995 lm |
| CANILO  3P 05 LED3000-840 SP  ET 05 | 24 VA | Spot | 85 | without | CANILO_LED_SP.ies | LED | 4000 K | LED | 3000 lm | RAL 9005 jet black | Oktalite_Alu_RAL_9005 | Oktalite_Canilo_WH4000 | 24 VA | 10161672 | 10125190 | 2995 lm |
| CANILO  3P 05 LED3000-840 VFL-c ET 03 | 24 VA | Very Wide Flood | 85 | clear | CANILO_LED_VFL.ies | LED | 4000 K | LED | 3000 lm | RAL 9006 white aluminium | Oktalite_Alu_RAL_9006 | Oktalite_Canilo_WH4000 | 24 VA | 10161671 | 10147536 | 2995 lm |
| CANILO  3P 05 LED3000-840 VFL  ET 03 | 24 VA | Very Wide Flood | 85 | without | CANILO_LED_VFL.ies | LED | 4000 K | LED | 3000 lm | RAL 9006 white aluminium | Oktalite_Alu_RAL_9006 | Oktalite_Canilo_WH4000 | 24 VA | 10161671 | 10147502 | 2995 lm |
| CANILO  3P 05 LED3000-840 WFL-c ET 03 | 24 VA | Wide Flood | 85 | clear | CANILO_LED_WFL.ies | LED | 4000 K | LED | 3000 lm | RAL 9006 white aluminium | Oktalite_Alu_RAL_9006 | Oktalite_Canilo_WH4000 | 24 VA | 10161671 | 10147535 | 2995 lm |
| CANILO  3P 05 LED3000-840 WFL  ET 03 | 24 VA | Wide Flood | 85 | without | CANILO_LED_WFL.ies | LED | 4000 K | LED | 3000 lm | RAL 9006 white aluminium | Oktalite_Alu_RAL_9006 | Oktalite_Canilo_WH4000 | 24 VA | 10161671 | 10147501 | 2995 lm |
| CANILO  3P 05 LED3000-840 FL-c ET 03 | 24 VA | Flood | 85 | clear | CANILO_LED_FL.ies | LED | 4000 K | LED | 3000 lm | RAL 9006 white aluminium | Oktalite_Alu_RAL_9006 | Oktalite_Canilo_WH4000 | 24 VA | 10161671 | 10127064 | 2995 lm |
| CANILO  3P 05 LED3000-840 FL  ET 03 | 24 VA | Flood | 85 | without | CANILO_LED_FL.ies | LED | 4000 K | LED | 3000 lm | RAL 9006 white aluminium | Oktalite_Alu_RAL_9006 | Oktalite_Canilo_WH4000 | 24 VA | 10161671 | 10125196 | 2995 lm |
| CANILO  3P 05 LED3000-840 MF-c ET 03 | 24 VA | Medium Flood | 85 | clear | CANILO_LED_MF.ies | LED | 4000 K | LED | 3000 lm | RAL 9006 white aluminium | Oktalite_Alu_RAL_9006 | Oktalite_Canilo_WH4000 | 24 VA | 10161671 | 10127063 | 2995 lm |
| CANILO  3P 05 LED3000-840 MF  ET 03 | 24 VA | Medium Flood | 85 | without | CANILO_LED_MF.ies | LED | 4000 K | LED | 3000 lm | RAL 9006 white aluminium | Oktalite_Alu_RAL_9006 | Oktalite_Canilo_WH4000 | 24 VA | 10161671 | 10125193 | 2995 lm |
| CANILO  3P 05 LED3000-840 SP-c ET 03 | 24 VA | Spot | 85 | clear | CANILO_LED_SP.ies | LED | 4000 K | LED | 3000 lm | RAL 9006 white aluminium | Oktalite_Alu_RAL_9006 | Oktalite_Canilo_WH4000 | 24 VA | 10161671 | 10127062 | 2995 lm |
| CANILO  3P 05 LED3000-840 SP  ET 03 | 24 VA | Spot | 85 | without | CANILO_LED_SP.ies | LED | 4000 K | LED | 3000 lm | RAL 9006 white aluminium | Oktalite_Alu_RAL_9006 | Oktalite_Canilo_WH4000 | 24 VA | 10161671 | 10125190 | 2995 lm |
| CANILO  3P 01 LED3000-840 VFL-c ET 01 | 24 VA | Very Wide Flood | 85 | clear | CANILO_LED_VFL.ies | LED | 4000 K | LED | 3000 lm | RAL 9016 traffic white | Oktalite_Alu_RAL_9016 | Oktalite_Canilo_WH4000 | 24 VA | 10161670 | 10147536 | 2995 lm |
| CANILO  3P 01 LED3000-840 VFL  ET 01 | 24 VA | Very Wide Flood | 85 | without | CANILO_LED_VFL.ies | LED | 4000 K | LED | 3000 lm | RAL 9016 traffic white | Oktalite_Alu_RAL_9016 | Oktalite_Canilo_WH4000 | 24 VA | 10161670 | 10147502 | 2995 lm |
| CANILO  3P 01 LED3000-840 WFL-c ET 01 | 24 VA | Wide Flood | 85 | clear | CANILO_LED_WFL.ies | LED | 4000 K | LED | 3000 lm | RAL 9016 traffic white | Oktalite_Alu_RAL_9016 | Oktalite_Canilo_WH4000 | 24 VA | 10161670 | 10147535 | 2995 lm |
| CANILO  3P 01 LED3000-840 WFL  ET 01 | 24 VA | Wide Flood | 85 | without | CANILO_LED_WFL.ies | LED | 4000 K | LED | 3000 lm | RAL 9016 traffic white | Oktalite_Alu_RAL_9016 | Oktalite_Canilo_WH4000 | 24 VA | 10161670 | 10147501 | 2995 lm |
| CANILO  3P 01 LED3000-840 FL-c ET 01 | 24 VA | Flood | 85 | clear | CANILO_LED_FL.ies | LED | 4000 K | LED | 3000 lm | RAL 9016 traffic white | Oktalite_Alu_RAL_9016 | Oktalite_Canilo_WH4000 | 24 VA | 10161670 | 10127064 | 2995 lm |
| CANILO  3P 01 LED3000-840 FL  ET 01 | 24 VA | Flood | 85 | without | CANILO_LED_FL.ies | LED | 4000 K | LED | 3000 lm | RAL 9016 traffic white | Oktalite_Alu_RAL_9016 | Oktalite_Canilo_WH4000 | 24 VA | 10161670 | 10125196 | 2995 lm |
| CANILO  3P 01 LED3000-840 MF-c ET 01 | 24 VA | Medium Flood | 85 | clear | CANILO_LED_MF.ies | LED | 4000 K | LED | 3000 lm | RAL 9016 traffic white | Oktalite_Alu_RAL_9016 | Oktalite_Canilo_WH4000 | 24 VA | 10161670 | 10127063 | 2995 lm |
| CANILO  3P 01 LED3000-840 MF  ET 01 | 24 VA | Medium Flood | 85 | without | CANILO_LED_MF.ies | LED | 4000 K | LED | 3000 lm | RAL 9016 traffic white | Oktalite_Alu_RAL_9016 | Oktalite_Canilo_WH4000 | 24 VA | 10161670 | 10125193 | 2995 lm |
| CANILO  3P 01 LED3000-840 SP-c ET 01 | 24 VA | Spot | 85 | clear | CANILO_LED_SP.ies | LED | 4000 K | LED | 3000 lm | RAL 9016 traffic white | Oktalite_Alu_RAL_9016 | Oktalite_Canilo_WH4000 | 24 VA | 10161670 | 10127062 | 2995 lm |
| CANILO  3P 01 LED3000-840 SP  ET 01 | 24 VA | Spot | 85 | without | CANILO_LED_SP.ies | LED | 4000 K | LED | 3000 lm | RAL 9016 traffic white | Oktalite_Alu_RAL_9016 | Oktalite_Canilo_WH4000 | 24 VA | 10161670 | 10125190 | 2995 lm |
| CANILO  3P 05 LED3000-835 VFL-c ET 05 | 24 VA | Very Wide Flood | 85 | clear | CANILO_LED_VFL.ies | LED | 3500 K | LED | 3000 lm | RAL 9005 jet black | Oktalite_Alu_RAL_9005 | Oktalite_Canilo_WH3500 | 24 VA | 10161669 | 10147536 | 2930 lm |
| CANILO  3P 05 LED3000-835 VFL  ET 05 | 24 VA | Very Wide Flood | 85 | without | CANILO_LED_VFL.ies | LED | 3500 K | LED | 3000 lm | RAL 9005 jet black | Oktalite_Alu_RAL_9005 | Oktalite_Canilo_WH3500 | 24 VA | 10161669 | 10147502 | 2930 lm |
| CANILO  3P 05 LED3000-835 WFL-c ET 05 | 24 VA | Wide Flood | 85 | clear | CANILO_LED_WFL.ies | LED | 3500 K | LED | 3000 lm | RAL 9005 jet black | Oktalite_Alu_RAL_9005 | Oktalite_Canilo_WH3500 | 24 VA | 10161669 | 10147535 | 2930 lm |
| CANILO  3P 05 LED3000-835 WFL  ET 05 | 24 VA | Wide Flood | 85 | without | CANILO_LED_WFL.ies | LED | 3500 K | LED | 3000 lm | RAL 9005 jet black | Oktalite_Alu_RAL_9005 | Oktalite_Canilo_WH3500 | 24 VA | 10161669 | 10147501 | 2930 lm |
| CANILO  3P 05 LED3000-835 FL-c ET 05 | 24 VA | Flood | 85 | clear | CANILO_LED_FL.ies | LED | 3500 K | LED | 3000 lm | RAL 9005 jet black | Oktalite_Alu_RAL_9005 | Oktalite_Canilo_WH3500 | 24 VA | 10161669 | 10127064 | 2930 lm |
| CANILO  3P 05 LED3000-835 FL  ET 05 | 24 VA | Flood | 85 | without | CANILO_LED_FL.ies | LED | 3500 K | LED | 3000 lm | RAL 9005 jet black | Oktalite_Alu_RAL_9005 | Oktalite_Canilo_WH3500 | 24 VA | 10161669 | 10125196 | 2930 lm |
| CANILO  3P 05 LED3000-835 MF-c ET 05 | 24 VA | Medium Flood | 85 | clear | CANILO_LED_MF.ies | LED | 3500 K | LED | 3000 lm | RAL 9005 jet black | Oktalite_Alu_RAL_9005 | Oktalite_Canilo_WH3500 | 24 VA | 10161669 | 10127063 | 2930 lm |
| CANILO  3P 05 LED3000-835 MF  ET 05 | 24 VA | Medium Flood | 85 | without | CANILO_LED_MF.ies | LED | 3500 K | LED | 3000 lm | RAL 9005 jet black | Oktalite_Alu_RAL_9005 | Oktalite_Canilo_WH3500 | 24 VA | 10161669 | 10125193 | 2930 lm |
| CANILO  3P 05 LED3000-835 SP-c ET 05 | 24 VA | Spot | 85 | clear | CANILO_LED_SP.ies | LED | 3500 K | LED | 3000 lm | RAL 9005 jet black | Oktalite_Alu_RAL_9005 | Oktalite_Canilo_WH3500 | 24 VA | 10161669 | 10127062 | 2930 lm |
| CANILO  3P 05 LED3000-835 SP  ET 05 | 24 VA | Spot | 85 | without | CANILO_LED_SP.ies | LED | 3500 K | LED | 3000 lm | RAL 9005 jet black | Oktalite_Alu_RAL_9005 | Oktalite_Canilo_WH3500 | 24 VA | 10161669 | 10125190 | 2930 lm |
| CANILO  3P 05 LED3000-835 VFL-c ET 03 | 24 VA | Very Wide Flood | 85 | clear | CANILO_LED_VFL.ies | LED | 3500 K | LED | 3000 lm | RAL 9006 white aluminium | Oktalite_Alu_RAL_9006 | Oktalite_Canilo_WH3500 | 24 VA | 10161668 | 10147536 | 2930 lm |
| CANILO  3P 05 LED3000-835 VFL  ET 03 | 24 VA | Very Wide Flood | 85 | without | CANILO_LED_VFL.ies | LED | 3500 K | LED | 3000 lm | RAL 9006 white aluminium | Oktalite_Alu_RAL_9006 | Oktalite_Canilo_WH3500 | 24 VA | 10161668 | 10147502 | 2930 lm |
| CANILO  3P 05 LED3000-835 WFL-c ET 03 | 24 VA | Wide Flood | 85 | clear | CANILO_LED_WFL.ies | LED | 3500 K | LED | 3000 lm | RAL 9006 white aluminium | Oktalite_Alu_RAL_9006 | Oktalite_Canilo_WH3500 | 24 VA | 10161668 | 10147535 | 2930 lm |
| CANILO  3P 05 LED3000-835 WFL  ET 03 | 24 VA | Wide Flood | 85 | without | CANILO_LED_WFL.ies | LED | 3500 K | LED | 3000 lm | RAL 9006 white aluminium | Oktalite_Alu_RAL_9006 | Oktalite_Canilo_WH3500 | 24 VA | 10161668 | 10147501 | 2930 lm |
| CANILO  3P 05 LED3000-835 FL-c ET 03 | 24 VA | Flood | 85 | clear | CANILO_LED_FL.ies | LED | 3500 K | LED | 3000 lm | RAL 9006 white aluminium | Oktalite_Alu_RAL_9006 | Oktalite_Canilo_WH3500 | 24 VA | 10161668 | 10127064 | 2930 lm |
| CANILO  3P 05 LED3000-835 FL  ET 03 | 24 VA | Flood | 85 | without | CANILO_LED_FL.ies | LED | 3500 K | LED | 3000 lm | RAL 9006 white aluminium | Oktalite_Alu_RAL_9006 | Oktalite_Canilo_WH3500 | 24 VA | 10161668 | 10125196 | 2930 lm |
| CANILO  3P 05 LED3000-835 MF-c ET 03 | 24 VA | Medium Flood | 85 | clear | CANILO_LED_MF.ies | LED | 3500 K | LED | 3000 lm | RAL 9006 white aluminium | Oktalite_Alu_RAL_9006 | Oktalite_Canilo_WH3500 | 24 VA | 10161668 | 10127063 | 2930 lm |
| CANILO  3P 05 LED3000-835 MF  ET 03 | 24 VA | Medium Flood | 85 | without | CANILO_LED_MF.ies | LED | 3500 K | LED | 3000 lm | RAL 9006 white aluminium | Oktalite_Alu_RAL_9006 | Oktalite_Canilo_WH3500 | 24 VA | 10161668 | 10125193 | 2930 lm |
| CANILO  3P 05 LED3000-835 SP-c ET 03 | 24 VA | Spot | 85 | clear | CANILO_LED_SP.ies | LED | 3500 K | LED | 3000 lm | RAL 9006 white aluminium | Oktalite_Alu_RAL_9006 | Oktalite_Canilo_WH3500 | 24 VA | 10161668 | 10127062 | 2930 lm |
| CANILO  3P 05 LED3000-835 SP  ET 03 | 24 VA | Spot | 85 | without | CANILO_LED_SP.ies | LED | 3500 K | LED | 3000 lm | RAL 9006 white aluminium | Oktalite_Alu_RAL_9006 | Oktalite_Canilo_WH3500 | 24 VA | 10161668 | 10125190 | 2930 lm |
| CANILO  3P 01 LED3000-835 VFL-c ET 01 | 24 VA | Very Wide Flood | 85 | clear | CANILO_LED_VFL.ies | LED | 3500 K | LED | 3000 lm | RAL 9016 traffic white | Oktalite_Alu_RAL_9016 | Oktalite_Canilo_WH3500 | 24 VA | 10161667 | 10147536 | 2930 lm |
| CANILO  3P 01 LED3000-835 VFL  ET 01 | 24 VA | Very Wide Flood | 85 | without | CANILO_LED_VFL.ies | LED | 3500 K | LED | 3000 lm | RAL 9016 traffic white | Oktalite_Alu_RAL_9016 | Oktalite_Canilo_WH3500 | 24 VA | 10161667 | 10147502 | 2930 lm |
| CANILO  3P 01 LED3000-835 WFL-c ET 01 | 24 VA | Wide Flood | 85 | clear | CANILO_LED_WFL.ies | LED | 3500 K | LED | 3000 lm | RAL 9016 traffic white | Oktalite_Alu_RAL_9016 | Oktalite_Canilo_WH3500 | 24 VA | 10161667 | 10147535 | 2930 lm |
| CANILO  3P 01 LED3000-835 WFL  ET 01 | 24 VA | Wide Flood | 85 | without | CANILO_LED_WFL.ies | LED | 3500 K | LED | 3000 lm | RAL 9016 traffic white | Oktalite_Alu_RAL_9016 | Oktalite_Canilo_WH3500 | 24 VA | 10161667 | 10147501 | 2930 lm |
| CANILO  3P 01 LED3000-835 FL-c ET 01 | 24 VA | Flood | 85 | clear | CANILO_LED_FL.ies | LED | 3500 K | LED | 3000 lm | RAL 9016 traffic white | Oktalite_Alu_RAL_9016 | Oktalite_Canilo_WH3500 | 24 VA | 10161667 | 10127064 | 2930 lm |
| CANILO  3P 01 LED3000-835 FL  ET 01 | 24 VA | Flood | 85 | without | CANILO_LED_FL.ies | LED | 3500 K | LED | 3000 lm | RAL 9016 traffic white | Oktalite_Alu_RAL_9016 | Oktalite_Canilo_WH3500 | 24 VA | 10161667 | 10125196 | 2930 lm |
| CANILO  3P 01 LED3000-835 MF-c ET 01 | 24 VA | Medium Flood | 85 | clear | CANILO_LED_MF.ies | LED | 3500 K | LED | 3000 lm | RAL 9016 traffic white | Oktalite_Alu_RAL_9016 | Oktalite_Canilo_WH3500 | 24 VA | 10161667 | 10127063 | 2930 lm |
| CANILO  3P 01 LED3000-835 MF  ET 01 | 24 VA | Medium Flood | 85 | without | CANILO_LED_MF.ies | LED | 3500 K | LED | 3000 lm | RAL 9016 traffic white | Oktalite_Alu_RAL_9016 | Oktalite_Canilo_WH3500 | 24 VA | 10161667 | 10125193 | 2930 lm |
| CANILO  3P 01 LED3000-835 SP-c ET 01 | 24 VA | Spot | 85 | clear | CANILO_LED_SP.ies | LED | 3500 K | LED | 3000 lm | RAL 9016 traffic white | Oktalite_Alu_RAL_9016 | Oktalite_Canilo_WH3500 | 24 VA | 10161667 | 10127062 | 2930 lm |
| CANILO  3P 01 LED3000-835 SP  ET 01 | 24 VA | Spot | 85 | without | CANILO_LED_SP.ies | LED | 3500 K | LED | 3000 lm | RAL 9016 traffic white | Oktalite_Alu_RAL_9016 | Oktalite_Canilo_WH3500 | 24 VA | 10161667 | 10125190 | 2930 lm |
| CANILO  3P 05 LED3000-830 VFL-c ET 05 | 24 VA | Very Wide Flood | 85 | clear | CANILO_LED_VFL.ies | LED | 3000 K | LED | 3000 lm | RAL 9005 jet black | Oktalite_Alu_RAL_9005 | Oktalite_Canilo_WH3000 | 24 VA | 10161663 | 10147536 | 2895 lm |
| CANILO  3P 05 LED3000-830 VFL  ET 05 | 24 VA | Very Wide Flood | 85 | without | CANILO_LED_VFL.ies | LED | 3000 K | LED | 3000 lm | RAL 9005 jet black | Oktalite_Alu_RAL_9005 | Oktalite_Canilo_WH3000 | 24 VA | 10161663 | 10147502 | 2895 lm |
| CANILO  3P 05 LED3000-830 WFL-c ET 05 | 24 VA | Wide Flood | 85 | clear | CANILO_LED_WFL.ies | LED | 3000 K | LED | 3000 lm | RAL 9005 jet black | Oktalite_Alu_RAL_9005 | Oktalite_Canilo_WH3000 | 24 VA | 10161663 | 10147535 | 2895 lm |
| CANILO  3P 05 LED3000-830 WFL  ET 05 | 24 VA | Wide Flood | 85 | without | CANILO_LED_WFL.ies | LED | 3000 K | LED | 3000 lm | RAL 9005 jet black | Oktalite_Alu_RAL_9005 | Oktalite_Canilo_WH3000 | 24 VA | 10161663 | 10147501 | 2895 lm |
| CANILO  3P 05 LED3000-830 FL-c ET 05 | 24 VA | Flood | 85 | clear | CANILO_LED_FL.ies | LED | 3000 K | LED | 3000 lm | RAL 9005 jet black | Oktalite_Alu_RAL_9005 | Oktalite_Canilo_WH3000 | 24 VA | 10161663 | 10127064 | 2895 lm |
| CANILO  3P 05 LED3000-830 FL  ET 05 | 24 VA | Flood | 85 | without | CANILO_LED_FL.ies | LED | 3000 K | LED | 3000 lm | RAL 9005 jet black | Oktalite_Alu_RAL_9005 | Oktalite_Canilo_WH3000 | 24 VA | 10161663 | 10125196 | 2895 lm |
| CANILO  3P 05 LED3000-830 MF-c ET 05 | 24 VA | Medium Flood | 85 | clear | CANILO_LED_MF.ies | LED | 3000 K | LED | 3000 lm | RAL 9005 jet black | Oktalite_Alu_RAL_9005 | Oktalite_Canilo_WH3000 | 24 VA | 10161663 | 10127063 | 2895 lm |
| CANILO  3P 05 LED3000-830 MF  ET 05 | 24 VA | Medium Flood | 85 | without | CANILO_LED_MF.ies | LED | 3000 K | LED | 3000 lm | RAL 9005 jet black | Oktalite_Alu_RAL_9005 | Oktalite_Canilo_WH3000 | 24 VA | 10161663 | 10125193 | 2895 lm |
| CANILO  3P 05 LED3000-830 SP-c ET 05 | 24 VA | Spot | 85 | clear | CANILO_LED_SP.ies | LED | 3000 K | LED | 3000 lm | RAL 9005 jet black | Oktalite_Alu_RAL_9005 | Oktalite_Canilo_WH3000 | 24 VA | 10161663 | 10127062 | 2895 lm |
| CANILO  3P 05 LED3000-830 SP  ET 05 | 24 VA | Spot | 85 | without | CANILO_LED_SP.ies | LED | 3000 K | LED | 3000 lm | RAL 9005 jet black | Oktalite_Alu_RAL_9005 | Oktalite_Canilo_WH3000 | 24 VA | 10161663 | 10125190 | 2895 lm |
| CANILO  3P 05 LED3000-830 VFL-c ET 03 | 24 VA | Very Wide Flood | 85 | clear | CANILO_LED_VFL.ies | LED | 3000 K | LED | 3000 lm | RAL 9006 white aluminium | Oktalite_Alu_RAL_9006 | Oktalite_Canilo_WH3000 | 24 VA | 10161662 | 10147536 | 2895 lm |
| CANILO  3P 05 LED3000-830 VFL  ET 03 | 24 VA | Very Wide Flood | 85 | without | CANILO_LED_VFL.ies | LED | 3000 K | LED | 3000 lm | RAL 9006 white aluminium | Oktalite_Alu_RAL_9006 | Oktalite_Canilo_WH3000 | 24 VA | 10161662 | 10147502 | 2895 lm |
| CANILO  3P 05 LED3000-830 WFL-c ET 03 | 24 VA | Wide Flood | 85 | clear | CANILO_LED_WFL.ies | LED | 3000 K | LED | 3000 lm | RAL 9006 white aluminium | Oktalite_Alu_RAL_9006 | Oktalite_Canilo_WH3000 | 24 VA | 10161662 | 10147535 | 2895 lm |
| CANILO  3P 05 LED3000-830 WFL  ET 03 | 24 VA | Wide Flood | 85 | without | CANILO_LED_WFL.ies | LED | 3000 K | LED | 3000 lm | RAL 9006 white aluminium | Oktalite_Alu_RAL_9006 | Oktalite_Canilo_WH3000 | 24 VA | 10161662 | 10147501 | 2895 lm |
| CANILO  3P 05 LED3000-830 FL-c ET 03 | 24 VA | Flood | 85 | clear | CANILO_LED_FL.ies | LED | 3000 K | LED | 3000 lm | RAL 9006 white aluminium | Oktalite_Alu_RAL_9006 | Oktalite_Canilo_WH3000 | 24 VA | 10161662 | 10127064 | 2895 lm |
| CANILO  3P 05 LED3000-830 FL  ET 03 | 24 VA | Flood | 85 | without | CANILO_LED_FL.ies | LED | 3000 K | LED | 3000 lm | RAL 9006 white aluminium | Oktalite_Alu_RAL_9006 | Oktalite_Canilo_WH3000 | 24 VA | 10161662 | 10125196 | 2895 lm |
| CANILO  3P 05 LED3000-830 MF-c ET 03 | 24 VA | Medium Flood | 85 | clear | CANILO_LED_MF.ies | LED | 3000 K | LED | 3000 lm | RAL 9006 white aluminium | Oktalite_Alu_RAL_9006 | Oktalite_Canilo_WH3000 | 24 VA | 10161662 | 10127063 | 2895 lm |
| CANILO  3P 05 LED3000-830 MF  ET 03 | 24 VA | Medium Flood | 85 | without | CANILO_LED_MF.ies | LED | 3000 K | LED | 3000 lm | RAL 9006 white aluminium | Oktalite_Alu_RAL_9006 | Oktalite_Canilo_WH3000 | 24 VA | 10161662 | 10125193 | 2895 lm |
| CANILO  3P 05 LED3000-830 SP-c ET 03 | 24 VA | Spot | 85 | clear | CANILO_LED_SP.ies | LED | 3000 K | LED | 3000 lm | RAL 9006 white aluminium | Oktalite_Alu_RAL_9006 | Oktalite_Canilo_WH3000 | 24 VA | 10161662 | 10127062 | 2895 lm |
| CANILO  3P 05 LED3000-830 SP  ET 03 | 24 VA | Spot | 85 | without | CANILO_LED_SP.ies | LED | 3000 K | LED | 3000 lm | RAL 9006 white aluminium | Oktalite_Alu_RAL_9006 | Oktalite_Canilo_WH3000 | 24 VA | 10161662 | 10125190 | 2895 lm |
| CANILO  3P 01 LED3000-830 VFL-c ET 01 | 24 VA | Very Wide Flood | 85 | clear | CANILO_LED_VFL.ies | LED | 3000 K | LED | 3000 lm | RAL 9016 traffic white | Oktalite_Alu_RAL_9016 | Oktalite_Canilo_WH3000 | 24 VA | 10161661 | 10147536 | 2895 lm |
| CANILO  3P 01 LED3000-830 VFL  ET 01 | 24 VA | Very Wide Flood | 85 | without | CANILO_LED_VFL.ies | LED | 3000 K | LED | 3000 lm | RAL 9016 traffic white | Oktalite_Alu_RAL_9016 | Oktalite_Canilo_WH3000 | 24 VA | 10161661 | 10147502 | 2895 lm |
| CANILO  3P 01 LED3000-830 WFL-c ET 01 | 24 VA | Wide Flood | 85 | clear | CANILO_LED_WFL.ies | LED | 3000 K | LED | 3000 lm | RAL 9016 traffic white | Oktalite_Alu_RAL_9016 | Oktalite_Canilo_WH3000 | 24 VA | 10161661 | 10147535 | 2895 lm |
| CANILO  3P 01 LED3000-830 WFL  ET 01 | 24 VA | Wide Flood | 85 | without | CANILO_LED_WFL.ies | LED | 3000 K | LED | 3000 lm | RAL 9016 traffic white | Oktalite_Alu_RAL_9016 | Oktalite_Canilo_WH3000 | 24 VA | 10161661 | 10147501 | 2895 lm |
| CANILO  3P 01 LED3000-830 FL-c ET 01 | 24 VA | Flood | 85 | clear | CANILO_LED_FL.ies | LED | 3000 K | LED | 3000 lm | RAL 9016 traffic white | Oktalite_Alu_RAL_9016 | Oktalite_Canilo_WH3000 | 24 VA | 10161661 | 10127064 | 2895 lm |
| CANILO  3P 01 LED3000-830 FL  ET 01 | 24 VA | Flood | 85 | without | CANILO_LED_FL.ies | LED | 3000 K | LED | 3000 lm | RAL 9016 traffic white | Oktalite_Alu_RAL_9016 | Oktalite_Canilo_WH3000 | 24 VA | 10161661 | 10125196 | 2895 lm |
| CANILO  3P 01 LED3000-830 MF-c ET 01 | 24 VA | Medium Flood | 85 | clear | CANILO_LED_MF.ies | LED | 3000 K | LED | 3000 lm | RAL 9016 traffic white | Oktalite_Alu_RAL_9016 | Oktalite_Canilo_WH3000 | 24 VA | 10161661 | 10127063 | 2895 lm |
| CANILO  3P 01 LED3000-830 MF  ET 01 | 24 VA | Medium Flood | 85 | without | CANILO_LED_MF.ies | LED | 3000 K | LED | 3000 lm | RAL 9016 traffic white | Oktalite_Alu_RAL_9016 | Oktalite_Canilo_WH3000 | 24 VA | 10161661 | 10125193 | 2895 lm |
| CANILO  3P 01 LED3000-830 SP-c ET 01 | 24 VA | Spot | 85 | clear | CANILO_LED_SP.ies | LED | 3000 K | LED | 3000 lm | RAL 9016 traffic white | Oktalite_Alu_RAL_9016 | Oktalite_Canilo_WH3000 | 24 VA | 10161661 | 10127062 | 2895 lm |
| CANILO  3P 01 LED3000-830 SP  ET 01 | 24 VA | Spot | 85 | without | CANILO_LED_SP.ies | LED | 3000 K | LED | 3000 lm | RAL 9016 traffic white | Oktalite_Alu_RAL_9016 | Oktalite_Canilo_WH3000 | 24 VA | 10161661 | 10125190 | 2895 lm |
| CANILO  3P 05 LED3000-827 VFL-c ET 05 | 24 VA | Very Wide Flood | 82 | clear | CANILO_LED_VFL.ies | LED | 2700 K | LED | 3000 lm | RAL 9005 jet black | Oktalite_Alu_RAL_9005 | Oktalite_Canilo_WH2700 | 24 VA | 10161660 | 10147536 | 2690 lm |
| CANILO  3P 05 LED3000-827 VFL  ET 05 | 24 VA | Very Wide Flood | 82 | without | CANILO_LED_VFL.ies | LED | 2700 K | LED | 3000 lm | RAL 9005 jet black | Oktalite_Alu_RAL_9005 | Oktalite_Canilo_WH2700 | 24 VA | 10161660 | 10147502 | 2690 lm |
| CANILO  3P 05 LED3000-827 WFL-c ET 05 | 24 VA | Wide Flood | 82 | clear | CANILO_LED_WFL.ies | LED | 2700 K | LED | 3000 lm | RAL 9005 jet black | Oktalite_Alu_RAL_9005 | Oktalite_Canilo_WH2700 | 24 VA | 10161660 | 10147535 | 2690 lm |
| CANILO  3P 05 LED3000-827 WFL  ET 05 | 24 VA | Wide Flood | 82 | without | CANILO_LED_WFL.ies | LED | 2700 K | LED | 3000 lm | RAL 9005 jet black | Oktalite_Alu_RAL_9005 | Oktalite_Canilo_WH2700 | 24 VA | 10161660 | 10147501 | 2690 lm |
| CANILO  3P 05 LED3000-827 FL-c ET 05 | 24 VA | Flood | 82 | clear | CANILO_LED_FL.ies | LED | 2700 K | LED | 3000 lm | RAL 9005 jet black | Oktalite_Alu_RAL_9005 | Oktalite_Canilo_WH2700 | 24 VA | 10161660 | 10127064 | 2690 lm |
| CANILO  3P 05 LED3000-827 FL  ET 05 | 24 VA | Flood | 82 | without | CANILO_LED_FL.ies | LED | 2700 K | LED | 3000 lm | RAL 9005 jet black | Oktalite_Alu_RAL_9005 | Oktalite_Canilo_WH2700 | 24 VA | 10161660 | 10125196 | 2690 lm |
| CANILO  3P 05 LED3000-827 MF-c ET 05 | 24 VA | Medium Flood | 82 | clear | CANILO_LED_MF.ies | LED | 2700 K | LED | 3000 lm | RAL 9005 jet black | Oktalite_Alu_RAL_9005 | Oktalite_Canilo_WH2700 | 24 VA | 10161660 | 10127063 | 2690 lm |
| CANILO  3P 05 LED3000-827 MF  ET 05 | 24 VA | Medium Flood | 82 | without | CANILO_LED_MF.ies | LED | 2700 K | LED | 3000 lm | RAL 9005 jet black | Oktalite_Alu_RAL_9005 | Oktalite_Canilo_WH2700 | 24 VA | 10161660 | 10125193 | 2690 lm |
| CANILO  3P 05 LED3000-827 SP-c ET 05 | 24 VA | Spot | 82 | clear | CANILO_LED_SP.ies | LED | 2700 K | LED | 3000 lm | RAL 9005 jet black | Oktalite_Alu_RAL_9005 | Oktalite_Canilo_WH2700 | 24 VA | 10161660 | 10127062 | 2690 lm |
| CANILO  3P 05 LED3000-827 SP  ET 05 | 24 VA | Spot | 82 | without | CANILO_LED_SP.ies | LED | 2700 K | LED | 3000 lm | RAL 9005 jet black | Oktalite_Alu_RAL_9005 | Oktalite_Canilo_WH2700 | 24 VA | 10161660 | 10125190 | 2690 lm |
| CANILO  3P 05 LED3000-827 VFL-c ET 03 | 24 VA | Very Wide Flood | 82 | clear | CANILO_LED_VFL.ies | LED | 2700 K | LED | 3000 lm | RAL 9006 white aluminium | Oktalite_Alu_RAL_9006 | Oktalite_Canilo_WH2700 | 24 VA | 10161659 | 10147536 | 2690 lm |
| CANILO  3P 05 LED3000-827 VFL  ET 03 | 24 VA | Very Wide Flood | 82 | without | CANILO_LED_VFL.ies | LED | 2700 K | LED | 3000 lm | RAL 9006 white aluminium | Oktalite_Alu_RAL_9006 | Oktalite_Canilo_WH2700 | 24 VA | 10161659 | 10147502 | 2690 lm |
| CANILO  3P 05 LED3000-827 WFL-c ET 03 | 24 VA | Wide Flood | 82 | clear | CANILO_LED_WFL.ies | LED | 2700 K | LED | 3000 lm | RAL 9006 white aluminium | Oktalite_Alu_RAL_9006 | Oktalite_Canilo_WH2700 | 24 VA | 10161659 | 10147535 | 2690 lm |
| CANILO  3P 05 LED3000-827 WFL  ET 03 | 24 VA | Wide Flood | 82 | without | CANILO_LED_WFL.ies | LED | 2700 K | LED | 3000 lm | RAL 9006 white aluminium | Oktalite_Alu_RAL_9006 | Oktalite_Canilo_WH2700 | 24 VA | 10161659 | 10147501 | 2690 lm |
| CANILO  3P 05 LED3000-827 FL-c ET 03 | 24 VA | Flood | 82 | clear | CANILO_LED_FL.ies | LED | 2700 K | LED | 3000 lm | RAL 9006 white aluminium | Oktalite_Alu_RAL_9006 | Oktalite_Canilo_WH2700 | 24 VA | 10161659 | 10127064 | 2690 lm |
| CANILO  3P 05 LED3000-827 FL  ET 03 | 24 VA | Flood | 82 | without | CANILO_LED_FL.ies | LED | 2700 K | LED | 3000 lm | RAL 9006 white aluminium | Oktalite_Alu_RAL_9006 | Oktalite_Canilo_WH2700 | 24 VA | 10161659 | 10125196 | 2690 lm |
| CANILO  3P 05 LED3000-827 MF-c ET 03 | 24 VA | Medium Flood | 82 | clear | CANILO_LED_MF.ies | LED | 2700 K | LED | 3000 lm | RAL 9006 white aluminium | Oktalite_Alu_RAL_9006 | Oktalite_Canilo_WH2700 | 24 VA | 10161659 | 10127063 | 2690 lm |
| CANILO  3P 05 LED3000-827 MF  ET 03 | 24 VA | Medium Flood | 82 | without | CANILO_LED_MF.ies | LED | 2700 K | LED | 3000 lm | RAL 9006 white aluminium | Oktalite_Alu_RAL_9006 | Oktalite_Canilo_WH2700 | 24 VA | 10161659 | 10125193 | 2690 lm |
| CANILO  3P 05 LED3000-827 SP-c ET 03 | 24 VA | Spot | 82 | clear | CANILO_LED_SP.ies | LED | 2700 K | LED | 3000 lm | RAL 9006 white aluminium | Oktalite_Alu_RAL_9006 | Oktalite_Canilo_WH2700 | 24 VA | 10161659 | 10127062 | 2690 lm |
| CANILO  3P 05 LED3000-827 SP  ET 03 | 24 VA | Spot | 82 | without | CANILO_LED_SP.ies | LED | 2700 K | LED | 3000 lm | RAL 9006 white aluminium | Oktalite_Alu_RAL_9006 | Oktalite_Canilo_WH2700 | 24 VA | 10161659 | 10125190 | 2690 lm |
| CANILO  3P 01 LED3000-827 VFL-c ET 01 | 24 VA | Very Wide Flood | 82 | clear | CANILO_LED_VFL.ies | LED | 2700 K | LED | 3000 lm | RAL 9016 traffic white | Oktalite_Alu_RAL_9016 | Oktalite_Canilo_WH2700 | 24 VA | 10161658 | 10147536 | 2690 lm |
| CANILO  3P 01 LED3000-827 VFL  ET 01 | 24 VA | Very Wide Flood | 82 | without | CANILO_LED_VFL.ies | LED | 2700 K | LED | 3000 lm | RAL 9016 traffic white | Oktalite_Alu_RAL_9016 | Oktalite_Canilo_WH2700 | 24 VA | 10161658 | 10147502 | 2690 lm |
| CANILO  3P 01 LED3000-827 WFL-c ET 01 | 24 VA | Wide Flood | 82 | clear | CANILO_LED_WFL.ies | LED | 2700 K | LED | 3000 lm | RAL 9016 traffic white | Oktalite_Alu_RAL_9016 | Oktalite_Canilo_WH2700 | 24 VA | 10161658 | 10147535 | 2690 lm |
| CANILO  3P 01 LED3000-827 WFL  ET 01 | 24 VA | Wide Flood | 82 | without | CANILO_LED_WFL.ies | LED | 2700 K | LED | 3000 lm | RAL 9016 traffic white | Oktalite_Alu_RAL_9016 | Oktalite_Canilo_WH2700 | 24 VA | 10161658 | 10147501 | 2690 lm |
| CANILO  3P 01 LED3000-827 FL-c ET 01 | 24 VA | Flood | 82 | clear | CANILO_LED_FL.ies | LED | 2700 K | LED | 3000 lm | RAL 9016 traffic white | Oktalite_Alu_RAL_9016 | Oktalite_Canilo_WH2700 | 24 VA | 10161658 | 10127064 | 2690 lm |
| CANILO  3P 01 LED3000-827 FL  ET 01 | 24 VA | Flood | 82 | without | CANILO_LED_FL.ies | LED | 2700 K | LED | 3000 lm | RAL 9016 traffic white | Oktalite_Alu_RAL_9016 | Oktalite_Canilo_WH2700 | 24 VA | 10161658 | 10125196 | 2690 lm |
| CANILO  3P 01 LED3000-827 MF-c ET 01 | 24 VA | Medium Flood | 82 | clear | CANILO_LED_MF.ies | LED | 2700 K | LED | 3000 lm | RAL 9016 traffic white | Oktalite_Alu_RAL_9016 | Oktalite_Canilo_WH2700 | 24 VA | 10161658 | 10127063 | 2690 lm |
| CANILO  3P 01 LED3000-827 MF  ET 01 | 24 VA | Medium Flood | 82 | without | CANILO_LED_MF.ies | LED | 2700 K | LED | 3000 lm | RAL 9016 traffic white | Oktalite_Alu_RAL_9016 | Oktalite_Canilo_WH2700 | 24 VA | 10161658 | 10125193 | 2690 lm |
| CANILO  3P 01 LED3000-827 SP-c ET 01 | 24 VA | Spot | 82 | clear | CANILO_LED_SP.ies | LED | 2700 K | LED | 3000 lm | RAL 9016 traffic white | Oktalite_Alu_RAL_9016 | Oktalite_Canilo_WH2700 | 24 VA | 10161658 | 10127062 | 2690 lm |
| CANILO  3P 01 LED3000-827 SP  ET 01 | 24 VA | Spot | 82 | without | CANILO_LED_SP.ies | LED | 2700 K | LED | 3000 lm | RAL 9016 traffic white | Oktalite_Alu_RAL_9016 | Oktalite_Canilo_WH2700 | 24 VA | 10161658 | 10125190 | 2690 lm |
| CANILO  3P 05 LED3000-BVC VFL-c ET 05 | 31 VA | Very Wide Flood | - | clear | CANILO_LED_VFL.ies | LED | B+V+C | LED | 3000 lm | RAL 9005 jet black | Oktalite_Alu_RAL_9005 | Oktalite_Canilo_WH3100 | 31 VA | 10161314 | 10147536 | 2860 lm |
| CANILO  3P 05 LED3000-BVC VFL  ET 05 | 31 VA | Very Wide Flood | - | without | CANILO_LED_VFL.ies | LED | B+V+C | LED | 3000 lm | RAL 9005 jet black | Oktalite_Alu_RAL_9005 | Oktalite_Canilo_WH3100 | 31 VA | 10161314 | 10147502 | 2860 lm |
| CANILO  3P 05 LED3000-BVC WFL-c ET 05 | 31 VA | Wide Flood | - | clear | CANILO_LED_WFL.ies | LED | B+V+C | LED | 3000 lm | RAL 9005 jet black | Oktalite_Alu_RAL_9005 | Oktalite_Canilo_WH3100 | 31 VA | 10161314 | 10147535 | 2860 lm |
| CANILO  3P 05 LED3000-BVC WFL  ET 05 | 31 VA | Wide Flood | - | without | CANILO_LED_WFL.ies | LED | B+V+C | LED | 3000 lm | RAL 9005 jet black | Oktalite_Alu_RAL_9005 | Oktalite_Canilo_WH3100 | 31 VA | 10161314 | 10147501 | 2860 lm |
| CANILO  3P 05 LED3000-BVC FL-c ET 05 | 31 VA | Flood | - | clear | CANILO_LED_FL.ies | LED | B+V+C | LED | 3000 lm | RAL 9005 jet black | Oktalite_Alu_RAL_9005 | Oktalite_Canilo_WH3100 | 31 VA | 10161314 | 10127064 | 2860 lm |
| CANILO  3P 05 LED3000-BVC FL  ET 05 | 31 VA | Flood | - | without | CANILO_LED_FL.ies | LED | B+V+C | LED | 3000 lm | RAL 9005 jet black | Oktalite_Alu_RAL_9005 | Oktalite_Canilo_WH3100 | 31 VA | 10161314 | 10125196 | 2860 lm |
| CANILO  3P 05 LED3000-BVC MF-c ET 05 | 31 VA | Medium Flood | - | clear | CANILO_LED_MF.ies | LED | B+V+C | LED | 3000 lm | RAL 9005 jet black | Oktalite_Alu_RAL_9005 | Oktalite_Canilo_WH3100 | 31 VA | 10161314 | 10127063 | 2860 lm |
| CANILO  3P 05 LED3000-BVC MF  ET 05 | 31 VA | Medium Flood | - | without | CANILO_LED_MF.ies | LED | B+V+C | LED | 3000 lm | RAL 9005 jet black | Oktalite_Alu_RAL_9005 | Oktalite_Canilo_WH3100 | 31 VA | 10161314 | 10125193 | 2860 lm |
| CANILO  3P 05 LED3000-BVC SP-c ET 05 | 31 VA | Spot | - | clear | CANILO_LED_SP.ies | LED | B+V+C | LED | 3000 lm | RAL 9005 jet black | Oktalite_Alu_RAL_9005 | Oktalite_Canilo_WH3100 | 31 VA | 10161314 | 10127062 | 2860 lm |
| CANILO  3P 05 LED3000-BVC SP  ET 05 | 31 VA | Spot | - | without | CANILO_LED_SP.ies | LED | B+V+C | LED | 3000 lm | RAL 9005 jet black | Oktalite_Alu_RAL_9005 | Oktalite_Canilo_WH3100 | 31 VA | 10161314 | 10125190 | 2860 lm |
| CANILO  3P 05 LED3000-BVC VFL-c ET 03 | 31 VA | Very Wide Flood | - | clear | CANILO_LED_VFL.ies | LED | B+V+C | LED | 3000 lm | RAL 9006 white aluminium | Oktalite_Alu_RAL_9006 | Oktalite_Canilo_WH3100 | 31 VA | 10161313 | 10147536 | 2860 lm |
| CANILO  3P 05 LED3000-BVC VFL  ET 03 | 31 VA | Very Wide Flood | - | without | CANILO_LED_VFL.ies | LED | B+V+C | LED | 3000 lm | RAL 9006 white aluminium | Oktalite_Alu_RAL_9006 | Oktalite_Canilo_WH3100 | 31 VA | 10161313 | 10147502 | 2860 lm |
| CANILO  3P 05 LED3000-BVC WFL-c ET 03 | 31 VA | Wide Flood | - | clear | CANILO_LED_WFL.ies | LED | B+V+C | LED | 3000 lm | RAL 9006 white aluminium | Oktalite_Alu_RAL_9006 | Oktalite_Canilo_WH3100 | 31 VA | 10161313 | 10147535 | 2860 lm |
| CANILO  3P 05 LED3000-BVC WFL  ET 03 | 31 VA | Wide Flood | - | without | CANILO_LED_WFL.ies | LED | B+V+C | LED | 3000 lm | RAL 9006 white aluminium | Oktalite_Alu_RAL_9006 | Oktalite_Canilo_WH3100 | 31 VA | 10161313 | 10147501 | 2860 lm |
| CANILO  3P 05 LED3000-BVC FL-c ET 03 | 31 VA | Flood | - | clear | CANILO_LED_FL.ies | LED | B+V+C | LED | 3000 lm | RAL 9006 white aluminium | Oktalite_Alu_RAL_9006 | Oktalite_Canilo_WH3100 | 31 VA | 10161313 | 10127064 | 2860 lm |
| CANILO  3P 05 LED3000-BVC FL  ET 03 | 31 VA | Flood | - | without | CANILO_LED_FL.ies | LED | B+V+C | LED | 3000 lm | RAL 9006 white aluminium | Oktalite_Alu_RAL_9006 | Oktalite_Canilo_WH3100 | 31 VA | 10161313 | 10125196 | 2860 lm |
| CANILO  3P 05 LED3000-BVC MF-c ET 03 | 31 VA | Medium Flood | - | clear | CANILO_LED_MF.ies | LED | B+V+C | LED | 3000 lm | RAL 9006 white aluminium | Oktalite_Alu_RAL_9006 | Oktalite_Canilo_WH3100 | 31 VA | 10161313 | 10127063 | 2860 lm |
| CANILO  3P 05 LED3000-BVC MF  ET 03 | 31 VA | Medium Flood | - | without | CANILO_LED_MF.ies | LED | B+V+C | LED | 3000 lm | RAL 9006 white aluminium | Oktalite_Alu_RAL_9006 | Oktalite_Canilo_WH3100 | 31 VA | 10161313 | 10125193 | 2860 lm |
| CANILO  3P 05 LED3000-BVC SP-c ET 03 | 31 VA | Spot | - | clear | CANILO_LED_SP.ies | LED | B+V+C | LED | 3000 lm | RAL 9006 white aluminium | Oktalite_Alu_RAL_9006 | Oktalite_Canilo_WH3100 | 31 VA | 10161313 | 10127062 | 2860 lm |
| CANILO  3P 05 LED3000-BVC SP  ET 03 | 31 VA | Spot | - | without | CANILO_LED_SP.ies | LED | B+V+C | LED | 3000 lm | RAL 9006 white aluminium | Oktalite_Alu_RAL_9006 | Oktalite_Canilo_WH3100 | 31 VA | 10161313 | 10125190 | 2860 lm |
| CANILO  3P 01 LED3000-BVC VFL-c ET 01 | 31 VA | Very Wide Flood | - | clear | CANILO_LED_VFL.ies | LED | B+V+C | LED | 3000 lm | RAL 9016 traffic white | Oktalite_Alu_RAL_9016 | Oktalite_Canilo_WH3100 | 31 VA | 10161312 | 10147536 | 2860 lm |
| CANILO  3P 01 LED3000-BVC VFL  ET 01 | 31 VA | Very Wide Flood | - | without | CANILO_LED_VFL.ies | LED | B+V+C | LED | 3000 lm | RAL 9016 traffic white | Oktalite_Alu_RAL_9016 | Oktalite_Canilo_WH3100 | 31 VA | 10161312 | 10147502 | 2860 lm |
| CANILO  3P 01 LED3000-BVC WFL-c ET 01 | 31 VA | Wide Flood | - | clear | CANILO_LED_WFL.ies | LED | B+V+C | LED | 3000 lm | RAL 9016 traffic white | Oktalite_Alu_RAL_9016 | Oktalite_Canilo_WH3100 | 31 VA | 10161312 | 10147535 | 2860 lm |
| CANILO  3P 01 LED3000-BVC WFL  ET 01 | 31 VA | Wide Flood | - | without | CANILO_LED_WFL.ies | LED | B+V+C | LED | 3000 lm | RAL 9016 traffic white | Oktalite_Alu_RAL_9016 | Oktalite_Canilo_WH3100 | 31 VA | 10161312 | 10147501 | 2860 lm |
| CANILO  3P 01 LED3000-BVC FL-c ET 01 | 31 VA | Flood | - | clear | CANILO_LED_FL.ies | LED | B+V+C | LED | 3000 lm | RAL 9016 traffic white | Oktalite_Alu_RAL_9016 | Oktalite_Canilo_WH3100 | 31 VA | 10161312 | 10127064 | 2860 lm |
| CANILO  3P 01 LED3000-BVC FL  ET 01 | 31 VA | Flood | - | without | CANILO_LED_FL.ies | LED | B+V+C | LED | 3000 lm | RAL 9016 traffic white | Oktalite_Alu_RAL_9016 | Oktalite_Canilo_WH3100 | 31 VA | 10161312 | 10125196 | 2860 lm |
| CANILO  3P 01 LED3000-BVC MF-c ET 01 | 31 VA | Medium Flood | - | clear | CANILO_LED_MF.ies | LED | B+V+C | LED | 3000 lm | RAL 9016 traffic white | Oktalite_Alu_RAL_9016 | Oktalite_Canilo_WH3100 | 31 VA | 10161312 | 10127063 | 2860 lm |
| CANILO  3P 01 LED3000-BVC MF  ET 01 | 31 VA | Medium Flood | - | without | CANILO_LED_MF.ies | LED | B+V+C | LED | 3000 lm | RAL 9016 traffic white | Oktalite_Alu_RAL_9016 | Oktalite_Canilo_WH3100 | 31 VA | 10161312 | 10125193 | 2860 lm |
| CANILO  3P 01 LED3000-BVC SP-c ET 01 | 31 VA | Spot | - | clear | CANILO_LED_SP.ies | LED | B+V+C | LED | 3000 lm | RAL 9016 traffic white | Oktalite_Alu_RAL_9016 | Oktalite_Canilo_WH3100 | 31 VA | 10161312 | 10127062 | 2860 lm |
| CANILO  3P 01 LED3000-BVC SP  ET 01 | 31 VA | Spot | - | without | CANILO_LED_SP.ies | LED | B+V+C | LED | 3000 lm | RAL 9016 traffic white | Oktalite_Alu_RAL_9016 | Oktalite_Canilo_WH3100 | 31 VA | 10161312 | 10125190 | 2860 lm |
| CANILO  3P 05 LED4000-831 VFL-c ET 05 | 32 VA | Very Wide Flood | 85 | clear | CANILO_LED_VFL.ies | LED | 3100 K Efficient Colour | LED | 4000 lm | RAL 9005 jet black | Oktalite_Alu_RAL_9005 | Oktalite_Canilo_WH3100 | 32 VA | 10161696 | 10147536 | 3555 lm |
| CANILO  3P 05 LED4000-831 VFL  ET 05 | 32 VA | Very Wide Flood | 85 | without | CANILO_LED_VFL.ies | LED | 3100 K Efficient Colour | LED | 4000 lm | RAL 9005 jet black | Oktalite_Alu_RAL_9005 | Oktalite_Canilo_WH3100 | 32 VA | 10161696 | 10147502 | 3555 lm |
| CANILO  3P 05 LED4000-831 WFL-c ET 05 | 32 VA | Wide Flood | 85 | clear | CANILO_LED_WFL.ies | LED | 3100 K Efficient Colour | LED | 4000 lm | RAL 9005 jet black | Oktalite_Alu_RAL_9005 | Oktalite_Canilo_WH3100 | 32 VA | 10161696 | 10147535 | 3555 lm |
| CANILO  3P 05 LED4000-831 WFL  ET 05 | 32 VA | Wide Flood | 85 | without | CANILO_LED_WFL.ies | LED | 3100 K Efficient Colour | LED | 4000 lm | RAL 9005 jet black | Oktalite_Alu_RAL_9005 | Oktalite_Canilo_WH3100 | 32 VA | 10161696 | 10147501 | 3555 lm |
| CANILO  3P 05 LED4000-831 FL-c ET 05 | 32 VA | Flood | 85 | clear | CANILO_LED_FL.ies | LED | 3100 K Efficient Colour | LED | 4000 lm | RAL 9005 jet black | Oktalite_Alu_RAL_9005 | Oktalite_Canilo_WH3100 | 32 VA | 10161696 | 10127064 | 3555 lm |
| CANILO  3P 05 LED4000-831 FL  ET 05 | 32 VA | Flood | 85 | without | CANILO_LED_FL.ies | LED | 3100 K Efficient Colour | LED | 4000 lm | RAL 9005 jet black | Oktalite_Alu_RAL_9005 | Oktalite_Canilo_WH3100 | 32 VA | 10161696 | 10125196 | 3555 lm |
| CANILO  3P 05 LED4000-831 MF-c ET 05 | 32 VA | Medium Flood | 85 | clear | CANILO_LED_MF.ies | LED | 3100 K Efficient Colour | LED | 4000 lm | RAL 9005 jet black | Oktalite_Alu_RAL_9005 | Oktalite_Canilo_WH3100 | 32 VA | 10161696 | 10127063 | 3555 lm |
| CANILO  3P 05 LED4000-831 MF  ET 05 | 32 VA | Medium Flood | 85 | without | CANILO_LED_MF.ies | LED | 3100 K Efficient Colour | LED | 4000 lm | RAL 9005 jet black | Oktalite_Alu_RAL_9005 | Oktalite_Canilo_WH3100 | 32 VA | 10161696 | 10125193 | 3555 lm |
| CANILO  3P 05 LED4000-831 SP-c ET 05 | 32 VA | Spot | 85 | clear | CANILO_LED_SP.ies | LED | 3100 K Efficient Colour | LED | 4000 lm | RAL 9005 jet black | Oktalite_Alu_RAL_9005 | Oktalite_Canilo_WH3100 | 32 VA | 10161696 | 10127062 | 3555 lm |
| CANILO  3P 05 LED4000-831 SP  ET 05 | 32 VA | Spot | 85 | without | CANILO_LED_SP.ies | LED | 3100 K Efficient Colour | LED | 4000 lm | RAL 9005 jet black | Oktalite_Alu_RAL_9005 | Oktalite_Canilo_WH3100 | 32 VA | 10161696 | 10125190 | 3555 lm |
| CANILO  3P 05 LED4000-831 VFL-c ET 03 | 32 VA | Very Wide Flood | 85 | clear | CANILO_LED_VFL.ies | LED | 3100 K Efficient Colour | LED | 4000 lm | RAL 9006 white aluminium | Oktalite_Alu_RAL_9006 | Oktalite_Canilo_WH3100 | 32 VA | 10161695 | 10147536 | 3555 lm |
| CANILO  3P 05 LED4000-831 VFL  ET 03 | 32 VA | Very Wide Flood | 85 | without | CANILO_LED_VFL.ies | LED | 3100 K Efficient Colour | LED | 4000 lm | RAL 9006 white aluminium | Oktalite_Alu_RAL_9006 | Oktalite_Canilo_WH3100 | 32 VA | 10161695 | 10147502 | 3555 lm |
| CANILO  3P 05 LED4000-831 WFL-c ET 03 | 32 VA | Wide Flood | 85 | clear | CANILO_LED_WFL.ies | LED | 3100 K Efficient Colour | LED | 4000 lm | RAL 9006 white aluminium | Oktalite_Alu_RAL_9006 | Oktalite_Canilo_WH3100 | 32 VA | 10161695 | 10147535 | 3555 lm |
| CANILO  3P 05 LED4000-831 WFL  ET 03 | 32 VA | Wide Flood | 85 | without | CANILO_LED_WFL.ies | LED | 3100 K Efficient Colour | LED | 4000 lm | RAL 9006 white aluminium | Oktalite_Alu_RAL_9006 | Oktalite_Canilo_WH3100 | 32 VA | 10161695 | 10147501 | 3555 lm |
| CANILO  3P 05 LED4000-831 FL-c ET 03 | 32 VA | Flood | 85 | clear | CANILO_LED_FL.ies | LED | 3100 K Efficient Colour | LED | 4000 lm | RAL 9006 white aluminium | Oktalite_Alu_RAL_9006 | Oktalite_Canilo_WH3100 | 32 VA | 10161695 | 10127064 | 3555 lm |
| CANILO  3P 05 LED4000-831 FL  ET 03 | 32 VA | Flood | 85 | without | CANILO_LED_FL.ies | LED | 3100 K Efficient Colour | LED | 4000 lm | RAL 9006 white aluminium | Oktalite_Alu_RAL_9006 | Oktalite_Canilo_WH3100 | 32 VA | 10161695 | 10125196 | 3555 lm |
| CANILO  3P 05 LED4000-831 MF-c ET 03 | 32 VA | Medium Flood | 85 | clear | CANILO_LED_MF.ies | LED | 3100 K Efficient Colour | LED | 4000 lm | RAL 9006 white aluminium | Oktalite_Alu_RAL_9006 | Oktalite_Canilo_WH3100 | 32 VA | 10161695 | 10127063 | 3555 lm |
| CANILO  3P 05 LED4000-831 MF  ET 03 | 32 VA | Medium Flood | 85 | without | CANILO_LED_MF.ies | LED | 3100 K Efficient Colour | LED | 4000 lm | RAL 9006 white aluminium | Oktalite_Alu_RAL_9006 | Oktalite_Canilo_WH3100 | 32 VA | 10161695 | 10125193 | 3555 lm |
| CANILO  3P 05 LED4000-831 SP-c ET 03 | 32 VA | Spot | 85 | clear | CANILO_LED_SP.ies | LED | 3100 K Efficient Colour | LED | 4000 lm | RAL 9006 white aluminium | Oktalite_Alu_RAL_9006 | Oktalite_Canilo_WH3100 | 32 VA | 10161695 | 10127062 | 3555 lm |
| CANILO  3P 05 LED4000-831 SP  ET 03 | 32 VA | Spot | 85 | without | CANILO_LED_SP.ies | LED | 3100 K Efficient Colour | LED | 4000 lm | RAL 9006 white aluminium | Oktalite_Alu_RAL_9006 | Oktalite_Canilo_WH3100 | 32 VA | 10161695 | 10125190 | 3555 lm |
| CANILO  3P 01 LED4000-831 VFL-c ET 01 | 32 VA | Very Wide Flood | 85 | clear | CANILO_LED_VFL.ies | LED | 3100 K Efficient Colour | LED | 4000 lm | RAL 9016 traffic white | Oktalite_Alu_RAL_9016 | Oktalite_Canilo_WH3100 | 32 VA | 10161694 | 10147536 | 3555 lm |
| CANILO  3P 01 LED4000-831 VFL  ET 01 | 32 VA | Very Wide Flood | 85 | without | CANILO_LED_VFL.ies | LED | 3100 K Efficient Colour | LED | 4000 lm | RAL 9016 traffic white | Oktalite_Alu_RAL_9016 | Oktalite_Canilo_WH3100 | 32 VA | 10161694 | 10147502 | 3555 lm |
| CANILO  3P 01 LED4000-831 WFL-c ET 01 | 32 VA | Wide Flood | 85 | clear | CANILO_LED_WFL.ies | LED | 3100 K Efficient Colour | LED | 4000 lm | RAL 9016 traffic white | Oktalite_Alu_RAL_9016 | Oktalite_Canilo_WH3100 | 32 VA | 10161694 | 10147535 | 3555 lm |
| CANILO  3P 01 LED4000-831 WFL  ET 01 | 32 VA | Wide Flood | 85 | without | CANILO_LED_WFL.ies | LED | 3100 K Efficient Colour | LED | 4000 lm | RAL 9016 traffic white | Oktalite_Alu_RAL_9016 | Oktalite_Canilo_WH3100 | 32 VA | 10161694 | 10147501 | 3555 lm |
| CANILO  3P 01 LED4000-831 FL-c ET 01 | 32 VA | Flood | 85 | clear | CANILO_LED_FL.ies | LED | 3100 K Efficient Colour | LED | 4000 lm | RAL 9016 traffic white | Oktalite_Alu_RAL_9016 | Oktalite_Canilo_WH3100 | 32 VA | 10161694 | 10127064 | 3555 lm |
| CANILO  3P 01 LED4000-831 FL  ET 01 | 32 VA | Flood | 85 | without | CANILO_LED_FL.ies | LED | 3100 K Efficient Colour | LED | 4000 lm | RAL 9016 traffic white | Oktalite_Alu_RAL_9016 | Oktalite_Canilo_WH3100 | 32 VA | 10161694 | 10125196 | 3555 lm |
| CANILO  3P 01 LED4000-831 MF-c ET 01 | 32 VA | Medium Flood | 85 | clear | CANILO_LED_MF.ies | LED | 3100 K Efficient Colour | LED | 4000 lm | RAL 9016 traffic white | Oktalite_Alu_RAL_9016 | Oktalite_Canilo_WH3100 | 32 VA | 10161694 | 10127063 | 3555 lm |
| CANILO  3P 01 LED4000-831 MF  ET 01 | 32 VA | Medium Flood | 85 | without | CANILO_LED_MF.ies | LED | 3100 K Efficient Colour | LED | 4000 lm | RAL 9016 traffic white | Oktalite_Alu_RAL_9016 | Oktalite_Canilo_WH3100 | 32 VA | 10161694 | 10125193 | 3555 lm |
| CANILO  3P 01 LED4000-831 SP-c ET 01 | 32 VA | Spot | 85 | clear | CANILO_LED_SP.ies | LED | 3100 K Efficient Colour | LED | 4000 lm | RAL 9016 traffic white | Oktalite_Alu_RAL_9016 | Oktalite_Canilo_WH3100 | 32 VA | 10161694 | 10127062 | 3555 lm |
| CANILO  3P 01 LED4000-831 SP  ET 01 | 32 VA | Spot | 85 | without | CANILO_LED_SP.ies | LED | 3100 K Efficient Colour | LED | 4000 lm | RAL 9016 traffic white | Oktalite_Alu_RAL_9016 | Oktalite_Canilo_WH3100 | 32 VA | 10161694 | 10125190 | 3555 lm |
| CANILO  3P 05 LED4000-931 VFL-c ET 05 | 42 VA | Very Wide Flood | 95 | clear | CANILO_LED_VFL.ies | LED | 3100 K Best Colour | LED | 4000 lm | RAL 9005 jet black | Oktalite_Alu_RAL_9005 | Oktalite_Canilo_WH3100 | 42 VA | 10161678 | 10147536 | 3510 lm |
| CANILO  3P 05 LED4000-931 VFL  ET 05 | 42 VA | Very Wide Flood | 95 | without | CANILO_LED_VFL.ies | LED | 3100 K Best Colour | LED | 4000 lm | RAL 9005 jet black | Oktalite_Alu_RAL_9005 | Oktalite_Canilo_WH3100 | 42 VA | 10161678 | 10147502 | 3510 lm |
| CANILO  3P 05 LED4000-931 WFL-c ET 05 | 42 VA | Wide Flood | 95 | clear | CANILO_LED_WFL.ies | LED | 3100 K Best Colour | LED | 4000 lm | RAL 9005 jet black | Oktalite_Alu_RAL_9005 | Oktalite_Canilo_WH3100 | 42 VA | 10161678 | 10147535 | 3510 lm |
| CANILO  3P 05 LED4000-931 WFL  ET 05 | 42 VA | Wide Flood | 95 | without | CANILO_LED_WFL.ies | LED | 3100 K Best Colour | LED | 4000 lm | RAL 9005 jet black | Oktalite_Alu_RAL_9005 | Oktalite_Canilo_WH3100 | 42 VA | 10161678 | 10147501 | 3510 lm |
| CANILO  3P 05 LED4000-931 FL-c ET 05 | 42 VA | Flood | 95 | clear | CANILO_LED_FL.ies | LED | 3100 K Best Colour | LED | 4000 lm | RAL 9005 jet black | Oktalite_Alu_RAL_9005 | Oktalite_Canilo_WH3100 | 42 VA | 10161678 | 10127064 | 3510 lm |
| CANILO  3P 05 LED4000-931 FL  ET 05 | 42 VA | Flood | 95 | without | CANILO_LED_FL.ies | LED | 3100 K Best Colour | LED | 4000 lm | RAL 9005 jet black | Oktalite_Alu_RAL_9005 | Oktalite_Canilo_WH3100 | 42 VA | 10161678 | 10125196 | 3510 lm |
| CANILO  3P 05 LED4000-931 MF-c ET 05 | 42 VA | Medium Flood | 95 | clear | CANILO_LED_MF.ies | LED | 3100 K Best Colour | LED | 4000 lm | RAL 9005 jet black | Oktalite_Alu_RAL_9005 | Oktalite_Canilo_WH3100 | 42 VA | 10161678 | 10127063 | 3510 lm |
| CANILO  3P 05 LED4000-931 MF  ET 05 | 42 VA | Medium Flood | 95 | without | CANILO_LED_MF.ies | LED | 3100 K Best Colour | LED | 4000 lm | RAL 9005 jet black | Oktalite_Alu_RAL_9005 | Oktalite_Canilo_WH3100 | 42 VA | 10161678 | 10125193 | 3510 lm |
| CANILO  3P 05 LED4000-931 SP-c ET 05 | 42 VA | Spot | 95 | clear | CANILO_LED_SP.ies | LED | 3100 K Best Colour | LED | 4000 lm | RAL 9005 jet black | Oktalite_Alu_RAL_9005 | Oktalite_Canilo_WH3100 | 42 VA | 10161678 | 10127062 | 3510 lm |
| CANILO  3P 05 LED4000-931 SP  ET 05 | 42 VA | Spot | 95 | without | CANILO_LED_SP.ies | LED | 3100 K Best Colour | LED | 4000 lm | RAL 9005 jet black | Oktalite_Alu_RAL_9005 | Oktalite_Canilo_WH3100 | 42 VA | 10161678 | 10125190 | 3510 lm |
| CANILO  3P 05 LED4000-931 VFL-c ET 03 | 42 VA | Very Wide Flood | 95 | clear | CANILO_LED_VFL.ies | LED | 3100 K Best Colour | LED | 4000 lm | RAL 9006 white aluminium | Oktalite_Alu_RAL_9006 | Oktalite_Canilo_WH3100 | 42 VA | 10161677 | 10147536 | 3510 lm |
| CANILO  3P 05 LED4000-931 VFL  ET 03 | 42 VA | Very Wide Flood | 95 | without | CANILO_LED_VFL.ies | LED | 3100 K Best Colour | LED | 4000 lm | RAL 9006 white aluminium | Oktalite_Alu_RAL_9006 | Oktalite_Canilo_WH3100 | 42 VA | 10161677 | 10147502 | 3510 lm |
| CANILO  3P 05 LED4000-931 WFL-c ET 03 | 42 VA | Wide Flood | 95 | clear | CANILO_LED_WFL.ies | LED | 3100 K Best Colour | LED | 4000 lm | RAL 9006 white aluminium | Oktalite_Alu_RAL_9006 | Oktalite_Canilo_WH3100 | 42 VA | 10161677 | 10147535 | 3510 lm |
| CANILO  3P 05 LED4000-931 WFL  ET 03 | 42 VA | Wide Flood | 95 | without | CANILO_LED_WFL.ies | LED | 3100 K Best Colour | LED | 4000 lm | RAL 9006 white aluminium | Oktalite_Alu_RAL_9006 | Oktalite_Canilo_WH3100 | 42 VA | 10161677 | 10147501 | 3510 lm |
| CANILO  3P 05 LED4000-931 FL-c ET 03 | 42 VA | Flood | 95 | clear | CANILO_LED_FL.ies | LED | 3100 K Best Colour | LED | 4000 lm | RAL 9006 white aluminium | Oktalite_Alu_RAL_9006 | Oktalite_Canilo_WH3100 | 42 VA | 10161677 | 10127064 | 3510 lm |
| CANILO  3P 05 LED4000-931 FL  ET 03 | 42 VA | Flood | 95 | without | CANILO_LED_FL.ies | LED | 3100 K Best Colour | LED | 4000 lm | RAL 9006 white aluminium | Oktalite_Alu_RAL_9006 | Oktalite_Canilo_WH3100 | 42 VA | 10161677 | 10125196 | 3510 lm |
| CANILO  3P 05 LED4000-931 MF-c ET 03 | 42 VA | Medium Flood | 95 | clear | CANILO_LED_MF.ies | LED | 3100 K Best Colour | LED | 4000 lm | RAL 9006 white aluminium | Oktalite_Alu_RAL_9006 | Oktalite_Canilo_WH3100 | 42 VA | 10161677 | 10127063 | 3510 lm |
| CANILO  3P 05 LED4000-931 MF  ET 03 | 42 VA | Medium Flood | 95 | without | CANILO_LED_MF.ies | LED | 3100 K Best Colour | LED | 4000 lm | RAL 9006 white aluminium | Oktalite_Alu_RAL_9006 | Oktalite_Canilo_WH3100 | 42 VA | 10161677 | 10125193 | 3510 lm |
| CANILO  3P 05 LED4000-931 SP-c ET 03 | 42 VA | Spot | 95 | clear | CANILO_LED_SP.ies | LED | 3100 K Best Colour | LED | 4000 lm | RAL 9006 white aluminium | Oktalite_Alu_RAL_9006 | Oktalite_Canilo_WH3100 | 42 VA | 10161677 | 10127062 | 3510 lm |
| CANILO  3P 05 LED4000-931 SP  ET 03 | 42 VA | Spot | 95 | without | CANILO_LED_SP.ies | LED | 3100 K Best Colour | LED | 4000 lm | RAL 9006 white aluminium | Oktalite_Alu_RAL_9006 | Oktalite_Canilo_WH3100 | 42 VA | 10161677 | 10125190 | 3510 lm |
| CANILO  3P 01 LED4000-931 VFL-c ET 01 | 42 VA | Very Wide Flood | 95 | clear | CANILO_LED_VFL.ies | LED | 3100 K Best Colour | LED | 4000 lm | RAL 9016 traffic white | Oktalite_Alu_RAL_9016 | Oktalite_Canilo_WH3100 | 42 VA | 10161676 | 10147536 | 3510 lm |
| CANILO  3P 01 LED4000-931 VFL  ET 01 | 42 VA | Very Wide Flood | 95 | without | CANILO_LED_VFL.ies | LED | 3100 K Best Colour | LED | 4000 lm | RAL 9016 traffic white | Oktalite_Alu_RAL_9016 | Oktalite_Canilo_WH3100 | 42 VA | 10161676 | 10147502 | 3510 lm |
| CANILO  3P 01 LED4000-931 WFL-c ET 01 | 42 VA | Wide Flood | 95 | clear | CANILO_LED_WFL.ies | LED | 3100 K Best Colour | LED | 4000 lm | RAL 9016 traffic white | Oktalite_Alu_RAL_9016 | Oktalite_Canilo_WH3100 | 42 VA | 10161676 | 10147535 | 3510 lm |
| CANILO  3P 01 LED4000-931 WFL  ET 01 | 42 VA | Wide Flood | 95 | without | CANILO_LED_WFL.ies | LED | 3100 K Best Colour | LED | 4000 lm | RAL 9016 traffic white | Oktalite_Alu_RAL_9016 | Oktalite_Canilo_WH3100 | 42 VA | 10161676 | 10147501 | 3510 lm |
| CANILO  3P 01 LED4000-931 FL-c ET 01 | 42 VA | Flood | 95 | clear | CANILO_LED_FL.ies | LED | 3100 K Best Colour | LED | 4000 lm | RAL 9016 traffic white | Oktalite_Alu_RAL_9016 | Oktalite_Canilo_WH3100 | 42 VA | 10161676 | 10127064 | 3510 lm |
| CANILO  3P 01 LED4000-931 FL  ET 01 | 42 VA | Flood | 95 | without | CANILO_LED_FL.ies | LED | 3100 K Best Colour | LED | 4000 lm | RAL 9016 traffic white | Oktalite_Alu_RAL_9016 | Oktalite_Canilo_WH3100 | 42 VA | 10161676 | 10125196 | 3510 lm |
| CANILO  3P 01 LED4000-931 MF-c ET 01 | 42 VA | Medium Flood | 95 | clear | CANILO_LED_MF.ies | LED | 3100 K Best Colour | LED | 4000 lm | RAL 9016 traffic white | Oktalite_Alu_RAL_9016 | Oktalite_Canilo_WH3100 | 42 VA | 10161676 | 10127063 | 3510 lm |
| CANILO  3P 01 LED4000-931 MF  ET 01 | 42 VA | Medium Flood | 95 | without | CANILO_LED_MF.ies | LED | 3100 K Best Colour | LED | 4000 lm | RAL 9016 traffic white | Oktalite_Alu_RAL_9016 | Oktalite_Canilo_WH3100 | 42 VA | 10161676 | 10125193 | 3510 lm |
| CANILO  3P 01 LED4000-931 SP-c ET 01 | 42 VA | Spot | 95 | clear | CANILO_LED_SP.ies | LED | 3100 K Best Colour | LED | 4000 lm | RAL 9016 traffic white | Oktalite_Alu_RAL_9016 | Oktalite_Canilo_WH3100 | 42 VA | 10161676 | 10127062 | 3510 lm |
| CANILO  3P 01 LED4000-931 SP  ET 01 | 42 VA | Spot | 95 | without | CANILO_LED_SP.ies | LED | 3100 K Best Colour | LED | 4000 lm | RAL 9016 traffic white | Oktalite_Alu_RAL_9016 | Oktalite_Canilo_WH3100 | 42 VA | 10161676 | 10125190 | 3510 lm |
| CANILO  3P 05 LED4000-840 VFL-c ET 05 | 32 VA | Very Wide Flood | 85 | clear | CANILO_LED_VFL.ies | LED | 4000 K | LED | 4000 lm | RAL 9005 jet black | Oktalite_Alu_RAL_9005 | Oktalite_Canilo_WH4000 | 32 VA | 10161708 | 10147536 | 3780 lm |
| CANILO  3P 05 LED4000-840 VFL  ET 05 | 32 VA | Very Wide Flood | 85 | without | CANILO_LED_VFL.ies | LED | 4000 K | LED | 4000 lm | RAL 9005 jet black | Oktalite_Alu_RAL_9005 | Oktalite_Canilo_WH4000 | 32 VA | 10161708 | 10147502 | 3780 lm |
| CANILO  3P 05 LED4000-840 WFL-c ET 05 | 32 VA | Wide Flood | 85 | clear | CANILO_LED_WFL.ies | LED | 4000 K | LED | 4000 lm | RAL 9005 jet black | Oktalite_Alu_RAL_9005 | Oktalite_Canilo_WH4000 | 32 VA | 10161708 | 10147535 | 3780 lm |
| CANILO  3P 05 LED4000-840 WFL  ET 05 | 32 VA | Wide Flood | 85 | without | CANILO_LED_WFL.ies | LED | 4000 K | LED | 4000 lm | RAL 9005 jet black | Oktalite_Alu_RAL_9005 | Oktalite_Canilo_WH4000 | 32 VA | 10161708 | 10147501 | 3780 lm |
| CANILO  3P 05 LED4000-840 FL-c ET 05 | 32 VA | Flood | 85 | clear | CANILO_LED_FL.ies | LED | 4000 K | LED | 4000 lm | RAL 9005 jet black | Oktalite_Alu_RAL_9005 | Oktalite_Canilo_WH4000 | 32 VA | 10161708 | 10127064 | 3780 lm |
| CANILO  3P 05 LED4000-840 FL  ET 05 | 32 VA | Flood | 85 | without | CANILO_LED_FL.ies | LED | 4000 K | LED | 4000 lm | RAL 9005 jet black | Oktalite_Alu_RAL_9005 | Oktalite_Canilo_WH4000 | 32 VA | 10161708 | 10125196 | 3780 lm |
| CANILO  3P 05 LED4000-840 MF-c ET 05 | 32 VA | Medium Flood | 85 | clear | CANILO_LED_MF.ies | LED | 4000 K | LED | 4000 lm | RAL 9005 jet black | Oktalite_Alu_RAL_9005 | Oktalite_Canilo_WH4000 | 32 VA | 10161708 | 10127063 | 3780 lm |
| CANILO  3P 05 LED4000-840 MF  ET 05 | 32 VA | Medium Flood | 85 | without | CANILO_LED_MF.ies | LED | 4000 K | LED | 4000 lm | RAL 9005 jet black | Oktalite_Alu_RAL_9005 | Oktalite_Canilo_WH4000 | 32 VA | 10161708 | 10125193 | 3780 lm |
| CANILO  3P 05 LED4000-840 SP-c ET 05 | 32 VA | Spot | 85 | clear | CANILO_LED_SP.ies | LED | 4000 K | LED | 4000 lm | RAL 9005 jet black | Oktalite_Alu_RAL_9005 | Oktalite_Canilo_WH4000 | 32 VA | 10161708 | 10127062 | 3780 lm |
| CANILO  3P 05 LED4000-840 SP  ET 05 | 32 VA | Spot | 85 | without | CANILO_LED_SP.ies | LED | 4000 K | LED | 4000 lm | RAL 9005 jet black | Oktalite_Alu_RAL_9005 | Oktalite_Canilo_WH4000 | 32 VA | 10161708 | 10125190 | 3780 lm |
| CANILO  3P 05 LED4000-840 VFL-c ET 03 | 32 VA | Very Wide Flood | 85 | clear | CANILO_LED_VFL.ies | LED | 4000 K | LED | 4000 lm | RAL 9006 white aluminium | Oktalite_Alu_RAL_9006 | Oktalite_Canilo_WH4000 | 32 VA | 10161707 | 10147536 | 3780 lm |
| CANILO  3P 05 LED4000-840 VFL  ET 03 | 32 VA | Very Wide Flood | 85 | without | CANILO_LED_VFL.ies | LED | 4000 K | LED | 4000 lm | RAL 9006 white aluminium | Oktalite_Alu_RAL_9006 | Oktalite_Canilo_WH4000 | 32 VA | 10161707 | 10147502 | 3780 lm |
| CANILO  3P 05 LED4000-840 WFL-c ET 03 | 32 VA | Wide Flood | 85 | clear | CANILO_LED_WFL.ies | LED | 4000 K | LED | 4000 lm | RAL 9006 white aluminium | Oktalite_Alu_RAL_9006 | Oktalite_Canilo_WH4000 | 32 VA | 10161707 | 10147535 | 3780 lm |
| CANILO  3P 05 LED4000-840 WFL  ET 03 | 32 VA | Wide Flood | 85 | without | CANILO_LED_WFL.ies | LED | 4000 K | LED | 4000 lm | RAL 9006 white aluminium | Oktalite_Alu_RAL_9006 | Oktalite_Canilo_WH4000 | 32 VA | 10161707 | 10147501 | 3780 lm |
| CANILO  3P 05 LED4000-840 FL-c ET 03 | 32 VA | Flood | 85 | clear | CANILO_LED_FL.ies | LED | 4000 K | LED | 4000 lm | RAL 9006 white aluminium | Oktalite_Alu_RAL_9006 | Oktalite_Canilo_WH4000 | 32 VA | 10161707 | 10127064 | 3780 lm |
| CANILO  3P 05 LED4000-840 FL  ET 03 | 32 VA | Flood | 85 | without | CANILO_LED_FL.ies | LED | 4000 K | LED | 4000 lm | RAL 9006 white aluminium | Oktalite_Alu_RAL_9006 | Oktalite_Canilo_WH4000 | 32 VA | 10161707 | 10125196 | 3780 lm |
| CANILO  3P 05 LED4000-840 MF-c ET 03 | 32 VA | Medium Flood | 85 | clear | CANILO_LED_MF.ies | LED | 4000 K | LED | 4000 lm | RAL 9006 white aluminium | Oktalite_Alu_RAL_9006 | Oktalite_Canilo_WH4000 | 32 VA | 10161707 | 10127063 | 3780 lm |
| CANILO  3P 05 LED4000-840 MF  ET 03 | 32 VA | Medium Flood | 85 | without | CANILO_LED_MF.ies | LED | 4000 K | LED | 4000 lm | RAL 9006 white aluminium | Oktalite_Alu_RAL_9006 | Oktalite_Canilo_WH4000 | 32 VA | 10161707 | 10125193 | 3780 lm |
| CANILO  3P 05 LED4000-840 SP-c ET 03 | 32 VA | Spot | 85 | clear | CANILO_LED_SP.ies | LED | 4000 K | LED | 4000 lm | RAL 9006 white aluminium | Oktalite_Alu_RAL_9006 | Oktalite_Canilo_WH4000 | 32 VA | 10161707 | 10127062 | 3780 lm |
| CANILO  3P 05 LED4000-840 SP  ET 03 | 32 VA | Spot | 85 | without | CANILO_LED_SP.ies | LED | 4000 K | LED | 4000 lm | RAL 9006 white aluminium | Oktalite_Alu_RAL_9006 | Oktalite_Canilo_WH4000 | 32 VA | 10161707 | 10125190 | 3780 lm |
| CANILO  3P 01 LED4000-840 VFL-c ET 01 | 32 VA | Very Wide Flood | 85 | clear | CANILO_LED_VFL.ies | LED | 4000 K | LED | 4000 lm | RAL 9016 traffic white | Oktalite_Alu_RAL_9016 | Oktalite_Canilo_WH4000 | 32 VA | 10161706 | 10147536 | 3780 lm |
| CANILO  3P 01 LED4000-840 VFL  ET 01 | 32 VA | Very Wide Flood | 85 | without | CANILO_LED_VFL.ies | LED | 4000 K | LED | 4000 lm | RAL 9016 traffic white | Oktalite_Alu_RAL_9016 | Oktalite_Canilo_WH4000 | 32 VA | 10161706 | 10147502 | 3780 lm |
| CANILO  3P 01 LED4000-840 WFL-c ET 01 | 32 VA | Wide Flood | 85 | clear | CANILO_LED_WFL.ies | LED | 4000 K | LED | 4000 lm | RAL 9016 traffic white | Oktalite_Alu_RAL_9016 | Oktalite_Canilo_WH4000 | 32 VA | 10161706 | 10147535 | 3780 lm |
| CANILO  3P 01 LED4000-840 WFL  ET 01 | 32 VA | Wide Flood | 85 | without | CANILO_LED_WFL.ies | LED | 4000 K | LED | 4000 lm | RAL 9016 traffic white | Oktalite_Alu_RAL_9016 | Oktalite_Canilo_WH4000 | 32 VA | 10161706 | 10147501 | 3780 lm |
| CANILO  3P 01 LED4000-840 FL-c ET 01 | 32 VA | Flood | 85 | clear | CANILO_LED_FL.ies | LED | 4000 K | LED | 4000 lm | RAL 9016 traffic white | Oktalite_Alu_RAL_9016 | Oktalite_Canilo_WH4000 | 32 VA | 10161706 | 10127064 | 3780 lm |
| CANILO  3P 01 LED4000-840 FL  ET 01 | 32 VA | Flood | 85 | without | CANILO_LED_FL.ies | LED | 4000 K | LED | 4000 lm | RAL 9016 traffic white | Oktalite_Alu_RAL_9016 | Oktalite_Canilo_WH4000 | 32 VA | 10161706 | 10125196 | 3780 lm |
| CANILO  3P 01 LED4000-840 MF-c ET 01 | 32 VA | Medium Flood | 85 | clear | CANILO_LED_MF.ies | LED | 4000 K | LED | 4000 lm | RAL 9016 traffic white | Oktalite_Alu_RAL_9016 | Oktalite_Canilo_WH4000 | 32 VA | 10161706 | 10127063 | 3780 lm |
| CANILO  3P 01 LED4000-840 MF  ET 01 | 32 VA | Medium Flood | 85 | without | CANILO_LED_MF.ies | LED | 4000 K | LED | 4000 lm | RAL 9016 traffic white | Oktalite_Alu_RAL_9016 | Oktalite_Canilo_WH4000 | 32 VA | 10161706 | 10125193 | 3780 lm |
| CANILO  3P 01 LED4000-840 SP-c ET 01 | 32 VA | Spot | 85 | clear | CANILO_LED_SP.ies | LED | 4000 K | LED | 4000 lm | RAL 9016 traffic white | Oktalite_Alu_RAL_9016 | Oktalite_Canilo_WH4000 | 32 VA | 10161706 | 10127062 | 3780 lm |
| CANILO  3P 01 LED4000-840 SP  ET 01 | 32 VA | Spot | 85 | without | CANILO_LED_SP.ies | LED | 4000 K | LED | 4000 lm | RAL 9016 traffic white | Oktalite_Alu_RAL_9016 | Oktalite_Canilo_WH4000 | 32 VA | 10161706 | 10125190 | 3780 lm |
| CANILO  3P 05 LED4000-835 VFL-c ET 05 | 32 VA | Very Wide Flood | 85 | clear | CANILO_LED_VFL.ies | LED | 3500 K | LED | 4000 lm | RAL 9005 jet black | Oktalite_Alu_RAL_9005 | Oktalite_Canilo_WH3500 | 32 VA | 10161702 | 10147536 | 3700 lm |
| CANILO  3P 05 LED4000-835 VFL  ET 05 | 32 VA | Very Wide Flood | 85 | without | CANILO_LED_VFL.ies | LED | 3500 K | LED | 4000 lm | RAL 9005 jet black | Oktalite_Alu_RAL_9005 | Oktalite_Canilo_WH3500 | 32 VA | 10161702 | 10147502 | 3700 lm |
| CANILO  3P 05 LED4000-835 WFL-c ET 05 | 32 VA | Wide Flood | 85 | clear | CANILO_LED_WFL.ies | LED | 3500 K | LED | 4000 lm | RAL 9005 jet black | Oktalite_Alu_RAL_9005 | Oktalite_Canilo_WH3500 | 32 VA | 10161702 | 10147535 | 3700 lm |
| CANILO  3P 05 LED4000-835 WFL  ET 05 | 32 VA | Wide Flood | 85 | without | CANILO_LED_WFL.ies | LED | 3500 K | LED | 4000 lm | RAL 9005 jet black | Oktalite_Alu_RAL_9005 | Oktalite_Canilo_WH3500 | 32 VA | 10161702 | 10147501 | 3700 lm |
| CANILO  3P 05 LED4000-835 FL-c ET 05 | 32 VA | Flood | 85 | clear | CANILO_LED_FL.ies | LED | 3500 K | LED | 4000 lm | RAL 9005 jet black | Oktalite_Alu_RAL_9005 | Oktalite_Canilo_WH3500 | 32 VA | 10161702 | 10127064 | 3700 lm |
| CANILO  3P 05 LED4000-835 FL  ET 05 | 32 VA | Flood | 85 | without | CANILO_LED_FL.ies | LED | 3500 K | LED | 4000 lm | RAL 9005 jet black | Oktalite_Alu_RAL_9005 | Oktalite_Canilo_WH3500 | 32 VA | 10161702 | 10125196 | 3700 lm |
| CANILO  3P 05 LED4000-835 MF-c ET 05 | 32 VA | Medium Flood | 85 | clear | CANILO_LED_MF.ies | LED | 3500 K | LED | 4000 lm | RAL 9005 jet black | Oktalite_Alu_RAL_9005 | Oktalite_Canilo_WH3500 | 32 VA | 10161702 | 10127063 | 3700 lm |
| CANILO  3P 05 LED4000-835 MF  ET 05 | 32 VA | Medium Flood | 85 | without | CANILO_LED_MF.ies | LED | 3500 K | LED | 4000 lm | RAL 9005 jet black | Oktalite_Alu_RAL_9005 | Oktalite_Canilo_WH3500 | 32 VA | 10161702 | 10125193 | 3700 lm |
| CANILO  3P 05 LED4000-835 SP-c ET 05 | 32 VA | Spot | 85 | clear | CANILO_LED_SP.ies | LED | 3500 K | LED | 4000 lm | RAL 9005 jet black | Oktalite_Alu_RAL_9005 | Oktalite_Canilo_WH3500 | 32 VA | 10161702 | 10127062 | 3700 lm |
| CANILO  3P 05 LED4000-835 SP  ET 05 | 32 VA | Spot | 85 | without | CANILO_LED_SP.ies | LED | 3500 K | LED | 4000 lm | RAL 9005 jet black | Oktalite_Alu_RAL_9005 | Oktalite_Canilo_WH3500 | 32 VA | 10161702 | 10125190 | 3700 lm |
| CANILO  3P 05 LED4000-835 VFL-c ET 03 | 32 VA | Very Wide Flood | 85 | clear | CANILO_LED_VFL.ies | LED | 3500 K | LED | 4000 lm | RAL 9006 white aluminium | Oktalite_Alu_RAL_9006 | Oktalite_Canilo_WH3500 | 32 VA | 10161701 | 10147536 | 3700 lm |
| CANILO  3P 05 LED4000-835 VFL  ET 03 | 32 VA | Very Wide Flood | 85 | without | CANILO_LED_VFL.ies | LED | 3500 K | LED | 4000 lm | RAL 9006 white aluminium | Oktalite_Alu_RAL_9006 | Oktalite_Canilo_WH3500 | 32 VA | 10161701 | 10147502 | 3700 lm |
| CANILO  3P 05 LED4000-835 WFL-c ET 03 | 32 VA | Wide Flood | 85 | clear | CANILO_LED_WFL.ies | LED | 3500 K | LED | 4000 lm | RAL 9006 white aluminium | Oktalite_Alu_RAL_9006 | Oktalite_Canilo_WH3500 | 32 VA | 10161701 | 10147535 | 3700 lm |
| CANILO  3P 05 LED4000-835 WFL  ET 03 | 32 VA | Wide Flood | 85 | without | CANILO_LED_WFL.ies | LED | 3500 K | LED | 4000 lm | RAL 9006 white aluminium | Oktalite_Alu_RAL_9006 | Oktalite_Canilo_WH3500 | 32 VA | 10161701 | 10147501 | 3700 lm |
| CANILO  3P 05 LED4000-835 FL-c ET 03 | 32 VA | Flood | 85 | clear | CANILO_LED_FL.ies | LED | 3500 K | LED | 4000 lm | RAL 9006 white aluminium | Oktalite_Alu_RAL_9006 | Oktalite_Canilo_WH3500 | 32 VA | 10161701 | 10127064 | 3700 lm |
| CANILO  3P 05 LED4000-835 FL  ET 03 | 32 VA | Flood | 85 | without | CANILO_LED_FL.ies | LED | 3500 K | LED | 4000 lm | RAL 9006 white aluminium | Oktalite_Alu_RAL_9006 | Oktalite_Canilo_WH3500 | 32 VA | 10161701 | 10125196 | 3700 lm |
| CANILO  3P 05 LED4000-835 MF-c ET 03 | 32 VA | Medium Flood | 85 | clear | CANILO_LED_MF.ies | LED | 3500 K | LED | 4000 lm | RAL 9006 white aluminium | Oktalite_Alu_RAL_9006 | Oktalite_Canilo_WH3500 | 32 VA | 10161701 | 10127063 | 3700 lm |
| CANILO  3P 05 LED4000-835 MF  ET 03 | 32 VA | Medium Flood | 85 | without | CANILO_LED_MF.ies | LED | 3500 K | LED | 4000 lm | RAL 9006 white aluminium | Oktalite_Alu_RAL_9006 | Oktalite_Canilo_WH3500 | 32 VA | 10161701 | 10125193 | 3700 lm |
| CANILO  3P 05 LED4000-835 SP-c ET 03 | 32 VA | Spot | 85 | clear | CANILO_LED_SP.ies | LED | 3500 K | LED | 4000 lm | RAL 9006 white aluminium | Oktalite_Alu_RAL_9006 | Oktalite_Canilo_WH3500 | 32 VA | 10161701 | 10127062 | 3700 lm |
| CANILO  3P 05 LED4000-835 SP  ET 03 | 32 VA | Spot | 85 | without | CANILO_LED_SP.ies | LED | 3500 K | LED | 4000 lm | RAL 9006 white aluminium | Oktalite_Alu_RAL_9006 | Oktalite_Canilo_WH3500 | 32 VA | 10161701 | 10125190 | 3700 lm |
| CANILO  3P 01 LED4000-835 VFL-c ET 01 | 32 VA | Very Wide Flood | 85 | clear | CANILO_LED_VFL.ies | LED | 3500 K | LED | 4000 lm | RAL 9016 traffic white | Oktalite_Alu_RAL_9016 | Oktalite_Canilo_WH3500 | 32 VA | 10161700 | 10147536 | 3700 lm |
| CANILO  3P 01 LED4000-835 VFL  ET 01 | 32 VA | Very Wide Flood | 85 | without | CANILO_LED_VFL.ies | LED | 3500 K | LED | 4000 lm | RAL 9016 traffic white | Oktalite_Alu_RAL_9016 | Oktalite_Canilo_WH3500 | 32 VA | 10161700 | 10147502 | 3700 lm |
| CANILO  3P 01 LED4000-835 WFL-c ET 01 | 32 VA | Wide Flood | 85 | clear | CANILO_LED_WFL.ies | LED | 3500 K | LED | 4000 lm | RAL 9016 traffic white | Oktalite_Alu_RAL_9016 | Oktalite_Canilo_WH3500 | 32 VA | 10161700 | 10147535 | 3700 lm |
| CANILO  3P 01 LED4000-835 WFL  ET 01 | 32 VA | Wide Flood | 85 | without | CANILO_LED_WFL.ies | LED | 3500 K | LED | 4000 lm | RAL 9016 traffic white | Oktalite_Alu_RAL_9016 | Oktalite_Canilo_WH3500 | 32 VA | 10161700 | 10147501 | 3700 lm |
| CANILO  3P 01 LED4000-835 FL-c ET 01 | 32 VA | Flood | 85 | clear | CANILO_LED_FL.ies | LED | 3500 K | LED | 4000 lm | RAL 9016 traffic white | Oktalite_Alu_RAL_9016 | Oktalite_Canilo_WH3500 | 32 VA | 10161700 | 10127064 | 3700 lm |
| CANILO  3P 01 LED4000-835 FL  ET 01 | 32 VA | Flood | 85 | without | CANILO_LED_FL.ies | LED | 3500 K | LED | 4000 lm | RAL 9016 traffic white | Oktalite_Alu_RAL_9016 | Oktalite_Canilo_WH3500 | 32 VA | 10161700 | 10125196 | 3700 lm |
| CANILO  3P 01 LED4000-835 MF-c ET 01 | 32 VA | Medium Flood | 85 | clear | CANILO_LED_MF.ies | LED | 3500 K | LED | 4000 lm | RAL 9016 traffic white | Oktalite_Alu_RAL_9016 | Oktalite_Canilo_WH3500 | 32 VA | 10161700 | 10127063 | 3700 lm |
| CANILO  3P 01 LED4000-835 MF  ET 01 | 32 VA | Medium Flood | 85 | without | CANILO_LED_MF.ies | LED | 3500 K | LED | 4000 lm | RAL 9016 traffic white | Oktalite_Alu_RAL_9016 | Oktalite_Canilo_WH3500 | 32 VA | 10161700 | 10125193 | 3700 lm |
| CANILO  3P 01 LED4000-835 SP-c ET 01 | 32 VA | Spot | 85 | clear | CANILO_LED_SP.ies | LED | 3500 K | LED | 4000 lm | RAL 9016 traffic white | Oktalite_Alu_RAL_9016 | Oktalite_Canilo_WH3500 | 32 VA | 10161700 | 10127062 | 3700 lm |
| CANILO  3P 01 LED4000-835 SP  ET 01 | 32 VA | Spot | 85 | without | CANILO_LED_SP.ies | LED | 3500 K | LED | 4000 lm | RAL 9016 traffic white | Oktalite_Alu_RAL_9016 | Oktalite_Canilo_WH3500 | 32 VA | 10161700 | 10125190 | 3700 lm |
| CANILO  3P 05 LED4000-830 VFL-c ET 05 | 32 VA | Very Wide Flood | 85 | clear | CANILO_LED_VFL.ies | LED | 3000 K | LED | 4000 lm | RAL 9005 jet black | Oktalite_Alu_RAL_9005 | Oktalite_Canilo_WH3000 | 32 VA | 10161690 | 10147536 | 3655 lm |
| CANILO  3P 05 LED4000-830 VFL  ET 05 | 32 VA | Very Wide Flood | 85 | without | CANILO_LED_VFL.ies | LED | 3000 K | LED | 4000 lm | RAL 9005 jet black | Oktalite_Alu_RAL_9005 | Oktalite_Canilo_WH3000 | 32 VA | 10161690 | 10147502 | 3655 lm |
| CANILO  3P 05 LED4000-830 WFL-c ET 05 | 32 VA | Wide Flood | 85 | clear | CANILO_LED_WFL.ies | LED | 3000 K | LED | 4000 lm | RAL 9005 jet black | Oktalite_Alu_RAL_9005 | Oktalite_Canilo_WH3000 | 32 VA | 10161690 | 10147535 | 3655 lm |
| CANILO  3P 05 LED4000-830 WFL  ET 05 | 32 VA | Wide Flood | 85 | without | CANILO_LED_WFL.ies | LED | 3000 K | LED | 4000 lm | RAL 9005 jet black | Oktalite_Alu_RAL_9005 | Oktalite_Canilo_WH3000 | 32 VA | 10161690 | 10147501 | 3655 lm |
| CANILO  3P 05 LED4000-830 FL-c ET 05 | 32 VA | Flood | 85 | clear | CANILO_LED_FL.ies | LED | 3000 K | LED | 4000 lm | RAL 9005 jet black | Oktalite_Alu_RAL_9005 | Oktalite_Canilo_WH3000 | 32 VA | 10161690 | 10127064 | 3655 lm |
| CANILO  3P 05 LED4000-830 FL  ET 05 | 32 VA | Flood | 85 | without | CANILO_LED_FL.ies | LED | 3000 K | LED | 4000 lm | RAL 9005 jet black | Oktalite_Alu_RAL_9005 | Oktalite_Canilo_WH3000 | 32 VA | 10161690 | 10125196 | 3655 lm |
| CANILO  3P 05 LED4000-830 MF-c ET 05 | 32 VA | Medium Flood | 85 | clear | CANILO_LED_MF.ies | LED | 3000 K | LED | 4000 lm | RAL 9005 jet black | Oktalite_Alu_RAL_9005 | Oktalite_Canilo_WH3000 | 32 VA | 10161690 | 10127063 | 3655 lm |
| CANILO  3P 05 LED4000-830 MF  ET 05 | 32 VA | Medium Flood | 85 | without | CANILO_LED_MF.ies | LED | 3000 K | LED | 4000 lm | RAL 9005 jet black | Oktalite_Alu_RAL_9005 | Oktalite_Canilo_WH3000 | 32 VA | 10161690 | 10125193 | 3655 lm |
| CANILO  3P 05 LED4000-830 SP-c ET 05 | 32 VA | Spot | 85 | clear | CANILO_LED_SP.ies | LED | 3000 K | LED | 4000 lm | RAL 9005 jet black | Oktalite_Alu_RAL_9005 | Oktalite_Canilo_WH3000 | 32 VA | 10161690 | 10127062 | 3655 lm |
| CANILO  3P 05 LED4000-830 SP  ET 05 | 32 VA | Spot | 85 | without | CANILO_LED_SP.ies | LED | 3000 K | LED | 4000 lm | RAL 9005 jet black | Oktalite_Alu_RAL_9005 | Oktalite_Canilo_WH3000 | 32 VA | 10161690 | 10125190 | 3655 lm |
| CANILO  3P 05 LED4000-830 VFL-c ET 03 | 32 VA | Very Wide Flood | 85 | clear | CANILO_LED_VFL.ies | LED | 3000 K | LED | 4000 lm | RAL 9006 white aluminium | Oktalite_Alu_RAL_9006 | Oktalite_Canilo_WH3000 | 32 VA | 10161689 | 10147536 | 3655 lm |
| CANILO  3P 05 LED4000-830 VFL  ET 03 | 32 VA | Very Wide Flood | 85 | without | CANILO_LED_VFL.ies | LED | 3000 K | LED | 4000 lm | RAL 9006 white aluminium | Oktalite_Alu_RAL_9006 | Oktalite_Canilo_WH3000 | 32 VA | 10161689 | 10147502 | 3655 lm |
| CANILO  3P 05 LED4000-830 WFL-c ET 03 | 32 VA | Wide Flood | 85 | clear | CANILO_LED_WFL.ies | LED | 3000 K | LED | 4000 lm | RAL 9006 white aluminium | Oktalite_Alu_RAL_9006 | Oktalite_Canilo_WH3000 | 32 VA | 10161689 | 10147535 | 3655 lm |
| CANILO  3P 05 LED4000-830 WFL  ET 03 | 32 VA | Wide Flood | 85 | without | CANILO_LED_WFL.ies | LED | 3000 K | LED | 4000 lm | RAL 9006 white aluminium | Oktalite_Alu_RAL_9006 | Oktalite_Canilo_WH3000 | 32 VA | 10161689 | 10147501 | 3655 lm |
| CANILO  3P 05 LED4000-830 FL-c ET 03 | 32 VA | Flood | 85 | clear | CANILO_LED_FL.ies | LED | 3000 K | LED | 4000 lm | RAL 9006 white aluminium | Oktalite_Alu_RAL_9006 | Oktalite_Canilo_WH3000 | 32 VA | 10161689 | 10127064 | 3655 lm |
| CANILO  3P 05 LED4000-830 FL  ET 03 | 32 VA | Flood | 85 | without | CANILO_LED_FL.ies | LED | 3000 K | LED | 4000 lm | RAL 9006 white aluminium | Oktalite_Alu_RAL_9006 | Oktalite_Canilo_WH3000 | 32 VA | 10161689 | 10125196 | 3655 lm |
| CANILO  3P 05 LED4000-830 MF-c ET 03 | 32 VA | Medium Flood | 85 | clear | CANILO_LED_MF.ies | LED | 3000 K | LED | 4000 lm | RAL 9006 white aluminium | Oktalite_Alu_RAL_9006 | Oktalite_Canilo_WH3000 | 32 VA | 10161689 | 10127063 | 3655 lm |
| CANILO  3P 05 LED4000-830 MF  ET 03 | 32 VA | Medium Flood | 85 | without | CANILO_LED_MF.ies | LED | 3000 K | LED | 4000 lm | RAL 9006 white aluminium | Oktalite_Alu_RAL_9006 | Oktalite_Canilo_WH3000 | 32 VA | 10161689 | 10125193 | 3655 lm |
| CANILO  3P 05 LED4000-830 SP-c ET 03 | 32 VA | Spot | 85 | clear | CANILO_LED_SP.ies | LED | 3000 K | LED | 4000 lm | RAL 9006 white aluminium | Oktalite_Alu_RAL_9006 | Oktalite_Canilo_WH3000 | 32 VA | 10161689 | 10127062 | 3655 lm |
| CANILO  3P 05 LED4000-830 SP  ET 03 | 32 VA | Spot | 85 | without | CANILO_LED_SP.ies | LED | 3000 K | LED | 4000 lm | RAL 9006 white aluminium | Oktalite_Alu_RAL_9006 | Oktalite_Canilo_WH3000 | 32 VA | 10161689 | 10125190 | 3655 lm |
| CANILO  3P 01 LED4000-830 VFL-c ET 01 | 32 VA | Very Wide Flood | 85 | clear | CANILO_LED_VFL.ies | LED | 3000 K | LED | 4000 lm | RAL 9016 traffic white | Oktalite_Alu_RAL_9016 | Oktalite_Canilo_WH3000 | 32 VA | 10161688 | 10147536 | 3655 lm |
| CANILO  3P 01 LED4000-830 VFL  ET 01 | 32 VA | Very Wide Flood | 85 | without | CANILO_LED_VFL.ies | LED | 3000 K | LED | 4000 lm | RAL 9016 traffic white | Oktalite_Alu_RAL_9016 | Oktalite_Canilo_WH3000 | 32 VA | 10161688 | 10147502 | 3655 lm |
| CANILO  3P 01 LED4000-830 WFL-c ET 01 | 32 VA | Wide Flood | 85 | clear | CANILO_LED_WFL.ies | LED | 3000 K | LED | 4000 lm | RAL 9016 traffic white | Oktalite_Alu_RAL_9016 | Oktalite_Canilo_WH3000 | 32 VA | 10161688 | 10147535 | 3655 lm |
| CANILO  3P 01 LED4000-830 WFL  ET 01 | 32 VA | Wide Flood | 85 | without | CANILO_LED_WFL.ies | LED | 3000 K | LED | 4000 lm | RAL 9016 traffic white | Oktalite_Alu_RAL_9016 | Oktalite_Canilo_WH3000 | 32 VA | 10161688 | 10147501 | 3655 lm |
| CANILO  3P 01 LED4000-830 FL-c ET 01 | 32 VA | Flood | 85 | clear | CANILO_LED_FL.ies | LED | 3000 K | LED | 4000 lm | RAL 9016 traffic white | Oktalite_Alu_RAL_9016 | Oktalite_Canilo_WH3000 | 32 VA | 10161688 | 10127064 | 3655 lm |
| CANILO  3P 01 LED4000-830 FL  ET 01 | 32 VA | Flood | 85 | without | CANILO_LED_FL.ies | LED | 3000 K | LED | 4000 lm | RAL 9016 traffic white | Oktalite_Alu_RAL_9016 | Oktalite_Canilo_WH3000 | 32 VA | 10161688 | 10125196 | 3655 lm |
| CANILO  3P 01 LED4000-830 MF-c ET 01 | 32 VA | Medium Flood | 85 | clear | CANILO_LED_MF.ies | LED | 3000 K | LED | 4000 lm | RAL 9016 traffic white | Oktalite_Alu_RAL_9016 | Oktalite_Canilo_WH3000 | 32 VA | 10161688 | 10127063 | 3655 lm |
| CANILO  3P 01 LED4000-830 MF  ET 01 | 32 VA | Medium Flood | 85 | without | CANILO_LED_MF.ies | LED | 3000 K | LED | 4000 lm | RAL 9016 traffic white | Oktalite_Alu_RAL_9016 | Oktalite_Canilo_WH3000 | 32 VA | 10161688 | 10125193 | 3655 lm |
| CANILO  3P 01 LED4000-830 SP-c ET 01 | 32 VA | Spot | 85 | clear | CANILO_LED_SP.ies | LED | 3000 K | LED | 4000 lm | RAL 9016 traffic white | Oktalite_Alu_RAL_9016 | Oktalite_Canilo_WH3000 | 32 VA | 10161688 | 10127062 | 3655 lm |
| CANILO  3P 01 LED4000-830 SP  ET 01 | 32 VA | Spot | 85 | without | CANILO_LED_SP.ies | LED | 3000 K | LED | 4000 lm | RAL 9016 traffic white | Oktalite_Alu_RAL_9016 | Oktalite_Canilo_WH3000 | 32 VA | 10161688 | 10125190 | 3655 lm |
| CANILO  3P 05 LED4000-827 VFL-c ET 05 | 32 VA | Very Wide Flood | 82 | clear | CANILO_LED_VFL.ies | LED | 2700 K | LED | 4000 lm | RAL 9005 jet black | Oktalite_Alu_RAL_9005 | Oktalite_Canilo_WH2700 | 32 VA | 10161684 | 10147536 | 3395 lm |
| CANILO  3P 05 LED4000-827 VFL  ET 05 | 32 VA | Very Wide Flood | 82 | without | CANILO_LED_VFL.ies | LED | 2700 K | LED | 4000 lm | RAL 9005 jet black | Oktalite_Alu_RAL_9005 | Oktalite_Canilo_WH2700 | 32 VA | 10161684 | 10147502 | 3395 lm |
| CANILO  3P 05 LED4000-827 WFL-c ET 05 | 32 VA | Wide Flood | 82 | clear | CANILO_LED_WFL.ies | LED | 2700 K | LED | 4000 lm | RAL 9005 jet black | Oktalite_Alu_RAL_9005 | Oktalite_Canilo_WH2700 | 32 VA | 10161684 | 10147535 | 3395 lm |
| CANILO  3P 05 LED4000-827 WFL  ET 05 | 32 VA | Wide Flood | 82 | without | CANILO_LED_WFL.ies | LED | 2700 K | LED | 4000 lm | RAL 9005 jet black | Oktalite_Alu_RAL_9005 | Oktalite_Canilo_WH2700 | 32 VA | 10161684 | 10147501 | 3395 lm |
| CANILO  3P 05 LED4000-827 FL-c ET 05 | 32 VA | Flood | 82 | clear | CANILO_LED_FL.ies | LED | 2700 K | LED | 4000 lm | RAL 9005 jet black | Oktalite_Alu_RAL_9005 | Oktalite_Canilo_WH2700 | 32 VA | 10161684 | 10127064 | 3395 lm |
| CANILO  3P 05 LED4000-827 FL  ET 05 | 32 VA | Flood | 82 | without | CANILO_LED_FL.ies | LED | 2700 K | LED | 4000 lm | RAL 9005 jet black | Oktalite_Alu_RAL_9005 | Oktalite_Canilo_WH2700 | 32 VA | 10161684 | 10125196 | 3395 lm |
| CANILO  3P 05 LED4000-827 MF-c ET 05 | 32 VA | Medium Flood | 82 | clear | CANILO_LED_MF.ies | LED | 2700 K | LED | 4000 lm | RAL 9005 jet black | Oktalite_Alu_RAL_9005 | Oktalite_Canilo_WH2700 | 32 VA | 10161684 | 10127063 | 3395 lm |
| CANILO  3P 05 LED4000-827 MF  ET 05 | 32 VA | Medium Flood | 82 | without | CANILO_LED_MF.ies | LED | 2700 K | LED | 4000 lm | RAL 9005 jet black | Oktalite_Alu_RAL_9005 | Oktalite_Canilo_WH2700 | 32 VA | 10161684 | 10125193 | 3395 lm |
| CANILO  3P 05 LED4000-827 SP-c ET 05 | 32 VA | Spot | 82 | clear | CANILO_LED_SP.ies | LED | 2700 K | LED | 4000 lm | RAL 9005 jet black | Oktalite_Alu_RAL_9005 | Oktalite_Canilo_WH2700 | 32 VA | 10161684 | 10127062 | 3395 lm |
| CANILO  3P 05 LED4000-827 SP  ET 05 | 32 VA | Spot | 82 | without | CANILO_LED_SP.ies | LED | 2700 K | LED | 4000 lm | RAL 9005 jet black | Oktalite_Alu_RAL_9005 | Oktalite_Canilo_WH2700 | 32 VA | 10161684 | 10125190 | 3395 lm |
| CANILO  3P 05 LED4000-827 VFL-c ET 03 | 32 VA | Very Wide Flood | 82 | clear | CANILO_LED_VFL.ies | LED | 2700 K | LED | 4000 lm | RAL 9006 white aluminium | Oktalite_Alu_RAL_9006 | Oktalite_Canilo_WH2700 | 32 VA | 10161683 | 10147536 | 3395 lm |
| CANILO  3P 05 LED4000-827 VFL  ET 03 | 32 VA | Very Wide Flood | 82 | without | CANILO_LED_VFL.ies | LED | 2700 K | LED | 4000 lm | RAL 9006 white aluminium | Oktalite_Alu_RAL_9006 | Oktalite_Canilo_WH2700 | 32 VA | 10161683 | 10147502 | 3395 lm |
| CANILO  3P 05 LED4000-827 WFL-c ET 03 | 32 VA | Wide Flood | 82 | clear | CANILO_LED_WFL.ies | LED | 2700 K | LED | 4000 lm | RAL 9006 white aluminium | Oktalite_Alu_RAL_9006 | Oktalite_Canilo_WH2700 | 32 VA | 10161683 | 10147535 | 3395 lm |
| CANILO  3P 05 LED4000-827 WFL  ET 03 | 32 VA | Wide Flood | 82 | without | CANILO_LED_WFL.ies | LED | 2700 K | LED | 4000 lm | RAL 9006 white aluminium | Oktalite_Alu_RAL_9006 | Oktalite_Canilo_WH2700 | 32 VA | 10161683 | 10147501 | 3395 lm |
| CANILO  3P 05 LED4000-827 FL-c ET 03 | 32 VA | Flood | 82 | clear | CANILO_LED_FL.ies | LED | 2700 K | LED | 4000 lm | RAL 9006 white aluminium | Oktalite_Alu_RAL_9006 | Oktalite_Canilo_WH2700 | 32 VA | 10161683 | 10127064 | 3395 lm |
| CANILO  3P 05 LED4000-827 FL  ET 03 | 32 VA | Flood | 82 | without | CANILO_LED_FL.ies | LED | 2700 K | LED | 4000 lm | RAL 9006 white aluminium | Oktalite_Alu_RAL_9006 | Oktalite_Canilo_WH2700 | 32 VA | 10161683 | 10125196 | 3395 lm |
| CANILO  3P 05 LED4000-827 MF-c ET 03 | 32 VA | Medium Flood | 82 | clear | CANILO_LED_MF.ies | LED | 2700 K | LED | 4000 lm | RAL 9006 white aluminium | Oktalite_Alu_RAL_9006 | Oktalite_Canilo_WH2700 | 32 VA | 10161683 | 10127063 | 3395 lm |
| CANILO  3P 05 LED4000-827 MF  ET 03 | 32 VA | Medium Flood | 82 | without | CANILO_LED_MF.ies | LED | 2700 K | LED | 4000 lm | RAL 9006 white aluminium | Oktalite_Alu_RAL_9006 | Oktalite_Canilo_WH2700 | 32 VA | 10161683 | 10125193 | 3395 lm |
| CANILO  3P 05 LED4000-827 SP-c ET 03 | 32 VA | Spot | 82 | clear | CANILO_LED_SP.ies | LED | 2700 K | LED | 4000 lm | RAL 9006 white aluminium | Oktalite_Alu_RAL_9006 | Oktalite_Canilo_WH2700 | 32 VA | 10161683 | 10127062 | 3395 lm |
| CANILO  3P 05 LED4000-827 SP  ET 03 | 32 VA | Spot | 82 | without | CANILO_LED_SP.ies | LED | 2700 K | LED | 4000 lm | RAL 9006 white aluminium | Oktalite_Alu_RAL_9006 | Oktalite_Canilo_WH2700 | 32 VA | 10161683 | 10125190 | 3395 lm |
| CANILO  3P 01 LED4000-827 VFL-c ET 01 | 32 VA | Very Wide Flood | 82 | clear | CANILO_LED_VFL.ies | LED | 2700 K | LED | 4000 lm | RAL 9016 traffic white | Oktalite_Alu_RAL_9016 | Oktalite_Canilo_WH2700 | 32 VA | 10161682 | 10147536 | 3395 lm |
| CANILO  3P 01 LED4000-827 VFL  ET 01 | 32 VA | Very Wide Flood | 82 | without | CANILO_LED_VFL.ies | LED | 2700 K | LED | 4000 lm | RAL 9016 traffic white | Oktalite_Alu_RAL_9016 | Oktalite_Canilo_WH2700 | 32 VA | 10161682 | 10147502 | 3395 lm |
| CANILO  3P 01 LED4000-827 WFL-c ET 01 | 32 VA | Wide Flood | 82 | clear | CANILO_LED_WFL.ies | LED | 2700 K | LED | 4000 lm | RAL 9016 traffic white | Oktalite_Alu_RAL_9016 | Oktalite_Canilo_WH2700 | 32 VA | 10161682 | 10147535 | 3395 lm |
| CANILO  3P 01 LED4000-827 WFL  ET 01 | 32 VA | Wide Flood | 82 | without | CANILO_LED_WFL.ies | LED | 2700 K | LED | 4000 lm | RAL 9016 traffic white | Oktalite_Alu_RAL_9016 | Oktalite_Canilo_WH2700 | 32 VA | 10161682 | 10147501 | 3395 lm |
| CANILO  3P 01 LED4000-827 FL-c ET 01 | 32 VA | Flood | 82 | clear | CANILO_LED_FL.ies | LED | 2700 K | LED | 4000 lm | RAL 9016 traffic white | Oktalite_Alu_RAL_9016 | Oktalite_Canilo_WH2700 | 32 VA | 10161682 | 10127064 | 3395 lm |
| CANILO  3P 01 LED4000-827 FL  ET 01 | 32 VA | Flood | 82 | without | CANILO_LED_FL.ies | LED | 2700 K | LED | 4000 lm | RAL 9016 traffic white | Oktalite_Alu_RAL_9016 | Oktalite_Canilo_WH2700 | 32 VA | 10161682 | 10125196 | 3395 lm |
| CANILO  3P 01 LED4000-827 MF-c ET 01 | 32 VA | Medium Flood | 82 | clear | CANILO_LED_MF.ies | LED | 2700 K | LED | 4000 lm | RAL 9016 traffic white | Oktalite_Alu_RAL_9016 | Oktalite_Canilo_WH2700 | 32 VA | 10161682 | 10127063 | 3395 lm |
| CANILO  3P 01 LED4000-827 MF  ET 01 | 32 VA | Medium Flood | 82 | without | CANILO_LED_MF.ies | LED | 2700 K | LED | 4000 lm | RAL 9016 traffic white | Oktalite_Alu_RAL_9016 | Oktalite_Canilo_WH2700 | 32 VA | 10161682 | 10125193 | 3395 lm |
| CANILO  3P 01 LED4000-827 SP-c ET 01 | 32 VA | Spot | 82 | clear | CANILO_LED_SP.ies | LED | 2700 K | LED | 4000 lm | RAL 9016 traffic white | Oktalite_Alu_RAL_9016 | Oktalite_Canilo_WH2700 | 32 VA | 10161682 | 10127062 | 3395 lm |
| CANILO  3P 01 LED4000-827 SP  ET 01 | 32 VA | Spot | 82 | without | CANILO_LED_SP.ies | LED | 2700 K | LED | 4000 lm | RAL 9016 traffic white | Oktalite_Alu_RAL_9016 | Oktalite_Canilo_WH2700 | 32 VA | 10161682 | 10125190 | 3395 lm |

note: [stored X ft] marks values corroborated as IEEE doubles in the binary element streams (Revit-internal decimal feet)

## geometry (parser evidence)
native form markers: Sweep x12
no freeform markers — native parametric forms only
